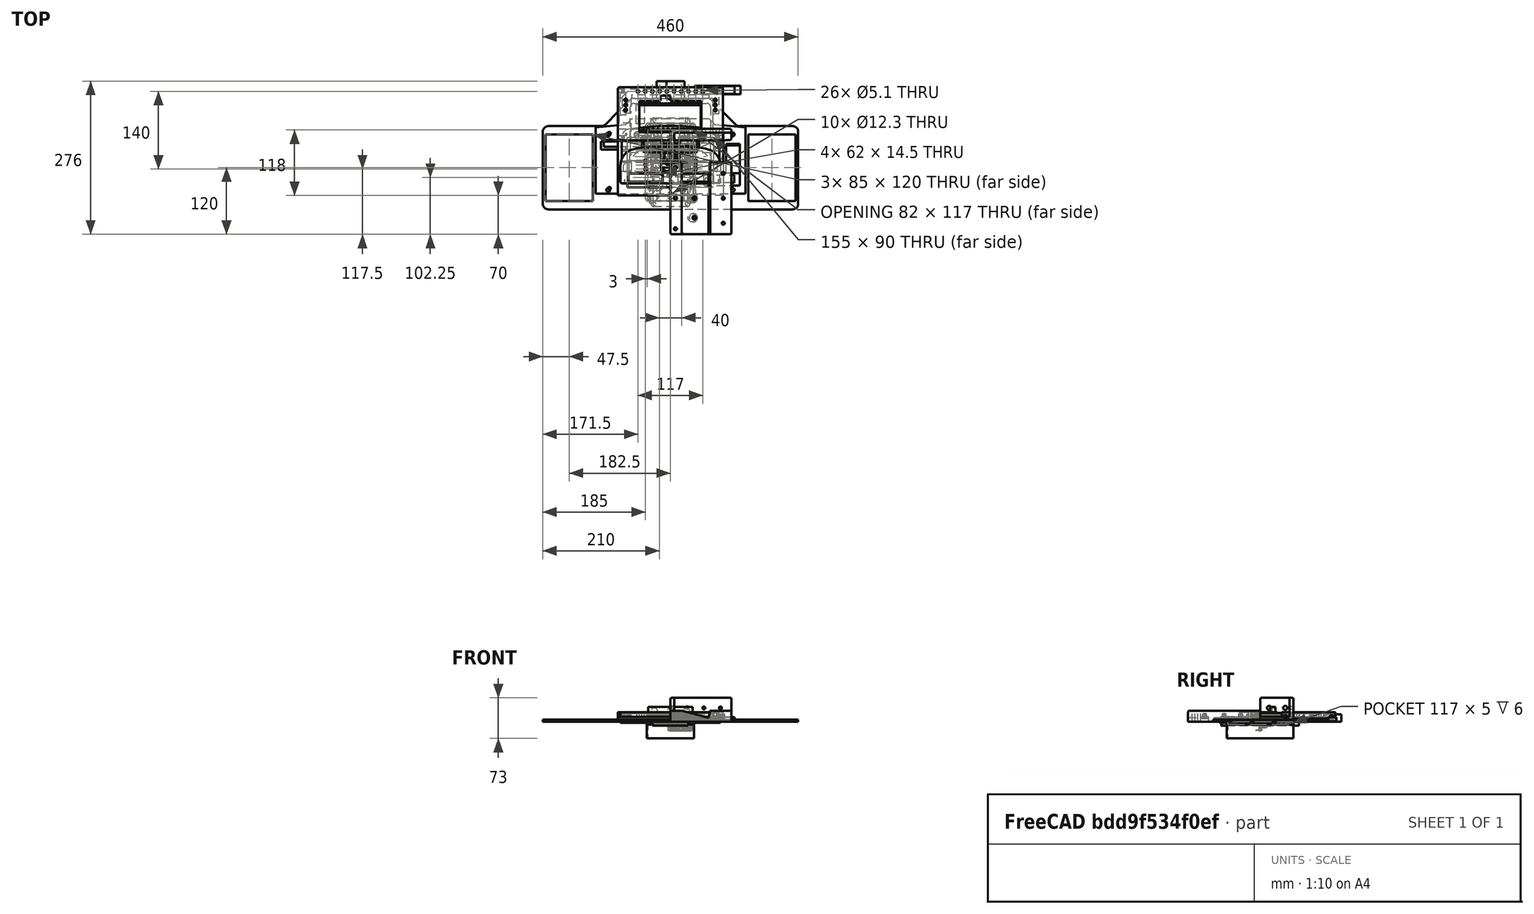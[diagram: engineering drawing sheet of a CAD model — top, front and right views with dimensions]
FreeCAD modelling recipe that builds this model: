
FCSTD DOCUMENT  (FreeCAD 0.18R4 (GitTag))
Label: wheelDashParts
License: All rights reserved
LicenseURL: http://en.wikipedia.org/wiki/All_rights_reserved
objects: Sketcher::SketchObject×55, TechDraw::DrawViewDimension×35, Part::Feature×33, PartDesign::Pad×31, PartDesign::Fillet×29, PartDesign::Body×22, PartDesign::Pocket×22, PartDesign::SubtractiveCylinder×21, PartDesign::SubtractiveBox×4, App::Part×3, PartDesign::Revolution×2, Spreadsheet::Sheet×1, TechDraw::DrawSVGTemplate×1, TechDraw::DrawViewPart×1, TechDraw::DrawPage×1, PartDesign::Plane×1
note: 300 computed .brp shape members not serialized (recipe doc carries the construction recipe); baked Part::Feature solids carry a one-line shape summary decoded from their .brp

FEATURE [Sketcher::SketchObject] Sketch
  MapMode = 5
  Support = -> [XY_Plane]
  sketch-geometry (27):
    g0: LineSegment StartX=-135 StartY=-57 StartZ=0 EndX=135 EndY=-57 EndZ=0
    g1: LineSegment StartX=80 StartY=68 StartZ=0 EndX=70 EndY=78 EndZ=0
    g2: LineSegment StartX=70 StartY=78 StartZ=0 EndX=-70 EndY=78 EndZ=0
    g3: LineSegment StartX=-70 StartY=78 StartZ=0 EndX=-80 EndY=68 EndZ=0
    g4: Circle CenterX=-28 CenterY=50 CenterZ=0 NormalX=0 NormalY=0 NormalZ=1 AngleXU=0 Radius=3.25
    g5: Circle CenterX=28 CenterY=50 CenterZ=0 NormalX=0 NormalY=0 NormalZ=1 AngleXU=0 Radius=3.25
    g6: Circle CenterX=-28 CenterY=-50 CenterZ=0 NormalX=0 NormalY=0 NormalZ=1 AngleXU=0 Radius=3.25
    g7: Circle CenterX=28 CenterY=-50 CenterZ=0 NormalX=0 NormalY=0 NormalZ=1 AngleXU=0 Radius=3.25
    g8: Circle CenterX=0 CenterY=8 CenterZ=0 NormalX=0 NormalY=0 NormalZ=1 AngleXU=0 Radius=25
    g9: LineSegment StartX=-120 StartY=40 StartZ=0 EndX=-30 EndY=40 EndZ=0
    g10: LineSegment StartX=-30 StartY=40 StartZ=0 EndX=-30 EndY=28 EndZ=0
    g11: LineSegment StartX=-30 StartY=28 StartZ=0 EndX=-120 EndY=28 EndZ=0
    g12: LineSegment StartX=-120 StartY=28 StartZ=0 EndX=-120 EndY=40 EndZ=0
    g13: LineSegment StartX=60 StartY=-32 StartZ=0 EndX=60 EndY=-42 EndZ=0
    g14: LineSegment StartX=60 StartY=-42 StartZ=0 EndX=125 EndY=-42 EndZ=0
    g15: LineSegment StartX=125 StartY=-42 StartZ=0 EndX=125 EndY=33 EndZ=0
    g16: LineSegment StartX=125 StartY=33 StartZ=0 EndX=100 EndY=33 EndZ=0
    g17: ArcOfCircle CenterX=5.90695 CenterY=46.0957 CenterZ=0 NormalX=0 NormalY=0 NormalZ=1 AngleXU=0 Radius=95 StartAngle=5.31817 EndAngle=6.1449
    g18: Circle CenterX=-61 CenterY=50 CenterZ=0 NormalX=0 NormalY=0 NormalZ=1 AngleXU=0 Radius=4.5
    g19: Circle CenterX=-110 CenterY=52 CenterZ=0 NormalX=0 NormalY=0 NormalZ=1 AngleXU=0 Radius=2.5
    g20: Circle CenterX=-110 CenterY=-47 CenterZ=0 NormalX=0 NormalY=0 NormalZ=1 AngleXU=0 Radius=2.5
    g21: Circle CenterX=110 CenterY=-47 CenterZ=0 NormalX=0 NormalY=0 NormalZ=1 AngleXU=0 Radius=2.5
    g22: Circle CenterX=110 CenterY=52 CenterZ=0 NormalX=0 NormalY=0 NormalZ=1 AngleXU=0 Radius=2.5
    g23: LineSegment StartX=-135 StartY=63 StartZ=0 EndX=-135 EndY=-57 EndZ=0
    g24: LineSegment StartX=-135 StartY=63 StartZ=0 EndX=-80 EndY=68 EndZ=0
    g25: LineSegment StartX=135 StartY=-57 StartZ=0 EndX=135 EndY=63 EndZ=0
    g26: LineSegment StartX=80 StartY=68 StartZ=0 EndX=135 EndY=63 EndZ=0
  constraints (74):
    c: Coincident(g1,g2)
    c: Coincident(g2,g3)
    c: Symmetric(g0,g0,g-2)
    c: Symmetric(g2,g1,g-2)
    c: Symmetric(g3,g1,g-2)
    c: DistanceX(g0,g0) = 270
    c: Symmetric(g6,g7,g-2)
    c: Symmetric(g4,g5,g-2)
    c: DistanceX(g6,g7) = 56
    c: DistanceY(g7,g5) = 100
    c: PointOnObject(g8,g-2)
    c: Coincident(g9,g10)
    c: Coincident(g10,g11)
    c: Coincident(g11,g12)
    c: Coincident(g12,g9)
    c: Horizontal(g9)
    c: Horizontal(g11)
    c: Vertical(g10)
    c: Vertical(g12)
    c: DistanceY(g12,g12) = 12
    c: DistanceX(g9,g9) = 90
    c: DistanceX(g9,g-1) = 30
    c: Diameter(g4) = 6.5
    c: Vertical(g13)
    c: Coincident(g13,g14)
    c: Horizontal(g14)
    c: Coincident(g14,g15)
    c: Vertical(g15)
    c: Coincident(g15,g16)
    c: Horizontal(g16)
    c: Coincident(g17,g13)
    c: Coincident(g17,g16)
    c: DistanceY(g0,g14) = 15
    c: DistanceX(g-1,g13) = 60
    c: DistanceY(g0,g15) = 90
    c: DistanceX(g-1,g16) = 100
    c: DistanceX(g16,g15) = 25
    c: Diameter(g8) = 50
    c: Equal(g4,g5)
    c: Equal(g5,g7)
    c: Equal(g7,g6)
    c: DistanceY(g0,g18) = 107
    c: DistanceY(g0,g11) = 85
    c: DistanceX(g18,g4) = 33
    c: Vertical(g19,g20)
    c: Symmetric(g19,g22,g-2)
    c: Equal(g21,g19)
    c: Equal(g19,g20)
    c: Equal(g20,g22)
    c: Diameter(g22) = 5
    c: DistanceX(g20,g-1) = 110
    c: DistanceY(g0,g20) = 10
    c: DistanceY(g0,g19) = 109
    c: Symmetric(g5,g7,g-1)
    c: DistanceY(g0,g8) = 65
    c: Diameter(g18) = 9
    c: Symmetric(g21,g20,g-2)
    c: DistanceY(g13,g13) = 10
    c: Diameter(g17) = 190
    c: Vertical(g23)
    c: Coincident(g23,g0)
    c: Coincident(g24,g23)
    c: Coincident(g24,g3)
    c: Coincident(g25,g0)
    c: Vertical(g25)
    c: DistanceY(g23,g23) = 120
    c: Equal(g25,g23)
    c: DistanceX(g3,g1) = 160
    c: DistanceY(g3,g2) = 10
    c: Horizontal(g18,g4)
    c: Coincident(g26,g1)
    c: Coincident(g26,g25)
    c: DistanceX(g3,g2) = 10
    c: DistanceY(g25,g1) = 5
FEATURE [PartDesign::Pad] Pad
  Length = 4
  Length2 = 100
  Profile = -> Sketch
  Type = 0
FEATURE [PartDesign::Body] Body  label="CSLElite"
  Group = -> [Sketch,Pad]
  Origin = -> Origin
  Tip = -> Pad
FEATURE [Sketcher::SketchObject] Sketch004
  MapMode = 5
  Support = -> [XY_Plane003]
  expr: Constraints[18] = data.bluWin_disp_length
  expr: Constraints[19] = data.bluWin_disp_width
  expr: Constraints[9] = data.bluWin_width
  expr: Constraints[8] = data.bluWin_length
  sketch-geometry (8):
    g0: LineSegment StartX=-72.5 StartY=36 StartZ=0 EndX=72.5 EndY=36 EndZ=0
    g1: LineSegment StartX=72.5 StartY=36 StartZ=0 EndX=72.5 EndY=-36 EndZ=0
    g2: LineSegment StartX=72.5 StartY=-36 StartZ=0 EndX=-72.5 EndY=-36 EndZ=0
    g3: LineSegment StartX=-72.5 StartY=-36 StartZ=0 EndX=-72.5 EndY=36 EndZ=0
    g4: LineSegment StartX=-57.5 StartY=32.5 StartZ=0 EndX=54.5 EndY=32.5 EndZ=0
    g5: LineSegment StartX=54.5 StartY=32.5 StartZ=0 EndX=54.5 EndY=-23.5 EndZ=0
    g6: LineSegment StartX=54.5 StartY=-23.5 StartZ=0 EndX=-57.5 EndY=-23.5 EndZ=0
    g7: LineSegment StartX=-57.5 StartY=-23.5 StartZ=0 EndX=-57.5 EndY=32.5 EndZ=0
  constraints (22):
    c: Coincident(g0,g1)
    c: Coincident(g1,g2)
    c: Coincident(g2,g3)
    c: Coincident(g3,g0)
    c: Horizontal(g2)
    c: Vertical(g3)
    c: Symmetric(g0,g0,g-2)
    c: Symmetric(g0,g1,g-1)
    c: DistanceX(g0,g0) = 145
    c: DistanceY(g1,g1) = 72
    c: Coincident(g4,g5)
    c: Coincident(g5,g6)
    c: Coincident(g6,g7)
    c: Coincident(g7,g4)
    c: Horizontal(g6)
    c: Vertical(g5)
    c: Vertical(g7)
    c: DistanceY(g4,g0) = 3.5
    c: DistanceX(g4,g4) = 112
    c: DistanceY(g7,g7) = 56
    c: DistanceX(g0,g4) = 15
    c: Equal(g7,g5)
FEATURE [PartDesign::Pad] Pad003
  Length = 9
  Length2 = 100
  Profile = -> Sketch004
  Type = 0
FEATURE [PartDesign::Fillet] Fillet003  label="bluWinHdLteFillet"
  Base = -> Pad003 [Edge1,Edge2,Edge8,Edge5]
  BaseFeature = -> Pad003
  Radius = 7
FEATURE [PartDesign::Body] Body003  label="bluWinHdLte"
  Group = -> [Sketch004,Pad003,Fillet003]
  Origin = -> Origin003
  Placement = pos=(0,70,0) rot=(0,0,1;0rad)
  Tip = -> Fillet003
FEATURE [Sketcher::SketchObject] Sketch005
  MapMode = 5
  Support = -> [XY_Plane004]
  sketch-geometry (8):
    g0: LineSegment StartX=-95 StartY=60 StartZ=0 EndX=95 EndY=60 EndZ=0
    g1: LineSegment StartX=95 StartY=60 StartZ=0 EndX=95 EndY=-60 EndZ=0
    g2: LineSegment StartX=95 StartY=-60 StartZ=0 EndX=-95 EndY=-60 EndZ=0
    g3: LineSegment StartX=-95 StartY=-60 StartZ=0 EndX=-95 EndY=60 EndZ=0
    g4: LineSegment StartX=-77.5 StartY=45 StartZ=0 EndX=77.5 EndY=45 EndZ=0
    g5: LineSegment StartX=77.5 StartY=45 StartZ=0 EndX=77.5 EndY=-45 EndZ=0
    g6: LineSegment StartX=77.5 StartY=-45 StartZ=0 EndX=-77.5 EndY=-45 EndZ=0
    g7: LineSegment StartX=-77.5 StartY=-45 StartZ=0 EndX=-77.5 EndY=45 EndZ=0
  constraints (20):
    c: Coincident(g0,g1)
    c: Coincident(g1,g2)
    c: Coincident(g2,g3)
    c: Coincident(g3,g0)
    c: Horizontal(g2)
    c: Vertical(g3)
    c: Symmetric(g0,g0,g-2)
    c: Symmetric(g0,g1,g-1)
    c: DistanceY(g1,g1) = 120
    c: DistanceX(g0,g0) = 190
    c: Coincident(g4,g5)
    c: Coincident(g5,g6)
    c: Coincident(g6,g7)
    c: Coincident(g7,g4)
    c: Horizontal(g6)
    c: Vertical(g7)
    c: Symmetric(g4,g5,g-1)
    c: Symmetric(g4,g4,g-2)
    c: DistanceX(g4,g4) = 155
    c: DistanceY(g5,g5) = 90
FEATURE [PartDesign::Pad] Pad004
  Length = 9
  Length2 = 100
  Profile = -> Sketch005
  Type = 0
FEATURE [PartDesign::Body] Body004  label="elfIItablet"
  Group = -> [Sketch005,Pad004]
  Origin = -> Origin004
  Tip = -> Pad004
FEATURE [Sketcher::SketchObject] Sketch006
  MapMode = 5
  Support = -> [XY_Plane005]
  expr: Constraints[9] = data.max8x8_width
  expr: Constraints[8] = data.max8x8_length
  sketch-geometry (4):
    g0: LineSegment StartX=-25 StartY=16 StartZ=0 EndX=25 EndY=16 EndZ=0
    g1: LineSegment StartX=25 StartY=16 StartZ=0 EndX=25 EndY=-16 EndZ=0
    g2: LineSegment StartX=25 StartY=-16 StartZ=0 EndX=-25 EndY=-16 EndZ=0
    g3: LineSegment StartX=-25 StartY=-16 StartZ=0 EndX=-25 EndY=16 EndZ=0
  constraints (10):
    c: Coincident(g0,g1)
    c: Coincident(g1,g2)
    c: Coincident(g2,g3)
    c: Coincident(g3,g0)
    c: Horizontal(g2)
    c: Vertical(g3)
    c: Symmetric(g0,g0,g-2)
    c: Symmetric(g0,g1,g-1)
    c: DistanceX(g0,g0) = 50
    c: DistanceY(g1,g1) = 32
FEATURE [PartDesign::Pad] Pad005
  Length = 1.5
  Length2 = 100
  Profile = -> Sketch006
  Type = 0
FEATURE [Sketcher::SketchObject] Sketch007
  ExternalGeometry = -> [Pad005]
  MapMode = 5
  Placement = pos=(0,0,1.5) rot=(0,0,1;0rad)
  Support = -> [Pad005]
  sketch-geometry (4):
    g0: LineSegment StartX=25 StartY=16 StartZ=0 EndX=-7 EndY=16 EndZ=0
    g1: LineSegment StartX=-7 StartY=16 StartZ=0 EndX=-7 EndY=-16 EndZ=0
    g2: LineSegment StartX=-7 StartY=-16 StartZ=0 EndX=25 EndY=-16 EndZ=0
    g3: LineSegment StartX=25 StartY=-16 StartZ=0 EndX=25 EndY=16 EndZ=0
  constraints (11):
    c: Coincident(g0,g1)
    c: Coincident(g1,g2)
    c: Coincident(g2,g3)
    c: Coincident(g3,g0)
    c: Horizontal(g0)
    c: Horizontal(g2)
    c: Vertical(g1)
    c: Vertical(g3)
    c: Equal(g3,g-3)
    c: Equal(g3,g0)
    c: Coincident(g-3,g0)
FEATURE [PartDesign::Pad] Pad006  label="max7219_8x8"
  BaseFeature = -> Pad005
  Length = 12
  Length2 = 100
  Profile = -> Sketch007
  Type = 0
  expr: Length = data.max8x8_height
FEATURE [PartDesign::Body] Body005  label="max7219module"
  Group = -> [Sketch006,Pad005,Sketch007,Pad006]
  Origin = -> Origin005
  Placement = pos=(0,130,0) rot=(0,0,1;0rad)
  Tip = -> Pad006
FEATURE [Sketcher::SketchObject] Sketch008
  MapMode = 5
  Support = -> [XY_Plane006]
  expr: Constraints[8] = data.seg7_length_all
  expr: Constraints[9] = data.seg7_width_all
  sketch-geometry (4):
    g0: LineSegment StartX=-41.15 StartY=7.75 StartZ=0 EndX=41.15 EndY=7.75 EndZ=0
    g1: LineSegment StartX=41.15 StartY=7.75 StartZ=0 EndX=41.15 EndY=-7.75 EndZ=0
    g2: LineSegment StartX=41.15 StartY=-7.75 StartZ=0 EndX=-41.15 EndY=-7.75 EndZ=0
    g3: LineSegment StartX=-41.15 StartY=-7.75 StartZ=0 EndX=-41.15 EndY=7.75 EndZ=0
  constraints (10):
    c: Coincident(g0,g1)
    c: Coincident(g1,g2)
    c: Coincident(g2,g3)
    c: Coincident(g3,g0)
    c: Horizontal(g0)
    c: Vertical(g1)
    c: Symmetric(g0,g2,g-1)
    c: Symmetric(g2,g1,g-2)
    c: DistanceX(g0,g0) = 82.3
    c: DistanceY(g3,g3) = 15.5
FEATURE [Spreadsheet::Sheet] Spreadsheet  label="data"
  cells = A1=7seg-length-all; B1(seg7_length_all)=82.3; A2=7seg-width-all; B2(seg7_width_all)=15.5; A3=7seg-length; B3(seg7_length)=61; A4=7seg-width; B4(seg7_width)=14.2; A5=7seg-height; B5(seg7_height)=7.6; A6=8x8-length-all; B6(max8x8_length)=50; A7=8x8-width-all; B7(max8x8_width)=32; A8=8x8-height; B8(max8x8_height)=12; A9=bluWin-length; B9(bluWin_length)=145; A10=bluWin-width; B10(bluWin_width)=72; A11=bluWin-height; B11(bluWin_height)=9; A12=bluWin-disp-length; B12(bluWin_disp_length)=112; A13=bluWin-disp-width; B13(bluWin_disp_width)=56; A14=bluWin-disp-leftdistance; B14(bluWin_disp_left)=15; A15=bluWin-disp-rightdistance; B15(bluWin_disp_right)=20; A16=bluWin_usblength; B16(bluWin_usblength)=20; A17=bluWin-disp-bottomdistance; B17(bluWin_disp_bottom)=13; A18=bluWin-disp-addline height; B18(bluWin_disp_addline)=7; A19=phoneholder thicknes of sides; B19(phoneholder_sides_thickness)=2; A20=rgbled radius; B20(rgbled_radius)=2.5; A21=rgbled length; B21(rgbled_length)=8; A22=phoneholder ledpart height; B22(phoneholder_ledpart_height)=10; A23=phoneholder total width; B23(phoneholder_width)==B12 + B14 + B15 + 2 * B16 + B19; D23=bluwin_disp_width+bluwin_disp_left+bluwin_disp_right_+(2*bluWin_usblength)+(2*phoneholder_sides_thickness)+(2*phoneholder_ledpart_height); A24=smalldash thickness; B24(smalldash_thickness)=17; A25=smalldash front thickness; B25(smalldash_frontthickness)=2
FEATURE [PartDesign::Pad] Pad007
  Length = 1
  Length2 = 100
  Profile = -> Sketch008
  Type = 0
FEATURE [Sketcher::SketchObject] Sketch009
  MapMode = 5
  Placement = pos=(0,0,1) rot=(0,0,1;0rad)
  Support = -> [Pad007]
  expr: Constraints[9] = data.seg7_width
  expr: Constraints[8] = data.seg7_length
  sketch-geometry (4):
    g0: LineSegment StartX=-30.5 StartY=7.1 StartZ=0 EndX=30.5 EndY=7.1 EndZ=0
    g1: LineSegment StartX=30.5 StartY=7.1 StartZ=0 EndX=30.5 EndY=-7.1 EndZ=0
    g2: LineSegment StartX=30.5 StartY=-7.1 StartZ=0 EndX=-30.5 EndY=-7.1 EndZ=0
    g3: LineSegment StartX=-30.5 StartY=-7.1 StartZ=0 EndX=-30.5 EndY=7.1 EndZ=0
  constraints (10):
    c: Coincident(g0,g1)
    c: Coincident(g1,g2)
    c: Coincident(g2,g3)
    c: Coincident(g3,g0)
    c: Horizontal(g2)
    c: Vertical(g1)
    c: Symmetric(g0,g2,g-1)
    c: Symmetric(g0,g0,g-2)
    c: DistanceX(g2,g2) = 61
    c: DistanceY(g1,g1) = 14.2
FEATURE [PartDesign::Pad] Pad008  label="max7219-7seg"
  BaseFeature = -> Pad007
  Length = 7.6
  Length2 = 100
  Profile = -> Sketch009
  Type = 0
  expr: Length = data.seg7_height
FEATURE [PartDesign::Body] Body006  label="max7219_7seg"
  Group = -> [Sketch008,Pad007,Sketch009,Pad008]
  Origin = -> Origin006
  Placement = pos=(85,130,0) rot=(0,0,1;0rad)
  Tip = -> Pad008
FEATURE [Sketcher::SketchObject] Sketch010
  MapMode = 5
  Support = -> [XY_Plane002]
  sketch-geometry (47):
    g0: LineSegment [constr] StartX=-135 StartY=60 StartZ=0 EndX=135 EndY=60 EndZ=0
    g1: LineSegment [constr] StartX=135 StartY=60 StartZ=0 EndX=135 EndY=-60 EndZ=0
    g2: LineSegment [constr] StartX=135 StartY=-60 StartZ=0 EndX=-135 EndY=-60 EndZ=0
    g3: LineSegment [constr] StartX=-135 StartY=-60 StartZ=0 EndX=-135 EndY=60 EndZ=0
    g4: LineSegment StartX=-230 StartY=-85 StartZ=0 EndX=-230 EndY=65 EndZ=0
    g5: LineSegment StartX=-230 StartY=65 StartZ=0 EndX=-120 EndY=65 EndZ=0
    g6: LineSegment StartX=-120 StartY=65 StartZ=0 EndX=-70 EndY=115 EndZ=0
    g7: LineSegment StartX=-70 StartY=115 StartZ=0 EndX=70 EndY=115 EndZ=0
    g8: LineSegment StartX=70 StartY=115 StartZ=0 EndX=120 EndY=65 EndZ=0
    g9: LineSegment StartX=120 StartY=65 StartZ=0 EndX=230 EndY=65 EndZ=0
    g10: LineSegment StartX=230 StartY=65 StartZ=0 EndX=230 EndY=-85 EndZ=0
    g11: LineSegment StartX=230 StartY=-85 StartZ=0 EndX=-230 EndY=-85 EndZ=0
    g12: Circle CenterX=0 CenterY=-3.1e-15 CenterZ=0 NormalX=0 NormalY=0 NormalZ=1 AngleXU=0 Radius=27.5
    g13: Circle CenterX=-28 CenterY=51 CenterZ=0 NormalX=0 NormalY=0 NormalZ=1 AngleXU=0 Radius=3.25
    g14: Circle CenterX=28 CenterY=51 CenterZ=0 NormalX=0 NormalY=0 NormalZ=1 AngleXU=0 Radius=3.25
    g15: Circle CenterX=-28 CenterY=-49 CenterZ=0 NormalX=0 NormalY=0 NormalZ=1 AngleXU=0 Radius=3.25
    g16: Circle CenterX=28 CenterY=-49 CenterZ=0 NormalX=0 NormalY=0 NormalZ=1 AngleXU=0 Radius=3.25
    g17: Circle CenterX=-112 CenterY=-50 CenterZ=0 NormalX=0 NormalY=0 NormalZ=1 AngleXU=0 Radius=3.5
    g18: Circle CenterX=-112 CenterY=50 CenterZ=0 NormalX=0 NormalY=0 NormalZ=1 AngleXU=0 Radius=3.5
    g19: Circle CenterX=112 CenterY=50 CenterZ=0 NormalX=0 NormalY=0 NormalZ=1 AngleXU=0 Radius=3.5
    g20: Circle CenterX=112 CenterY=-50 CenterZ=0 NormalX=0 NormalY=0 NormalZ=1 AngleXU=0 Radius=3.5
    g21: Circle CenterX=-61 CenterY=47 CenterZ=0 NormalX=0 NormalY=0 NormalZ=1 AngleXU=0 Radius=4.5
    g22: Circle CenterX=61 CenterY=47 CenterZ=0 NormalX=0 NormalY=0 NormalZ=1 AngleXU=0 Radius=4.5
    g23: LineSegment StartX=100 StartY=30 StartZ=0 EndX=125 EndY=30 EndZ=0
    g24: LineSegment StartX=125 StartY=30 StartZ=0 EndX=125 EndY=-20 EndZ=0
    g25: LineSegment StartX=125 StartY=-20 StartZ=0 EndX=100 EndY=-20 EndZ=0
    g26: LineSegment StartX=100 StartY=-20 StartZ=0 EndX=100 EndY=30 EndZ=0
    g27: LineSegment StartX=60 StartY=-23 StartZ=0 EndX=115 EndY=-23 EndZ=0
    g28: LineSegment StartX=115 StartY=-23 StartZ=0 EndX=115 EndY=-37 EndZ=0
    g29: LineSegment StartX=115 StartY=-37 StartZ=0 EndX=60 EndY=-37 EndZ=0
    g30: LineSegment StartX=60 StartY=-37 StartZ=0 EndX=60 EndY=-23 EndZ=0
    g31: LineSegment StartX=-125 StartY=37 StartZ=0 EndX=-25 EndY=37 EndZ=0
    g32: LineSegment StartX=-25 StartY=37 StartZ=0 EndX=-25 EndY=23 EndZ=0
    g33: LineSegment StartX=-25 StartY=23 StartZ=0 EndX=-125 EndY=23 EndZ=0
    g34: LineSegment StartX=-125 StartY=23 StartZ=0 EndX=-125 EndY=37 EndZ=0
    g35: LineSegment StartX=140 StartY=50 StartZ=0 EndX=225 EndY=50 EndZ=0
    g36: LineSegment StartX=225 StartY=50 StartZ=0 EndX=225 EndY=-70 EndZ=0
    g37: LineSegment StartX=225 StartY=-70 StartZ=0 EndX=140 EndY=-70 EndZ=0
    g38: LineSegment StartX=140 StartY=-70 StartZ=0 EndX=140 EndY=50 EndZ=0
    g39: LineSegment StartX=-225 StartY=50 StartZ=0 EndX=-140 EndY=50 EndZ=0
    g40: LineSegment StartX=-140 StartY=50 StartZ=0 EndX=-140 EndY=-70 EndZ=0
    g41: LineSegment StartX=-140 StartY=-70 StartZ=0 EndX=-225 EndY=-70 EndZ=0
    g42: LineSegment StartX=-225 StartY=-70 StartZ=0 EndX=-225 EndY=50 EndZ=0
    g43: LineSegment StartX=-62 StartY=104 StartZ=0 EndX=-47 EndY=104 EndZ=0
    g44: LineSegment StartX=-47 StartY=104 StartZ=0 EndX=-47 EndY=69 EndZ=0
    g45: LineSegment StartX=-47 StartY=69 StartZ=0 EndX=-62 EndY=69 EndZ=0
    g46: LineSegment StartX=-62 StartY=69 StartZ=0 EndX=-62 EndY=104 EndZ=0
  constraints (130):
    c: Coincident(g0,g1)
    c: Coincident(g1,g2)
    c: Coincident(g2,g3)
    c: Coincident(g3,g0)
    c: Horizontal(g2)
    c: Vertical(g1)
    c: DistanceY(g3,g3) = 120
    c: DistanceX(g0,g0) = 270
    c: Symmetric(g0,g0,g-2)
    c: Symmetric(g0,g2,g-1)
    c: Vertical(g4)
    c: Coincident(g4,g5)
    c: Horizontal(g5)
    c: Coincident(g5,g6)
    c: Coincident(g6,g7)
    c: Coincident(g7,g8)
    c: Coincident(g8,g9)
    c: Coincident(g9,g10)
    c: Vertical(g10)
    c: Coincident(g10,g11)
    c: Coincident(g4,g11)
    c: DistanceY(g4,g4) = 150
    c: DistanceX(g11,g11) = 460
    c: Symmetric(g4,g10,g-2)
    c: Equal(g4,g10)
    c: Symmetric(g6,g7,g-2)
    c: Symmetric(g5,g8,g-2)
    c: PointOnObject(g12,g-2)
    c: DistanceY(g1,g12) = 60
    c: DistanceY(g4,g6) = 50
    c: Diameter(g12) = 55
    c: Symmetric(g15,g16,g-2)
    c: Symmetric(g13,g14,g-2)
    c: Vertical(g13,g15)
    c: Equal(g13,g14)
    c: Equal(g14,g16)
    c: Equal(g16,g15)
    c: DistanceY(g2,g15) = 11
    c: DistanceX(g15,g16) = 56
    c: DistanceY(g16,g14) = 100
    c: DistanceY(g4,g2) = 25
    c: Equal(g18,g17)
    c: Equal(g17,g20)
    c: Equal(g20,g19)
    c: DistanceY(g2,g17) = 10
    c: DistanceY(g2,g18) = 110
    c: Symmetric(g18,g19,g-2)
    c: Symmetric(g17,g20,g-2)
    c: DistanceX(g17,g12) = 112
    c: Vertical(g18,g17)
    c: DistanceX(g21,g13) = 33
    c: DistanceY(g2,g21) = 107
    c: Symmetric(g21,g22,g-2)
    c: Equal(g21,g22)
    c: Diameter(g18) = 7
    c: Diameter(g22) = 9
    c: Diameter(g15) = 6.5
    c: DistanceX(g8,g9) = 110
    c: Coincident(g23,g24)
    c: Coincident(g24,g25)
    c: Coincident(g25,g26)
    c: Coincident(g26,g23)
    c: Horizontal(g23)
    c: Horizontal(g25)
    c: Vertical(g24)
    c: Vertical(g26)
    c: DistanceX(g23,g23) = 25
    c: DistanceY(g26,g26) = 50
    c: DistanceY(g1,g25) = 40
    c: DistanceX(g12,g25) = 100
    c: Coincident(g27,g28)
    c: Coincident(g28,g29)
    c: Coincident(g29,g30)
    c: Coincident(g30,g27)
    c: Horizontal(g27)
    c: Horizontal(g29)
    c: Vertical(g28)
    c: Vertical(g30)
    c: DistanceX(g29,g29) = 55
    c: DistanceY(g28,g28) = 14
    c: DistanceY(g1,g29) = 23
    c: DistanceX(g12,g27) = 60
    c: Coincident(g31,g32)
    c: Coincident(g32,g33)
    c: Coincident(g33,g34)
    c: Coincident(g34,g31)
    c: Horizontal(g31)
    c: Horizontal(g33)
    c: Vertical(g32)
    c: Vertical(g34)
    c: DistanceX(g33,g33) = 100
    c: DistanceX(g32,g12) = 25
    c: DistanceY(g2,g33) = 83
    c: Coincident(g35,g36)
    c: Coincident(g36,g37)
    c: Coincident(g37,g38)
    c: Coincident(g38,g35)
    c: Horizontal(g35)
    c: Horizontal(g37)
    c: Vertical(g36)
    c: Vertical(g38)
    c: DistanceX(g35,g35) = 85
    c: DistanceY(g38,g38) = 120
    c: DistanceX(g35,g9) = 5
    c: DistanceY(g35,g9) = 15
    c: Coincident(g39,g40)
    c: Coincident(g40,g41)
    c: Coincident(g41,g42)
    c: Coincident(g42,g39)
    c: Horizontal(g39)
    c: Horizontal(g41)
    c: Vertical(g40)
    c: Vertical(g42)
    c: Equal(g38,g40)
    c: Equal(g41,g37)
    c: Symmetric(g40,g37,g-2)
    c: DistanceY(g34,g34) = 14
    c: Coincident(g43,g44)
    c: Coincident(g44,g45)
    c: Coincident(g45,g46)
    c: Coincident(g46,g43)
    c: Horizontal(g43)
    c: Horizontal(g45)
    c: Vertical(g44)
    c: Vertical(g46)
    c: DistanceX(g43,g43) = 15
    c: DistanceY(g44,g44) = 35
    c: DistanceX(g6,g43) = 8
    c: DistanceY(g43,g6) = 11
    c: Angle(g8) = -0.785398
FEATURE [PartDesign::Pad] Pad009
  Length = 4
  Length2 = 100
  Profile = -> Sketch010
  Type = 0
FEATURE [PartDesign::Fillet] Fillet004
  Base = -> Pad009 [Edge14,Edge11,Edge8,Edge5,Edge2,Edge17,Edge1,Edge20]
  BaseFeature = -> Pad009
  Radius = 10
FEATURE [PartDesign::Body] Body002  label="Dashboard"
  Group = -> [Sketch010,Pad009,Fillet004]
  Origin = -> Origin002
  Tip = -> Fillet004
FEATURE [Sketcher::SketchObject] Sketch011
  MapMode = 5
  Support = -> [XY_Plane007]
  expr: Constraints[6] = data.bluWin_disp_length
  expr: Constraints[31] = data.bluWin_disp_bottom
  expr: Constraints[30] = data.bluWin_length
  expr: Constraints[7] = data.bluWin_disp_width
  expr: Constraints[17] = data.bluWin_disp_bottom + data.phoneholder_sides_thickness
  expr: Constraints[18] = data.phoneholder_sides_thickness * 2 + data.bluWin_width + 2 * data.phoneholder_ledpart_height
  expr: Constraints[20] = data.phoneholder_width
  expr: Constraints[29] = data.bluWin_width
  expr: Constraints[32] = data.bluWin_disp_left
  sketch-geometry (16):
    g0: LineSegment StartX=-56 StartY=28 StartZ=0 EndX=56 EndY=28 EndZ=0
    g1: LineSegment StartX=56 StartY=28 StartZ=0 EndX=56 EndY=-28 EndZ=0
    g2: LineSegment StartX=56 StartY=-28 StartZ=0 EndX=-56 EndY=-28 EndZ=0
    g3: LineSegment StartX=-56 StartY=-28 StartZ=0 EndX=-56 EndY=28 EndZ=0
    g4: LineSegment StartX=-94.5 StartY=53 StartZ=0 EndX=94.5 EndY=53 EndZ=0
    g5: LineSegment StartX=94.5 StartY=53 StartZ=0 EndX=94.5 EndY=-43 EndZ=0
    g6: LineSegment StartX=94.5 StartY=-43 StartZ=0 EndX=-94.5 EndY=-43 EndZ=0
    g7: LineSegment StartX=-94.5 StartY=-43 StartZ=0 EndX=-94.5 EndY=53 EndZ=0
    g8: LineSegment [constr] StartX=-71 StartY=31 StartZ=0 EndX=74 EndY=31 EndZ=0
    g9: LineSegment [constr] StartX=74 StartY=31 StartZ=0 EndX=74 EndY=-41 EndZ=0
    g10: LineSegment [constr] StartX=74 StartY=-41 StartZ=0 EndX=-71 EndY=-41 EndZ=0
    g11: LineSegment [constr] StartX=-71 StartY=-41 StartZ=0 EndX=-71 EndY=31 EndZ=0
    g12: LineSegment [constr] StartX=-91.5 StartY=43 StartZ=0 EndX=-81.5 EndY=43 EndZ=0
    g13: LineSegment [constr] StartX=-81.5 StartY=43 StartZ=0 EndX=-81.5 EndY=25 EndZ=0
    g14: LineSegment [constr] StartX=-81.5 StartY=25 StartZ=0 EndX=-91.5 EndY=25 EndZ=0
    g15: LineSegment [constr] StartX=-91.5 StartY=25 StartZ=0 EndX=-91.5 EndY=43 EndZ=0
  constraints (45):
    c: Coincident(g0,g1)
    c: Coincident(g1,g2)
    c: Coincident(g2,g3)
    c: Coincident(g3,g0)
    c: Horizontal(g2)
    c: Vertical(g3)
    c: DistanceX(g0,g0) = 112
    c: DistanceY(g1,g1) = 56
    c: Symmetric(g0,g0,g-2)
    c: Symmetric(g0,g1,g-1)
    c: Coincident(g4,g5)
    c: Coincident(g5,g6)
    c: Coincident(g6,g7)
    c: Coincident(g7,g4)
    c: Horizontal(g6)
    c: Vertical(g7)
    c: Symmetric(g4,g4,g-2)
    c: DistanceY(g5,g1) = 15
    c: DistanceY(g5,g5) = 96
    c: Vertical(g5)
    c: DistanceX(g6,g6) = 189
    c: Coincident(g8,g9)
    c: Coincident(g9,g10)
    c: Coincident(g10,g11)
    c: Coincident(g11,g8)
    c: Horizontal(g8)
    c: Horizontal(g10)
    c: Vertical(g9)
    c: Vertical(g11)
    c: DistanceY(g11,g11) = 72
    c: DistanceX(g10,g10) = 145
    c: DistanceY(g10,g2) = 13
    c: DistanceX(g10,g2) = 15
    c: Coincident(g12,g13)
    c: Coincident(g13,g14)
    c: Coincident(g14,g15)
    c: Coincident(g15,g12)
    c: Horizontal(g12)
    c: Horizontal(g14)
    c: Vertical(g13)
    c: Vertical(g15)
    c: DistanceX(g12,g12) = 10
    c: DistanceY(g13,g13) = 18
    c: DistanceX(g4,g12) = 3
    c: DistanceY(g12,g4) = 10
FEATURE [PartDesign::Pad] Pad010
  Length = 2
  Length2 = 100
  Profile = -> Sketch011
  Type = 0
FEATURE [Sketcher::SketchObject] Sketch012
  ExternalGeometry = -> [Pad010]
  MapMode = 5
  Placement = pos=(0,0,0) rot=(1,0,0;3.14159rad)
  Support = -> [Pad010]
  expr: Constraints[29] = data.bluWin_disp_right
  expr: Constraints[17] = data.bluWin_disp_bottom
  expr: Constraints[27] = data.bluWin_usblength + 1
  expr: Constraints[14] = data.bluWin_width + 2
  expr: Constraints[18] = data.bluWin_disp_left
  sketch-geometry (15):
    g0: LineSegment StartX=-94.5 StartY=43 StartZ=0 EndX=94.5 EndY=43 EndZ=0
    g1: LineSegment StartX=94.5 StartY=43 StartZ=0 EndX=94.5 EndY=-53 EndZ=0
    g2: LineSegment StartX=94.5 StartY=-53 StartZ=0 EndX=-94.5 EndY=-53 EndZ=0
    g3: LineSegment StartX=-94.5 StartY=-53 StartZ=0 EndX=-94.5 EndY=43 EndZ=0
    g4: LineSegment StartX=-71 StartY=41 StartZ=0 EndX=76 EndY=41 EndZ=0
    g5: LineSegment StartX=76 StartY=-33 StartZ=0 EndX=-71 EndY=-33 EndZ=0
    g6: LineSegment StartX=-71 StartY=-33 StartZ=0 EndX=-71 EndY=-7 EndZ=0
    g7: LineSegment StartX=76 StartY=-33 StartZ=0 EndX=76 EndY=41 EndZ=0
    g8: LineSegment StartX=-71 StartY=12 StartZ=0 EndX=-92 EndY=12 EndZ=0
    g9: LineSegment StartX=-92 StartY=12 StartZ=0 EndX=-92 EndY=-34 EndZ=0
    g10: LineSegment StartX=-92 StartY=-34 StartZ=0 EndX=-87 EndY=-34 EndZ=0
    g11: LineSegment StartX=-87 StartY=-34 StartZ=0 EndX=-87 EndY=-11.9497 EndZ=0
    g12: LineSegment StartX=-82.0503 StartY=-7 StartZ=0 EndX=-71 EndY=-7 EndZ=0
    g13: LineSegment StartX=-71 StartY=12 StartZ=0 EndX=-71 EndY=41 EndZ=0
    g14: LineSegment StartX=-87 StartY=-11.9497 StartZ=0 EndX=-82.0503 EndY=-7 EndZ=0
  constraints (42):
    c: Coincident(g0,g1)
    c: Coincident(g1,g2)
    c: Coincident(g2,g3)
    c: Coincident(g3,g0)
    c: Horizontal(g0)
    c: Horizontal(g2)
    c: Vertical(g1)
    c: Vertical(g3)
    c: Coincident(g0,g-5)
    c: Coincident(g1,g-6)
    c: Coincident(g13,g4)
    c: Horizontal(g4)
    c: Horizontal(g5)
    c: Vertical(g6)
    c: DistanceY(g6,g13) = 74
    c: Vertical(g7)
    c: Coincident(g5,g7)
    c: DistanceY(g-3,g4) = 13
    c: DistanceX(g4,g-3) = 15
    c: Horizontal(g8)
    c: Coincident(g8,g9)
    c: Vertical(g9)
    c: Coincident(g9,g10)
    c: Horizontal(g10)
    c: Coincident(g10,g11)
    c: Vertical(g11)
    c: Horizontal(g12)
    c: DistanceX(g8,g8) = 21
    c: Coincident(g4,g7)
    c: DistanceX(g-3,g4) = 20
    c: Coincident(g6,g12)
    c: Tangent(g6,g13)
    c: DistanceX(g10,g10) = 5
    c: Coincident(g6,g5)
    c: DistanceY(g5,g6) = 26
    c: DistanceY(g5,g8) = 45
    c: Coincident(g8,g13)
    c: DistanceY(g9,g8) = 46
    c: Coincident(g12,g14)
    c: Coincident(g11,g14)
    c: Distance(g14) = 7
    c: Angle(g14) = 0.785398
FEATURE [PartDesign::Pad] Pad011
  BaseFeature = -> Pad010
  Length = 9.5
  Length2 = 100
  Profile = -> Sketch012
  Type = 0
  expr: Length = data.bluWin_height + 0.5
FEATURE [Sketcher::SketchObject] Sketch013
  ExternalGeometry = -> [Pad011]
  MapMode = 5
  Placement = pos=(0,0,-9.5) rot=(1,0,0;3.14159rad)
  Support = -> [Pad011]
  sketch-geometry (4):
    g0: Circle CenterX=-86.5 CenterY=37 CenterZ=0 NormalX=0 NormalY=0 NormalZ=1 AngleXU=0 Radius=1.7
    g1: Circle CenterX=-86.5 CenterY=-47 CenterZ=0 NormalX=0 NormalY=0 NormalZ=1 AngleXU=0 Radius=1.7
    g2: Circle CenterX=86.5 CenterY=37 CenterZ=0 NormalX=0 NormalY=0 NormalZ=1 AngleXU=0 Radius=1.7
    g3: Circle CenterX=86.5 CenterY=-47 CenterZ=0 NormalX=0 NormalY=0 NormalZ=1 AngleXU=0 Radius=1.7
  constraints (11):
    c: Equal(g0,g1)
    c: Equal(g1,g3)
    c: Equal(g3,g2)
    c: Vertical(g0,g1)
    c: Vertical(g3,g2)
    c: Symmetric(g0,g2,g-2)
    c: DistanceY(g2,g-3) = 6
    c: DistanceY(g-4,g3) = 6
    c: DistanceX(g2,g-3) = 8
    c: Horizontal(g1,g3)
    c: Diameter(g0) = 3.4
FEATURE [PartDesign::Pocket] Pocket  label="screwholes"
  BaseFeature = -> Pad011
  Length = 9
  Length2 = 100
  Profile = -> Sketch013
  Type = 0
FEATURE [Sketcher::SketchObject] Sketch014
  ExternalGeometry = -> [Pocket]
  MapMode = 5
  Placement = pos=(-94.5,0,0) rot=(0.57735,-0.57735,-0.57735;2.0944rad)
  Support = -> [Pocket]
  sketch-geometry (8):
    g0: LineSegment StartX=39.9 StartY=-3.2 StartZ=0 EndX=33.9 EndY=-3.2 EndZ=0
    g1: LineSegment StartX=33.9 StartY=-3.2 StartZ=0 EndX=33.9 EndY=-6 EndZ=0
    g2: LineSegment StartX=33.9 StartY=-6 StartZ=0 EndX=39.9 EndY=-6 EndZ=0
    g3: LineSegment StartX=39.9 StartY=-6 StartZ=0 EndX=39.9 EndY=-3.2 EndZ=0
    g4: LineSegment StartX=-43.9 StartY=-3.2 StartZ=0 EndX=-49.9 EndY=-3.2 EndZ=0
    g5: LineSegment StartX=-49.9 StartY=-3.2 StartZ=0 EndX=-49.9 EndY=-6 EndZ=0
    g6: LineSegment StartX=-49.9 StartY=-6 StartZ=0 EndX=-43.9 EndY=-6 EndZ=0
    g7: LineSegment StartX=-43.9 StartY=-6 StartZ=0 EndX=-43.9 EndY=-3.2 EndZ=0
  constraints (24):
    c: Coincident(g0,g1)
    c: Coincident(g1,g2)
    c: Coincident(g2,g3)
    c: Coincident(g3,g0)
    c: Horizontal(g0)
    c: Horizontal(g2)
    c: Vertical(g1)
    c: Vertical(g3)
    c: Coincident(g4,g5)
    c: Coincident(g5,g6)
    c: Coincident(g6,g7)
    c: Coincident(g7,g4)
    c: Horizontal(g4)
    c: Horizontal(g6)
    c: Vertical(g5)
    c: Vertical(g7)
    c: DistanceY(g3,g3) = 2.8
    c: DistanceX(g0,g0) = 6
    c: Equal(g1,g7)
    c: Equal(g4,g0)
    c: DistanceY(g-3,g2) = 3.5
    c: DistanceX(g2,g-3) = 3.1
    c: Horizontal(g6,g1)
    c: DistanceX(g-3,g5) = 3.1
FEATURE [PartDesign::Pocket] Pocket001  label="nutholes1"
  BaseFeature = -> Pocket
  Length = 12
  Length2 = 100
  Profile = -> Sketch014
  Type = 0
FEATURE [Sketcher::SketchObject] Sketch015
  ExternalGeometry = -> [Pocket001]
  MapMode = 5
  Placement = pos=(94.5,0,0) rot=(0.57735,0.57735,0.57735;2.0944rad)
  Support = -> [Pocket001]
  sketch-geometry (8):
    g0: LineSegment StartX=-39.9 StartY=-3.2 StartZ=0 EndX=-33.9 EndY=-3.2 EndZ=0
    g1: LineSegment StartX=-33.9 StartY=-3.2 StartZ=0 EndX=-33.9 EndY=-6 EndZ=0
    g2: LineSegment StartX=-33.9 StartY=-6 StartZ=0 EndX=-39.9 EndY=-6 EndZ=0
    g3: LineSegment StartX=-39.9 StartY=-6 StartZ=0 EndX=-39.9 EndY=-3.2 EndZ=0
    g4: LineSegment StartX=49.9 StartY=-3.2 StartZ=0 EndX=43.9 EndY=-3.2 EndZ=0
    g5: LineSegment StartX=43.9 StartY=-3.2 StartZ=0 EndX=43.9 EndY=-6 EndZ=0
    g6: LineSegment StartX=43.9 StartY=-6 StartZ=0 EndX=49.9 EndY=-6 EndZ=0
    g7: LineSegment StartX=49.9 StartY=-6 StartZ=0 EndX=49.9 EndY=-3.2 EndZ=0
  constraints (24):
    c: Coincident(g0,g1)
    c: Coincident(g1,g2)
    c: Coincident(g2,g3)
    c: Coincident(g3,g0)
    c: Horizontal(g0)
    c: Horizontal(g2)
    c: Vertical(g1)
    c: Vertical(g3)
    c: Coincident(g4,g5)
    c: Coincident(g5,g6)
    c: Coincident(g6,g7)
    c: Coincident(g7,g4)
    c: Horizontal(g4)
    c: Horizontal(g6)
    c: Vertical(g5)
    c: Vertical(g7)
    c: DistanceX(g4,g4) = 6
    c: DistanceY(g7,g7) = 2.8
    c: DistanceY(g-3,g6) = 3.5
    c: DistanceX(g6,g-3) = 3.1
    c: Equal(g5,g1)
    c: Equal(g0,g4)
    c: Horizontal(g1,g5)
    c: DistanceX(g-3,g2) = 3.1
FEATURE [PartDesign::Pocket] Pocket002  label="nutholes2"
  BaseFeature = -> Pocket001
  Length = 12
  Length2 = 100
  Profile = -> Sketch015
  Type = 0
FEATURE [Sketcher::SketchObject] Sketch016
  ExternalGeometry = -> [Pocket002]
  MapMode = 5
  Placement = pos=(0,0,-9.5) rot=(1,0,0;3.14159rad)
  Support = -> [Pocket002]
  sketch-geometry (4):
    g0: LineSegment StartX=-18 StartY=-28 StartZ=0 EndX=3.6e-15 EndY=-28 EndZ=0
    g1: LineSegment StartX=4.4e-15 StartY=-28 StartZ=0 EndX=4.4e-15 EndY=-38 EndZ=0
    g2: LineSegment StartX=4.4e-15 StartY=-38 StartZ=0 EndX=-18 EndY=-38 EndZ=0
    g3: LineSegment StartX=-18 StartY=-38 StartZ=0 EndX=-18 EndY=-28 EndZ=0
  constraints (12):
    c: Horizontal(g0)
    c: Horizontal(g2)
    c: DistanceY(g1,g1) = 10
    c: Coincident(g0,g3)
    c: Coincident(g0,g1)
    c: Vertical(g1)
    c: Vertical(g3)
    c: Coincident(g2,g3)
    c: Coincident(g2,g1)
    c: PointOnObject(g0,g-5)
    c: DistanceX(g-5,g0) = 38
    c: DistanceX(g2,g2) = 18
FEATURE [PartDesign::Pocket] Pocket003  label="switchhole"
  BaseFeature = -> Pocket002
  Length = 5
  Length2 = 100
  Profile = -> Sketch016
  Type = 1
FEATURE [Sketcher::SketchObject] Sketch017
  ExternalGeometry = -> [Pocket003]
  MapMode = 5
  Placement = pos=(0,0,-9.5) rot=(1,0,0;3.14159rad)
  Support = -> [Pocket003]
  sketch-geometry (29):
    g0: Circle CenterX=-58.5 CenterY=-45.5 CenterZ=0 NormalX=0 NormalY=0 NormalZ=1 AngleXU=0 Radius=2.55
    g1: Circle CenterX=-45.5 CenterY=-45.5 CenterZ=0 NormalX=0 NormalY=0 NormalZ=1 AngleXU=0 Radius=2.55
    g2: LineSegment [constr] StartX=-58.5 StartY=-45.5 StartZ=0 EndX=-45.5 EndY=-45.5 EndZ=0
    g3: Circle CenterX=-32.5 CenterY=-45.5 CenterZ=0 NormalX=0 NormalY=0 NormalZ=1 AngleXU=0 Radius=2.55
    g4: LineSegment [constr] StartX=-45.5 StartY=-45.5 StartZ=0 EndX=-32.5 EndY=-45.5 EndZ=0
    g5: Circle CenterX=-19.5 CenterY=-45.5 CenterZ=0 NormalX=0 NormalY=0 NormalZ=1 AngleXU=0 Radius=2.55
    g6: LineSegment [constr] StartX=-32.5 StartY=-45.5 StartZ=0 EndX=-19.5 EndY=-45.5 EndZ=0
    g7: Circle CenterX=-6.5 CenterY=-45.5 CenterZ=0 NormalX=0 NormalY=0 NormalZ=1 AngleXU=0 Radius=2.55
    g8: LineSegment [constr] StartX=-19.5 StartY=-45.5 StartZ=0 EndX=-6.5 EndY=-45.5 EndZ=0
    g9: Circle CenterX=6.5 CenterY=-45.5 CenterZ=0 NormalX=0 NormalY=0 NormalZ=1 AngleXU=0 Radius=2.55
    g10: LineSegment [constr] StartX=-6.5 StartY=-45.5 StartZ=0 EndX=6.5 EndY=-45.5 EndZ=0
    g11: Circle CenterX=19.5 CenterY=-45.5 CenterZ=0 NormalX=0 NormalY=0 NormalZ=1 AngleXU=0 Radius=2.55
    g12: LineSegment [constr] StartX=6.5 StartY=-45.5 StartZ=0 EndX=19.5 EndY=-45.5 EndZ=0
    g13: Circle CenterX=32.5 CenterY=-45.5 CenterZ=0 NormalX=0 NormalY=0 NormalZ=1 AngleXU=0 Radius=2.55
    g14: LineSegment [constr] StartX=19.5 StartY=-45.5 StartZ=0 EndX=32.5 EndY=-45.5 EndZ=0
    g15: Circle CenterX=45.5 CenterY=-45.5 CenterZ=0 NormalX=0 NormalY=0 NormalZ=1 AngleXU=0 Radius=2.55
    g16: LineSegment [constr] StartX=32.5 StartY=-45.5 StartZ=0 EndX=45.5 EndY=-45.5 EndZ=0
    g17: Circle CenterX=58.5 CenterY=-45.5 CenterZ=0 NormalX=0 NormalY=0 NormalZ=1 AngleXU=0 Radius=2.55
    g18: LineSegment [constr] StartX=45.5 StartY=-45.5 StartZ=0 EndX=58.5 EndY=-45.5 EndZ=0
    g19: Circle CenterX=-80.7 CenterY=-12 CenterZ=0 NormalX=0 NormalY=0 NormalZ=1 AngleXU=0 Radius=2.6
    g20: Circle CenterX=-80.7 CenterY=-21 CenterZ=0 NormalX=0 NormalY=0 NormalZ=1 AngleXU=0 Radius=2.6
    g21: LineSegment [constr] StartX=-80.7 StartY=-12 StartZ=0 EndX=-80.7 EndY=-21 EndZ=0
    g22: Circle CenterX=-80.7 CenterY=-30 CenterZ=0 NormalX=0 NormalY=0 NormalZ=1 AngleXU=0 Radius=2.6
    g23: LineSegment [constr] StartX=-80.7 StartY=-21 StartZ=0 EndX=-80.7 EndY=-30 EndZ=0
    g24: Circle CenterX=80.7 CenterY=-12 CenterZ=0 NormalX=0 NormalY=0 NormalZ=1 AngleXU=0 Radius=2.6
    g25: Circle CenterX=80.7 CenterY=-21 CenterZ=0 NormalX=0 NormalY=0 NormalZ=1 AngleXU=0 Radius=2.6
    g26: LineSegment [constr] StartX=80.7 StartY=-12 StartZ=0 EndX=80.7 EndY=-21 EndZ=0
    g27: Circle CenterX=80.7 CenterY=-30 CenterZ=0 NormalX=0 NormalY=0 NormalZ=1 AngleXU=0 Radius=2.6
    g28: LineSegment [constr] StartX=80.7 StartY=-21 StartZ=0 EndX=80.7 EndY=-30 EndZ=0
  constraints (74):
    c: Diameter(g0) = 5.1
    c: Equal(g0,g1) = 5.1
    c: Coincident(g0,g2)
    c: Coincident(g1,g2)
    c: Distance(g2) = 13
    c: Angle(g2) = 0
    c: Equal(g0,g3) = 5.1
    c: Coincident(g1,g4)
    c: Coincident(g3,g4)
    c: Equal(g2,g4)
    c: Parallel(g4,g2)
    c: Equal(g0,g5) = 5.1
    c: Coincident(g3,g6)
    c: Coincident(g5,g6)
    c: Equal(g2,g6)
    c: Parallel(g6,g2)
    c: Equal(g0,g7) = 5.1
    c: Coincident(g5,g8)
    c: Coincident(g7,g8)
    c: Equal(g2,g8)
    c: Parallel(g8,g2)
    c: Equal(g0,g9) = 5.1
    c: Coincident(g7,g10)
    c: Coincident(g9,g10)
    c: Equal(g2,g10)
    c: Parallel(g10,g2)
    c: Equal(g0,g11) = 5.1
    c: Coincident(g9,g12)
    c: Coincident(g11,g12)
    c: Equal(g2,g12)
    c: Parallel(g12,g2)
    c: Equal(g0,g13) = 5.1
    c: Coincident(g11,g14)
    c: Coincident(g13,g14)
    c: Equal(g2,g14)
    c: Parallel(g14,g2)
    c: Equal(g0,g15) = 5.1
    c: Coincident(g13,g16)
    c: Coincident(g15,g16)
    c: Equal(g2,g16)
    c: Parallel(g16,g2)
    c: Equal(g0,g17) = 5.1
    c: Coincident(g15,g18)
    c: Coincident(g17,g18)
    c: Equal(g2,g18)
    c: Parallel(g18,g2)
    c: DistanceX(g17,g-5) = 36
    c: DistanceY(g-5,g17) = 7.5
    c: Diameter(g19) = 5.2
    c: DistanceY(g-5,g19) = 41
    c: DistanceX(g-5,g19) = 13.8
    c: Equal(g19,g20) = 5.2
    c: Coincident(g19,g21)
    c: Coincident(g20,g21)
    c: Distance(g21) = 9
    c: Angle(g21) = -1.5708
    c: Equal(g19,g22) = 5.2
    c: Coincident(g20,g23)
    c: Coincident(g22,g23)
    c: Equal(g21,g23)
    c: Parallel(g23,g21)
    c: DistanceX(g24,g-5) = 13.8
    c: DistanceY(g-5,g24) = 41
    c: Coincident(g24,g26)
    c: Coincident(g25,g26)
    c: Distance(g26) = 9
    c: Angle(g26) = -1.5708
    c: Coincident(g25,g28)
    c: Coincident(g27,g28)
    c: Equal(g26,g28)
    c: Parallel(g28,g26)
    c: Equal(g19,g24)
    c: Equal(g24,g25)
    c: Equal(g25,g27)
FEATURE [PartDesign::Pocket] Pocket004  label="ledholes"
  BaseFeature = -> Pocket003
  Length = 5
  Length2 = 100
  Profile = -> Sketch017
  Type = 1
FEATURE [PartDesign::Fillet] Fillet
  Base = -> Pocket004 [Edge12,Edge41,Edge50,Edge11]
  BaseFeature = -> Pocket004
  Radius = 2.5
FEATURE [PartDesign::Fillet] Fillet005
  Base = -> Fillet [Edge156]
  BaseFeature = -> Fillet
  Radius = 5
FEATURE [PartDesign::Fillet] Fillet006
  Base = -> Fillet005 [Edge119,Edge117,Edge129,Edge121,Edge127,Edge125,Edge123,Edge47]
  BaseFeature = -> Fillet005
  Radius = 1
FEATURE [Sketcher::SketchObject] Sketch018
  MapMode = 5
  Placement = pos=(0,0,-9.5) rot=(1,0,0;3.14159rad)
  Support = -> [Fillet006]
  sketch-geometry (10):
    g0: LineSegment StartX=-87 StartY=-5 StartZ=0 EndX=-87 EndY=-35.5 EndZ=0
    g1: LineSegment StartX=-87 StartY=-35.5 StartZ=0 EndX=-72.5 EndY=-50 EndZ=0
    g2: LineSegment StartX=-72.5 StartY=-50 StartZ=0 EndX=72.5 EndY=-50 EndZ=0
    g3: LineSegment StartX=72.5 StartY=-50 StartZ=0 EndX=87 EndY=-35.5 EndZ=0
    g4: LineSegment StartX=87 StartY=-35.5 StartZ=0 EndX=87 EndY=-5 EndZ=0
    g5: LineSegment StartX=87 StartY=-5 StartZ=0 EndX=70 EndY=-5 EndZ=0
    g6: LineSegment StartX=70 StartY=-5 StartZ=0 EndX=70 EndY=-39 EndZ=0
    g7: LineSegment StartX=70 StartY=-39 StartZ=0 EndX=-70 EndY=-39 EndZ=0
    g8: LineSegment StartX=-70 StartY=-39 StartZ=0 EndX=-70 EndY=-5 EndZ=0
    g9: LineSegment StartX=-70 StartY=-5 StartZ=0 EndX=-87 EndY=-5 EndZ=0
  constraints (27):
    c: Vertical(g0)
    c: Coincident(g0,g1)
    c: Coincident(g1,g2)
    c: Coincident(g2,g3)
    c: Coincident(g3,g4)
    c: Coincident(g4,g5)
    c: Coincident(g5,g6)
    c: Coincident(g6,g7)
    c: Coincident(g7,g8)
    c: Vertical(g8)
    c: Coincident(g8,g9)
    c: Coincident(g9,g0)
    c: Horizontal(g9)
    c: Horizontal(g5)
    c: Symmetric(g4,g0,g-2)
    c: DistanceX(g0,g4) = 174
    c: Equal(g5,g9)
    c: DistanceX(g9,g9) = 17
    c: DistanceY(g1) = -50
    c: Angle(g1) = -0.785398
    c: Angle(g3) = 0.785398
    c: Symmetric(g7,g6,g-2)
    c: DistanceY(g6,g-1) = 39
    c: DistanceY(g8) = -5
    c: Equal(g1,g3)
    c: Symmetric(g1,g2,g-2)
    c: DistanceX(g2,g2) = 145
FEATURE [PartDesign::Pocket] Pocket005  label="wireslots"
  BaseFeature = -> Fillet006
  Length = 3.5
  Length2 = 100
  Profile = -> Sketch018
  Type = 0
FEATURE [PartDesign::Fillet] Fillet007  label="phoneHolderBody"
  Base = -> Pocket005 [Edge239,Edge225]
  BaseFeature = -> Pocket005
  Radius = 3
FEATURE [PartDesign::Body] Body007  label="phoneHolderTop"
  Group = -> [Sketch011,Pad010,Sketch012,Pad011,Sketch013,Pocket,Sketch014,Pocket001,Sketch015,Pocket002,Sketch016,Pocket003,Sketch017,Pocket004,Fillet,Fillet005,Fillet006,Sketch018,Pocket005,Fillet007]
  Origin = -> Origin007
  Placement = pos=(0,82,15) rot=(0,0,1;0rad)
  Tip = -> Fillet007
FEATURE [Sketcher::SketchObject] Sketch020
  MapMode = 5
  Support = -> [XY_Plane008]
  expr: Constraints[20] = data.phoneholder_sides_thickness * 2 + data.bluWin_width + 2 * data.phoneholder_ledpart_height
  expr: Constraints[21] = data.phoneholder_width
  sketch-geometry (22):
    g0: LineSegment StartX=-94.5 StartY=48 StartZ=0 EndX=-94.5 EndY=-48 EndZ=0
    g1: LineSegment StartX=-94.5 StartY=-48 StartZ=0 EndX=-41 EndY=-48 EndZ=0
    g2: LineSegment StartX=-41 StartY=-48 StartZ=0 EndX=-41 EndY=-73 EndZ=0
    g3: LineSegment StartX=-41 StartY=-73 StartZ=0 EndX=-15 EndY=-73 EndZ=0
    g4: LineSegment StartX=-15 StartY=-73 StartZ=0 EndX=-15 EndY=-48 EndZ=0
    g5: LineSegment StartX=-15 StartY=-48 StartZ=0 EndX=15 EndY=-48 EndZ=0
    g6: LineSegment StartX=15 StartY=-48 StartZ=0 EndX=15 EndY=-73 EndZ=0
    g7: LineSegment StartX=15 StartY=-73 StartZ=0 EndX=41 EndY=-73 EndZ=0
    g8: LineSegment StartX=41 StartY=-73 StartZ=0 EndX=41 EndY=-48 EndZ=0
    g9: LineSegment StartX=41 StartY=-48 StartZ=0 EndX=94.5 EndY=-48 EndZ=0
    g10: LineSegment StartX=94.5 StartY=-48 StartZ=0 EndX=94.5 EndY=48 EndZ=0
    g11: LineSegment StartX=94.5 StartY=48 StartZ=0 EndX=-94.5 EndY=48 EndZ=0
    g12: Circle CenterX=-28 CenterY=-58 CenterZ=0 NormalX=0 NormalY=0 NormalZ=1 AngleXU=0 Radius=3.5
    g13: Circle CenterX=28 CenterY=-58 CenterZ=0 NormalX=0 NormalY=0 NormalZ=1 AngleXU=0 Radius=3.5
    g14: Circle CenterX=-86.5 CenterY=-42 CenterZ=0 NormalX=0 NormalY=0 NormalZ=1 AngleXU=0 Radius=1.75
    g15: Circle CenterX=86.5 CenterY=-42 CenterZ=0 NormalX=0 NormalY=0 NormalZ=1 AngleXU=0 Radius=1.75
    g16: Circle CenterX=86.5 CenterY=42 CenterZ=0 NormalX=0 NormalY=0 NormalZ=1 AngleXU=0 Radius=1.75
    g17: Circle CenterX=-86.5 CenterY=42 CenterZ=0 NormalX=0 NormalY=0 NormalZ=1 AngleXU=0 Radius=1.75
    g18: LineSegment StartX=-90.5 StartY=38 StartZ=0 EndX=-80.5 EndY=38 EndZ=0
    g19: LineSegment StartX=-80.5 StartY=38 StartZ=0 EndX=-80.5 EndY=-2 EndZ=0
    g20: LineSegment StartX=-80.5 StartY=-2 StartZ=0 EndX=-90.5 EndY=-2 EndZ=0
    g21: LineSegment StartX=-90.5 StartY=-2 StartZ=0 EndX=-90.5 EndY=38 EndZ=0
  constraints (58):
    c: Coincident(g0,g1)
    c: Horizontal(g1)
    c: Coincident(g1,g2)
    c: Vertical(g2)
    c: Coincident(g2,g3)
    c: Horizontal(g3)
    c: Coincident(g3,g4)
    c: Vertical(g4)
    c: Coincident(g4,g5)
    c: Coincident(g5,g6)
    c: Vertical(g6)
    c: Coincident(g6,g7)
    c: Coincident(g7,g8)
    c: Vertical(g8)
    c: Coincident(g8,g9)
    c: Horizontal(g9)
    c: Coincident(g9,g10)
    c: Vertical(g10)
    c: Coincident(g10,g11)
    c: Coincident(g11,g0)
    c: DistanceY(g0,g0) = 96
    c: DistanceX(g11,g11) = 189
    c: Equal(g2,g4)
    c: Equal(g4,g6)
    c: Equal(g6,g8)
    c: Symmetric(g0,g10,g-2)
    c: Symmetric(g12,g13,g-2)
    c: DistanceX(g12,g13) = 56
    c: DistanceY(g13,g8) = 10
    c: Symmetric(g5,g4,g-2)
    c: DistanceX(g5,g5) = 30
    c: DistanceX(g2,g7) = 82
    c: Symmetric(g2,g7,g-2)
    c: DistanceY(g7,g13) = 15
    c: Diameter(g13) = 7
    c: Equal(g12,g13)
    c: Symmetric(g0,g0,g-1)
    c: Equal(g15,g14)
    c: Equal(g14,g17)
    c: Equal(g17,g16)
    c: Symmetric(g17,g16,g-2)
    c: Symmetric(g17,g14,g-1)
    c: Symmetric(g14,g15,g-2)
    c: Diameter(g17) = 3.5
    c: DistanceX(g16,g10) = 8
    c: DistanceY(g16,g10) = 6
    c: Coincident(g18,g19)
    c: Coincident(g19,g20)
    c: Coincident(g20,g21)
    c: Coincident(g21,g18)
    c: Horizontal(g18)
    c: Horizontal(g20)
    c: Vertical(g19)
    c: Vertical(g21)
    c: DistanceX(g18,g18) = 10
    c: DistanceY(g18,g0) = 10
    c: DistanceX(g0,g18) = 4
    c: DistanceY(g21,g21) = 40
FEATURE [PartDesign::Pad] Pad012
  Length = 3
  Length2 = 100
  Profile = -> Sketch020
  Type = 0
FEATURE [PartDesign::Fillet] Fillet008
  Base = -> Pad012 [Edge29,Edge26,Edge23,Edge32,Edge17,Edge20,Edge14,Edge11,Edge8,Edge5,Edge2,Edge1]
  BaseFeature = -> Pad012
  Radius = 2.5
FEATURE [PartDesign::Fillet] Fillet009
  Base = -> Fillet008 [Edge66,Edge63,Edge64,Edge65]
  BaseFeature = -> Fillet008
  Radius = 1
FEATURE [PartDesign::Body] Body008  label="phoneHolderMountplate"
  Group = -> [Sketch020,Pad012,Fillet008,Fillet009]
  Origin = -> Origin008
  Placement = pos=(0,87,2.5) rot=(0,0,1;0rad)
  Tip = -> Fillet009
FEATURE [TechDraw::DrawSVGTemplate] Template
  Height = 210
  Orientation = 1
  Width = 297
FEATURE [TechDraw::DrawViewPart] View
  CoarseView = false
  Direction = (0,0,1)
  Focus = 100
  HardHidden = false
  IsoCount = 0
  IsoHidden = false
  IsoVisible = false
  LockPosition = false
  Perspective = false
  Rotation = 0
  Scale = 0.5
  ScaleType = 0
  SeamHidden = false
  SeamVisible = false
  SmoothHidden = false
  SmoothVisible = false
  Source = -> [Pad009]
  X = 168.265
  Y = 108.294
FEATURE [TechDraw::DrawViewDimension] Dimension
  Arbitrary = false
  FormatSpec = %.2f
  LockPosition = false
  MeasureType = 1
  OverTolerance = 0
  References2D = -> [View]
  Rotation = 0
  ScaleType = 0
  Type = 1
  UnderTolerance = 0
  X = -0.658836
  Y = 95.166
FEATURE [TechDraw::DrawViewDimension] Dimension001
  Arbitrary = false
  FormatSpec = %.2f
  LockPosition = false
  MeasureType = 1
  OverTolerance = 0
  References2D = -> [View]
  Rotation = 0
  ScaleType = 0
  Type = 2
  UnderTolerance = 0
  X = -149.589
  Y = -14.1471
FEATURE [TechDraw::DrawViewDimension] Dimension002
  Arbitrary = false
  FormatSpec = %.2f
  LockPosition = false
  MeasureType = 1
  OverTolerance = 0
  References2D = -> [View]
  Rotation = 0
  ScaleType = 0
  Type = 2
  UnderTolerance = 0
  X = -136.634
  Y = 14.6987
FEATURE [TechDraw::DrawViewDimension] Dimension004
  Arbitrary = false
  FormatSpec = %.2f
  LockPosition = false
  MeasureType = 1
  OverTolerance = 0
  References2D = -> [View]
  Rotation = 0
  ScaleType = 0
  Type = 2
  UnderTolerance = 0
  X = -136.063
  Y = -40.0981
FEATURE [TechDraw::DrawViewDimension] Dimension005
  Arbitrary = false
  FormatSpec = ⌀%.2f
  LockPosition = false
  MeasureType = 1
  OverTolerance = 0
  References2D = -> [View]
  Rotation = 0
  ScaleType = 0
  Type = 5
  UnderTolerance = 0
  X = -1.02816
  Y = -60.0685
FEATURE [TechDraw::DrawViewDimension] Dimension006
  Arbitrary = false
  FormatSpec = ⌀%.2f
  LockPosition = false
  MeasureType = 1
  OverTolerance = 0
  References2D = -> [View]
  Rotation = 0
  ScaleType = 0
  Type = 5
  UnderTolerance = 0
  X = -42.3882
  Y = -57.6337
FEATURE [TechDraw::DrawViewDimension] Dimension007
  Arbitrary = false
  FormatSpec = %.2f
  LockPosition = false
  MeasureType = 1
  OverTolerance = 0
  References2D = -> [View]
  Rotation = 0
  ScaleType = 0
  Type = 2
  UnderTolerance = 0
  X = -149.339
  Y = 36.4934
FEATURE [TechDraw::DrawViewDimension] Dimension008
  Arbitrary = false
  FormatSpec = %.2f
  LockPosition = false
  MeasureType = 1
  OverTolerance = 0
  References2D = -> [View]
  Rotation = 0
  ScaleType = 0
  Type = 1
  UnderTolerance = 0
  X = -85.1941
  Y = 87.26
FEATURE [TechDraw::DrawViewDimension] Dimension009
  Arbitrary = false
  FormatSpec = %.2f
  LockPosition = false
  MeasureType = 1
  OverTolerance = 0
  References2D = -> [View]
  Rotation = 0
  ScaleType = 0
  Type = 1
  UnderTolerance = 0
  X = -42.5587
  Y = 87.2421
FEATURE [TechDraw::DrawViewDimension] Dimension010
  Arbitrary = false
  FormatSpec = %.2f
  LockPosition = false
  MeasureType = 1
  OverTolerance = 0
  References2D = -> [View]
  Rotation = 0
  ScaleType = 0
  Type = 1
  UnderTolerance = 0
  X = 0.658836
  Y = 87.2242
FEATURE [TechDraw::DrawViewDimension] Dimension011
  Arbitrary = false
  FormatSpec = %.2f
  LockPosition = false
  MeasureType = 1
  OverTolerance = 0
  References2D = -> [View]
  Rotation = 0
  ScaleType = 0
  Type = 1
  UnderTolerance = 0
  X = -90.9206
  Y = 11.2411
FEATURE [TechDraw::DrawViewDimension] Dimension012
  Arbitrary = false
  FormatSpec = %.2f
  LockPosition = false
  MeasureType = 1
  OverTolerance = 0
  References2D = -> [View]
  Rotation = 0
  ScaleType = 0
  Type = 2
  UnderTolerance = 0
  X = -125.347
  Y = -9.20582
FEATURE [TechDraw::DrawViewDimension] Dimension013
  Arbitrary = false
  FormatSpec = %.2f
  LockPosition = false
  MeasureType = 1
  OverTolerance = 0
  References2D = -> [View]
  Rotation = 0
  ScaleType = 0
  Type = 2
  UnderTolerance = 0
  X = 4.94127
  Y = -29.7383
FEATURE [TechDraw::DrawViewDimension] Dimension015
  Arbitrary = false
  FormatSpec = %.2f
  LockPosition = false
  MeasureType = 1
  OverTolerance = 0
  References2D = -> [View]
  Rotation = 0
  ScaleType = 0
  Type = 2
  UnderTolerance = 0
  X = -8.3999
  Y = -38.0352
FEATURE [TechDraw::DrawViewDimension] Dimension016
  Arbitrary = false
  FormatSpec = %.2f
  LockPosition = false
  MeasureType = 1
  OverTolerance = 0
  References2D = -> [View]
  Rotation = 0
  ScaleType = 0
  Type = 2
  UnderTolerance = 0
  X = -65.8825
  Y = -38.6147
FEATURE [TechDraw::DrawViewDimension] Dimension017
  Arbitrary = false
  FormatSpec = %.2f
  LockPosition = false
  MeasureType = 1
  OverTolerance = 0
  References2D = -> [View]
  Rotation = 0
  ScaleType = 0
  Type = 1
  UnderTolerance = 0
  X = 63.4295
  Y = 48.6632
FEATURE [TechDraw::DrawViewDimension] Dimension018
  Arbitrary = false
  FormatSpec = %.2f
  LockPosition = false
  MeasureType = 1
  OverTolerance = 0
  References2D = -> [View]
  Rotation = 0
  ScaleType = 0
  Type = 1
  UnderTolerance = 0
  X = 10.6236
  Y = 28.3092
FEATURE [TechDraw::DrawViewDimension] Dimension019
  Arbitrary = false
  FormatSpec = %.2f
  LockPosition = false
  MeasureType = 1
  OverTolerance = 0
  References2D = -> [View]
  Rotation = 0
  ScaleType = 0
  Type = 1
  UnderTolerance = 0
  X = 21.1795
  Y = 35.5447
FEATURE [TechDraw::DrawViewDimension] Dimension021
  Arbitrary = false
  FormatSpec = ⌀%.2f
  LockPosition = false
  MeasureType = 1
  OverTolerance = 0
  References2D = -> [View]
  Rotation = 0
  ScaleType = 0
  Type = 5
  UnderTolerance = 0
  X = -1.97651
  Y = -10.5414
FEATURE [TechDraw::DrawViewDimension] Dimension022
  Arbitrary = false
  FormatSpec = %.2f
  LockPosition = false
  MeasureType = 1
  OverTolerance = 0
  References2D = -> [View]
  Rotation = 0
  ScaleType = 0
  Type = 1
  UnderTolerance = 0
  X = -80.844
  Y = 1.36466
FEATURE [TechDraw::DrawViewDimension] Dimension024
  Arbitrary = false
  FormatSpec = %.2f
  LockPosition = false
  MeasureType = 1
  OverTolerance = 0
  References2D = -> [View]
  Rotation = 0
  ScaleType = 0
  Type = 1
  UnderTolerance = 0
  X = -38.8177
  Y = 26.071
FEATURE [TechDraw::DrawViewDimension] Dimension025
  Arbitrary = false
  FormatSpec = %.2f
  LockPosition = false
  MeasureType = 1
  OverTolerance = 0
  References2D = -> [View]
  Rotation = 0
  ScaleType = 0
  Type = 2
  UnderTolerance = 0
  X = -42.6885
  Y = -16.6706
FEATURE [TechDraw::DrawViewDimension] Dimension026
  Arbitrary = false
  FormatSpec = %.2f
  LockPosition = false
  MeasureType = 1
  OverTolerance = 0
  References2D = -> [View]
  Rotation = 0
  ScaleType = 0
  Type = 2
  UnderTolerance = 0
  X = -52.7058
  Y = -16.5794
FEATURE [TechDraw::DrawViewDimension] Dimension027
  Arbitrary = false
  FormatSpec = %.2f
  LockPosition = false
  MeasureType = 1
  OverTolerance = 0
  References2D = -> [View]
  Rotation = 0
  ScaleType = 0
  Type = 2
  UnderTolerance = 0
  X = -59.9362
  Y = -6.33555
FEATURE [TechDraw::DrawViewDimension] Dimension028
  Arbitrary = false
  FormatSpec = %.2f
  LockPosition = false
  MeasureType = 1
  OverTolerance = 0
  References2D = -> [View]
  Rotation = 0
  ScaleType = 0
  Type = 2
  UnderTolerance = 0
  X = -32.8524
  Y = -18.0587
FEATURE [TechDraw::DrawViewDimension] Dimension029
  Arbitrary = false
  FormatSpec = %.2f
  LockPosition = false
  MeasureType = 1
  OverTolerance = 0
  References2D = -> [View]
  Rotation = 0
  ScaleType = 0
  Type = 2
  UnderTolerance = 0
  X = -24.212
  Y = -17.3177
FEATURE [TechDraw::DrawViewDimension] Dimension030
  Arbitrary = false
  FormatSpec = %.2f
  LockPosition = false
  MeasureType = 1
  OverTolerance = 0
  References2D = -> [View]
  Rotation = 0
  ScaleType = 0
  Type = 1
  UnderTolerance = 0
  X = 33.6001
  Y = 42.8831
FEATURE [TechDraw::DrawViewDimension] Dimension031
  Arbitrary = false
  FormatSpec = %.2f
  LockPosition = false
  MeasureType = 1
  OverTolerance = 0
  References2D = -> [View]
  Rotation = 0
  ScaleType = 0
  Type = 1
  UnderTolerance = 0
  X = 69.2058
  Y = -59.93
FEATURE [TechDraw::DrawViewDimension] Dimension032
  Arbitrary = false
  FormatSpec = %.2f
  LockPosition = false
  MeasureType = 1
  OverTolerance = 0
  References2D = -> [View]
  Rotation = 0
  ScaleType = 0
  Type = 1
  UnderTolerance = 0
  X = 94.3501
  Y = 2.55873
FEATURE [TechDraw::DrawViewDimension] Dimension033
  Arbitrary = false
  FormatSpec = %.2f
  LockPosition = false
  MeasureType = 1
  OverTolerance = 0
  References2D = -> [View]
  Rotation = 0
  ScaleType = 0
  Type = 1
  UnderTolerance = 0
  X = 37.8026
  Y = 2.55873
FEATURE [TechDraw::DrawViewDimension] Dimension034
  Arbitrary = false
  FormatSpec = %.2f
  LockPosition = false
  MeasureType = 1
  OverTolerance = 0
  References2D = -> [View]
  Rotation = 0
  ScaleType = 0
  Type = 2
  UnderTolerance = 0
  X = 76.0061
  Y = -19.9323
FEATURE [TechDraw::DrawViewDimension] Dimension035
  Arbitrary = false
  FormatSpec = %.2f
  LockPosition = false
  MeasureType = 1
  OverTolerance = 0
  References2D = -> [View]
  Rotation = 0
  ScaleType = 0
  Type = 2
  UnderTolerance = 0
  X = 36.5884
  Y = -37.6706
FEATURE [TechDraw::DrawViewDimension] Dimension036
  Arbitrary = false
  FormatSpec = %.2f
  LockPosition = false
  MeasureType = 1
  OverTolerance = 0
  References2D = -> [View]
  Rotation = 0
  ScaleType = 0
  Type = 2
  UnderTolerance = 0
  X = 21.1057
  Y = -16.2411
FEATURE [TechDraw::DrawViewDimension] Dimension037
  Arbitrary = false
  FormatSpec = %.2f
  LockPosition = false
  MeasureType = 1
  OverTolerance = 0
  References2D = -> [View]
  Rotation = 0
  ScaleType = 0
  Type = 2
  UnderTolerance = 0
  X = -160.649
  Y = -2.96476
FEATURE [Sketcher::SketchObject] Sketch021
  MapMode = 5
  Support = -> [XY_Plane009]
  expr: Constraints[39] = data.seg7_length + 1
  expr: Constraints[24] = data.seg7_length_all
  expr: Constraints[11] = data.max8x8_width + 1
  expr: Constraints[60] = data.max8x8_length
  sketch-geometry (41):
    g0: LineSegment StartX=-90 StartY=-38.5 StartZ=0 EndX=-90 EndY=17.5 EndZ=0
    g1: LineSegment StartX=90 StartY=17.5 StartZ=0 EndX=90 EndY=-38.5 EndZ=0
    g2: LineSegment StartX=90 StartY=-38.5 StartZ=0 EndX=-90 EndY=-38.5 EndZ=0
    g3: LineSegment StartX=-16.5 StartY=16.5 StartZ=0 EndX=16.5 EndY=16.5 EndZ=0
    g4: LineSegment StartX=16.5 StartY=16.5 StartZ=0 EndX=16.5 EndY=-16.5 EndZ=0
    g5: LineSegment StartX=16.5 StartY=-16.5 StartZ=0 EndX=-16.5 EndY=-16.5 EndZ=0
    g6: LineSegment StartX=-16.5 StartY=-16.5 StartZ=0 EndX=-16.5 EndY=16.5 EndZ=0
    g7: LineSegment [constr] StartX=-89 StartY=-20.5 StartZ=0 EndX=-6.7 EndY=-20.5 EndZ=0
    g8: LineSegment [constr] StartX=-6.7 StartY=-20.5 StartZ=0 EndX=-6.7 EndY=-36 EndZ=0
    g9: LineSegment [constr] StartX=-6.7 StartY=-36 StartZ=0 EndX=-89 EndY=-36 EndZ=0
    g10: LineSegment [constr] StartX=-89 StartY=-36 StartZ=0 EndX=-89 EndY=-20.5 EndZ=0
    g11: LineSegment StartX=-76 StartY=-20.5 StartZ=0 EndX=-14 EndY=-20.5 EndZ=0
    g12: LineSegment StartX=-14 StartY=-20.5 StartZ=0 EndX=-14 EndY=-35 EndZ=0
    g13: LineSegment StartX=-14 StartY=-35 StartZ=0 EndX=-76 EndY=-35 EndZ=0
    g14: LineSegment StartX=-76 StartY=-35 StartZ=0 EndX=-76 EndY=-20.5 EndZ=0
    g15: LineSegment StartX=14 StartY=-20.5 StartZ=0 EndX=76 EndY=-20.5 EndZ=0
    g16: LineSegment StartX=76 StartY=-20.5 StartZ=0 EndX=76 EndY=-35 EndZ=0
    g17: LineSegment StartX=76 StartY=-35 StartZ=0 EndX=14 EndY=-35 EndZ=0
    g18: LineSegment StartX=14 StartY=-35 StartZ=0 EndX=14 EndY=-20.5 EndZ=0
    g19: LineSegment [constr] StartX=16.5 StartY=16.5 StartZ=0 EndX=-33.5 EndY=16.5 EndZ=0
    g20: LineSegment [constr] StartX=-33.5 StartY=16.5 StartZ=0 EndX=-33.5 EndY=-16.5 EndZ=0
    g21: LineSegment [constr] StartX=-33.5 StartY=-16.5 StartZ=0 EndX=16.5 EndY=-16.5 EndZ=0
    g22: LineSegment [constr] StartX=16.5 StartY=-16.5 StartZ=0 EndX=16.5 EndY=16.5 EndZ=0
    g23: Circle CenterX=-45 CenterY=2.5 CenterZ=0 NormalX=0 NormalY=0 NormalZ=1 AngleXU=0 Radius=2.55
    g24: Circle CenterX=-45 CenterY=-5 CenterZ=0 NormalX=0 NormalY=0 NormalZ=1 AngleXU=0 Radius=2.55
    g25: Circle CenterX=-45 CenterY=-12.5 CenterZ=0 NormalX=0 NormalY=0 NormalZ=1 AngleXU=0 Radius=2.55
    g26: Circle CenterX=-45 CenterY=20.135 CenterZ=0 NormalX=0 NormalY=0 NormalZ=1 AngleXU=0 Radius=2.55
    g27: Circle CenterX=-35 CenterY=21.9216 CenterZ=0 NormalX=0 NormalY=0 NormalZ=1 AngleXU=0 Radius=2.55
    g28: Circle CenterX=-25 CenterY=23.2522 CenterZ=0 NormalX=0 NormalY=0 NormalZ=1 AngleXU=0 Radius=2.55
    g29: Circle CenterX=-15 CenterY=24.135 CenterZ=0 NormalX=0 NormalY=0 NormalZ=1 AngleXU=0 Radius=2.55
    g30: Circle CenterX=-5 CenterY=24.575 CenterZ=0 NormalX=0 NormalY=0 NormalZ=1 AngleXU=0 Radius=2.55
    g31: Circle CenterX=5 CenterY=24.575 CenterZ=0 NormalX=0 NormalY=0 NormalZ=1 AngleXU=0 Radius=2.55
    g32: Circle CenterX=15 CenterY=24.135 CenterZ=0 NormalX=0 NormalY=0 NormalZ=1 AngleXU=0 Radius=2.55
    g33: Circle CenterX=25 CenterY=23.2522 CenterZ=0 NormalX=0 NormalY=0 NormalZ=1 AngleXU=0 Radius=2.55
    g34: Circle CenterX=35 CenterY=21.9216 CenterZ=0 NormalX=0 NormalY=0 NormalZ=1 AngleXU=0 Radius=2.55
    g35: Circle CenterX=45 CenterY=20.135 CenterZ=0 NormalX=0 NormalY=0 NormalZ=1 AngleXU=0 Radius=2.55
    g36: ArcOfCircle [constr] CenterX=1.18e-14 CenterY=-202.87 CenterZ=0 NormalX=0 NormalY=0 NormalZ=1 AngleXU=0 Radius=227.5 StartAngle=1.37168 EndAngle=1.76991
    g37: Circle CenterX=45 CenterY=2.5 CenterZ=0 NormalX=0 NormalY=0 NormalZ=1 AngleXU=0 Radius=2.55
    g38: Circle CenterX=45 CenterY=-12.5 CenterZ=0 NormalX=0 NormalY=0 NormalZ=1 AngleXU=0 Radius=2.55
    g39: Circle CenterX=45 CenterY=-5 CenterZ=0 NormalX=0 NormalY=0 NormalZ=1 AngleXU=0 Radius=2.55
    g40: ArcOfCircle CenterX=9.2e-15 CenterY=-285.23 CenterZ=0 NormalX=0 NormalY=0 NormalZ=1 AngleXU=0 Radius=315.825 StartAngle=1.28182 EndAngle=1.85977
  constraints (110):
    c: Coincident(g1,g2)
    c: Coincident(g2,g0)
    c: Coincident(g3,g4)
    c: Coincident(g4,g5)
    c: Coincident(g5,g6)
    c: Coincident(g6,g3)
    c: Symmetric(g3,g3,g-2)
    c: Symmetric(g5,g3,g-1)
    c: Equal(g3,g6)
    c: Equal(g6,g5)
    c: Equal(g5,g4)
    c: DistanceY(g4,g4) = 33
    c: DistanceX(g2,g2) = 180
    c: Symmetric(g0,g1,g-2)
    c: Symmetric(g0,g1,g-2)
    c: DistanceY(g0,g5) = 22
    c: Coincident(g7,g8)
    c: Coincident(g8,g9)
    c: Coincident(g9,g10)
    c: Coincident(g10,g7)
    c: Horizontal(g7)
    c: Horizontal(g9)
    c: Vertical(g8)
    c: Vertical(g10)
    c: DistanceX(g7,g7) = 82.3
    c: DistanceY(g10,g10) = 15.5
    c: Vertical(g0)
    c: DistanceY(g1,g1) = 56
    c: Coincident(g11,g12)
    c: Coincident(g12,g13)
    c: Coincident(g13,g14)
    c: Coincident(g14,g11)
    c: Horizontal(g11)
    c: Horizontal(g13)
    c: Vertical(g12)
    c: Vertical(g14)
    c: DistanceY(g14,g14) = 14.5
    c: PointOnObject(g11,g7)
    c: DistanceX(g9,g13) = 13
    c: DistanceX(g13,g13) = 62
    c: Coincident(g15,g16)
    c: Coincident(g16,g17)
    c: Coincident(g17,g18)
    c: Coincident(g18,g15)
    c: Horizontal(g15)
    c: Horizontal(g17)
    c: Vertical(g16)
    c: Vertical(g18)
    c: Equal(g12,g18)
    c: Equal(g11,g15)
    c: Symmetric(g26,g35,g-2)
    c: Coincident(g19,g20)
    c: Coincident(g20,g21)
    c: Coincident(g21,g22)
    c: Coincident(g22,g19)
    c: Horizontal(g19)
    c: Horizontal(g21)
    c: Vertical(g20)
    c: Coincident(g19,g3)
    c: Coincident(g21,g4)
    c: DistanceX(g21,g21) = 50
    c: Equal(g25,g24)
    c: Equal(g24,g23)
    c: Diameter(g24) = 5.1
    c: DistanceX(g0,g23) = 45
    c: Diameter(g26) = 5.1
    c: Coincident(g36,g26)
    c: Coincident(g36,g35)
    c: PointOnObject(g28,g36)
    c: PointOnObject(g29,g36)
    c: PointOnObject(g30,g36)
    c: PointOnObject(g34,g36)
    c: Symmetric(g31,g30,g-2)
    c: Symmetric(g29,g32,g-2)
    c: Symmetric(g28,g33,g-2)
    c: Symmetric(g27,g34,g-2)
    c: Equal(g26,g27)
    c: Equal(g27,g28)
    c: Equal(g28,g29)
    c: Equal(g29,g30)
    c: Equal(g30,g31)
    c: Equal(g31,g32)
    c: Equal(g32,g33)
    c: Equal(g33,g34)
    c: Equal(g34,g35)
    c: DistanceX(g30,g31) = 10
    c: DistanceX(g29,g32) = 30
    c: DistanceX(g28,g33) = 50
    c: DistanceX(g27,g34) = 70
    c: Diameter(g36) = 455
    c: DistanceX(g26,g35) = 90
    c: Equal(g24,g37)
    c: Equal(g37,g39)
    c: Equal(g39,g38)
    c: Symmetric(g23,g37,g-2)
    c: Symmetric(g24,g39,g-2)
    c: Symmetric(g38,g25,g-2)
    c: DistanceY(g23,g0) = 15
    c: Vertical(g24,g25)
    c: Vertical(g25,g23)
    c: DistanceY(g24,g23) = 7.5
    c: DistanceY(g25,g24) = 7.5
    c: Coincident(g40,g0)
    c: Coincident(g40,g1)
    c: DistanceY(g36) = -202.87
    c: DistanceY(g40) = -285.23
    c: DistanceX(g12) = -14
    c: DistanceX(g17) = 14
    c: Horizontal(g11,g15)
    c: DistanceY(g15,g4) = 4
FEATURE [PartDesign::Pad] Pad013
  Length = 17
  Length2 = 100
  Profile = -> Sketch021
  Type = 0
  expr: Length = data.smalldash_thickness
FEATURE [PartDesign::Fillet] Fillet010
  Base = -> Pad013 [Edge1,Edge8]
  BaseFeature = -> Pad013
  Radius = 30
FEATURE [PartDesign::Fillet] Fillet011
  Base = -> Fillet010 [Edge40,Edge3]
  BaseFeature = -> Fillet010
  Radius = 3
FEATURE [Sketcher::SketchObject] Sketch023  label="7seg_depth"
  ExternalGeometry = -> [Pad013]
  MapMode = 5
  Placement = pos=(0,0,0) rot=(1,0,0;3.14159rad)
  Support = -> [Pad013]
  expr: Constraints[10] = data.seg7_width_all + 4
  sketch-geometry (4):
    g0: LineSegment StartX=-89 StartY=36.5 StartZ=0 EndX=89 EndY=36.5 EndZ=0
    g1: LineSegment StartX=89 StartY=36.5 StartZ=0 EndX=89 EndY=17 EndZ=0
    g2: LineSegment StartX=89 StartY=17 StartZ=0 EndX=-89 EndY=17 EndZ=0
    g3: LineSegment StartX=-89 StartY=17 StartZ=0 EndX=-89 EndY=36.5 EndZ=0
  constraints (11):
    c: Coincident(g0,g1)
    c: Coincident(g1,g2)
    c: Coincident(g2,g3)
    c: Coincident(g3,g0)
    c: Horizontal(g2)
    c: Vertical(g1)
    c: Vertical(g3)
    c: Symmetric(g0,g0,g-2)
    c: DistanceY(g0,g-3) = 2
    c: DistanceX(g0,g-4) = 1
    c: DistanceY(g1,g1) = 19.5
FEATURE [PartDesign::Pocket] Pocket006  label="7segdepth"
  BaseFeature = -> Fillet011
  Length = 7.4
  Length2 = 100
  Profile = -> Sketch023
  Type = 0
  expr: Length = data.smalldash_thickness - data.seg7_height - data.smalldash_frontthickness
FEATURE [Sketcher::SketchObject] Sketch024
  ExternalGeometry = -> [Pocket006]
  MapMode = 5
  Placement = pos=(0,0,7.4) rot=(1,0,0;3.14159rad)
  Support = -> [Pocket006]
  sketch-geometry (4):
    g0: Circle CenterX=-82.5 CenterY=32.95 CenterZ=0 NormalX=0 NormalY=0 NormalZ=1 AngleXU=0 Radius=0.9
    g1: Circle CenterX=-6 CenterY=23.95 CenterZ=0 NormalX=0 NormalY=0 NormalZ=1 AngleXU=0 Radius=0.9
    g2: Circle CenterX=9.7 CenterY=23.95 CenterZ=0 NormalX=0 NormalY=0 NormalZ=1 AngleXU=0 Radius=0.9
    g3: Circle CenterX=86.2 CenterY=32.95 CenterZ=0 NormalX=0 NormalY=0 NormalZ=1 AngleXU=0 Radius=0.9
  constraints (12):
    c: Equal(g0,g1)
    c: Equal(g1,g2)
    c: Equal(g2,g3)
    c: DistanceY(g2,g3) = 9
    c: DistanceY(g-4,g2) = 3.45
    c: Radius(g0) = 0.9
    c: DistanceX(g2,g3) = 76.5
    c: DistanceX(g2) = 9.7
    c: DistanceX(g1) = -6
    c: DistanceX(g0,g1) = 76.5
    c: Horizontal(g1,g2)
    c: Horizontal(g3,g0)
FEATURE [PartDesign::Pocket] Pocket007  label="7segholes"
  BaseFeature = -> Pocket006
  Length = 6
  Length2 = 100
  Profile = -> Sketch024
  Type = 0
FEATURE [Sketcher::SketchObject] Sketch025
  ExternalGeometry = -> [Pocket007]
  MapMode = 5
  Placement = pos=(0,0,0) rot=(1,0,0;3.14159rad)
  Support = -> [Pocket007]
  sketch-geometry (4):
    g0: LineSegment StartX=-36 StartY=17 StartZ=0 EndX=36 EndY=17 EndZ=0
    g1: LineSegment StartX=36 StartY=17 StartZ=0 EndX=36 EndY=-17 EndZ=0
    g2: LineSegment StartX=36 StartY=-17 StartZ=0 EndX=-36 EndY=-17 EndZ=0
    g3: LineSegment StartX=-36 StartY=-17 StartZ=0 EndX=-36 EndY=17 EndZ=0
  constraints (11):
    c: Coincident(g0,g1)
    c: Coincident(g1,g2)
    c: Coincident(g2,g3)
    c: Coincident(g3,g0)
    c: Horizontal(g2)
    c: Vertical(g3)
    c: Symmetric(g0,g0,g-2)
    c: Vertical(g1)
    c: DistanceX(g0,g0) = 72
    c: DistanceY(g1,g1) = 34
    c: PointOnObject(g0,g-3)
FEATURE [PartDesign::Pocket] Pocket008  label="8x8basicdepth"
  BaseFeature = -> Pocket007
  Length = 3
  Length2 = 100
  Profile = -> Sketch025
  Type = 0
  expr: Length = data.smalldash_thickness - data.max8x8_height - data.smalldash_frontthickness
FEATURE [Sketcher::SketchObject] Sketch029
  MapMode = 5
  Placement = pos=(0,0,3) rot=(1,0,0;3.14159rad)
  Support = -> [Pocket008]
  sketch-geometry (12):
    g0: LineSegment StartX=-27 StartY=17 StartZ=0 EndX=-27 EndY=10 EndZ=0
    g1: LineSegment StartX=-27 StartY=10 StartZ=0 EndX=-34 EndY=10 EndZ=0
    g2: LineSegment StartX=-34 StartY=10 StartZ=0 EndX=-34 EndY=-10 EndZ=0
    g3: LineSegment StartX=-34 StartY=-10 StartZ=0 EndX=-27 EndY=-10 EndZ=0
    g4: LineSegment StartX=-27 StartY=-10 StartZ=0 EndX=-27 EndY=-17 EndZ=0
    g5: LineSegment StartX=-27 StartY=-17 StartZ=0 EndX=27 EndY=-17 EndZ=0
    g6: LineSegment StartX=27 StartY=-17 StartZ=0 EndX=27 EndY=-10 EndZ=0
    g7: LineSegment StartX=27 StartY=-10 StartZ=0 EndX=34 EndY=-10 EndZ=0
    g8: LineSegment StartX=34 StartY=-10 StartZ=0 EndX=34 EndY=10 EndZ=0
    g9: LineSegment StartX=34 StartY=10 StartZ=0 EndX=27 EndY=10 EndZ=0
    g10: LineSegment StartX=27 StartY=10 StartZ=0 EndX=27 EndY=17 EndZ=0
    g11: LineSegment StartX=27 StartY=17 StartZ=0 EndX=-27 EndY=17 EndZ=0
  constraints (34):
    c: Vertical(g0)
    c: Coincident(g0,g1)
    c: Coincident(g1,g2)
    c: Coincident(g2,g3)
    c: Horizontal(g3)
    c: Coincident(g3,g4)
    c: Vertical(g4)
    c: Coincident(g4,g5)
    c: Horizontal(g5)
    c: Coincident(g5,g6)
    c: Vertical(g6)
    c: Coincident(g6,g7)
    c: Horizontal(g7)
    c: Coincident(g7,g8)
    c: Vertical(g8)
    c: Coincident(g8,g9)
    c: Horizontal(g9)
    c: Coincident(g9,g10)
    c: Vertical(g10)
    c: Coincident(g10,g11)
    c: Coincident(g11,g0)
    c: Symmetric(g0,g10,g-2)
    c: Horizontal(g1)
    c: Equal(g9,g10)
    c: Equal(g10,g7)
    c: Equal(g7,g6)
    c: Equal(g6,g4)
    c: Equal(g4,g3)
    c: Equal(g3,g1)
    c: Equal(g1,g0)
    c: DistanceX(g0) = -27
    c: DistanceY(g0,g0) = 7
    c: Symmetric(g0,g3,g-1)
    c: DistanceY(g10) = 17
FEATURE [PartDesign::Pocket] Pocket012
  BaseFeature = -> Pocket008
  Length = 10
  Length2 = 100
  Profile = -> Sketch029
  Type = 0
  expr: Length = data.max8x8_height - data.smalldash_frontthickness
FEATURE [Sketcher::SketchObject] Sketch028
  MapMode = 5
  Placement = pos=(0,0,0) rot=(1,0,0;3.14159rad)
  Support = -> [Pocket012]
  sketch-geometry (20):
    g0: LineSegment StartX=-84.2754 StartY=19.4749 StartZ=0 EndX=-84.2754 EndY=4.97301 EndZ=0
    g1: LineSegment StartX=-84.2754 StartY=4.97301 StartZ=0 EndX=-52.122 EndY=-24.8182 EndZ=0
    g2: LineSegment StartX=-52.122 StartY=-24.8182 StartZ=0 EndX=-29.7666 EndY=-27.9955 EndZ=0
    g3: LineSegment StartX=-29.7666 StartY=-27.9955 StartZ=0 EndX=-10.0595 EndY=-29.2176 EndZ=0
    g4: LineSegment StartX=-10.0595 StartY=-29.2176 StartZ=0 EndX=0 EndY=-29.2176 EndZ=0
    g5: LineSegment StartX=0 StartY=-16.9741 StartZ=0 EndX=-31.1415 EndY=-16.9741 EndZ=0
    g6: LineSegment StartX=-31.1415 StartY=-16.9741 StartZ=0 EndX=-35.699 EndY=-14.7602 EndZ=0
    g7: LineSegment StartX=-35.699 StartY=-14.7602 StartZ=0 EndX=-35.699 EndY=19.4749 EndZ=0
    g8: LineSegment StartX=-35.699 StartY=19.4749 StartZ=0 EndX=-84.2754 EndY=19.4749 EndZ=0
    g9: Circle CenterX=-72 CenterY=-14 CenterZ=0 NormalX=0 NormalY=0 NormalZ=1 AngleXU=0 Radius=1.25
    g10: LineSegment StartX=84.1226 StartY=19.3553 StartZ=0 EndX=84.1226 EndY=4.97301 EndZ=0
    g11: LineSegment StartX=84.1226 StartY=4.97301 StartZ=0 EndX=52.122 EndY=-24.8182 EndZ=0
    g12: LineSegment StartX=52.122 StartY=-24.8182 StartZ=0 EndX=29.7666 EndY=-27.9955 EndZ=0
    g13: LineSegment StartX=29.7666 StartY=-27.9955 StartZ=0 EndX=11.1289 EndY=-29.2176 EndZ=0
    g14: LineSegment StartX=11.1289 StartY=-29.2176 StartZ=0 EndX=0 EndY=-29.2176 EndZ=0
    g15: LineSegment StartX=0 StartY=-16.9741 StartZ=0 EndX=31.1415 EndY=-16.9741 EndZ=0
    g16: LineSegment StartX=31.1415 StartY=-16.9741 StartZ=0 EndX=35.699 EndY=-14.7602 EndZ=0
    g17: LineSegment StartX=35.699 StartY=-14.7602 StartZ=0 EndX=35.699 EndY=19.3553 EndZ=0
    g18: LineSegment StartX=35.699 StartY=19.3553 StartZ=0 EndX=84.1226 EndY=19.3553 EndZ=0
    g19: Circle CenterX=72 CenterY=-14 CenterZ=0 NormalX=0 NormalY=0 NormalZ=1 AngleXU=0 Radius=1.25
  constraints (37):
    c: Vertical(g0)
    c: Coincident(g0,g1)
    c: Coincident(g1,g2)
    c: Coincident(g2,g3)
    c: Coincident(g3,g4)
    c: PointOnObject(g4,g-2)
    c: Horizontal(g4)
    c: PointOnObject(g5,g-2)
    c: Horizontal(g5)
    c: Coincident(g5,g6)
    c: Coincident(g6,g7)
    c: Vertical(g7)
    c: Coincident(g7,g8)
    c: Coincident(g8,g0)
    c: Horizontal(g8)
    c: Vertical(g10)
    c: Coincident(g10,g11)
    c: Coincident(g11,g12)
    c: Coincident(g12,g13)
    c: Coincident(g13,g14)
    c: Horizontal(g14)
    c: Coincident(g15,g16)
    c: Coincident(g16,g17)
    c: Vertical(g17)
    c: Coincident(g17,g18)
    c: Coincident(g18,g10)
    c: Horizontal(g18)
    c: Equal(g9,g19)
    c: Symmetric(g9,g19,g-2)
    c: Radius(g9) = 1.25
    c: DistanceX(g19) = 72
    c: DistanceY(g19) = -14
    c: Coincident(g15,g5)
    c: Coincident(g14,g4)
    c: Symmetric(g15,g5,g-2)
    c: Symmetric(g11,g1,g-2)
    c: Symmetric(g6,g16,g-2)
FEATURE [PartDesign::Pocket] Pocket013
  BaseFeature = -> Pocket012
  Length = 7
  Length2 = 100
  Profile = -> Sketch028
  Type = 0
  expr: Length = data.smalldash_thickness - data.smalldash_frontthickness - data.rgbled_length
FEATURE [Sketcher::SketchObject] Sketch030
  MapMode = 5
  Placement = pos=(0,0,3) rot=(1,0,0;3.14159rad)
  Support = -> [Pocket013]
  sketch-geometry (4):
    g0: Circle CenterX=-32 CenterY=13.4 CenterZ=0 NormalX=0 NormalY=0 NormalZ=1 AngleXU=0 Radius=0.9
    g1: Circle CenterX=-32 CenterY=-13.4 CenterZ=0 NormalX=0 NormalY=0 NormalZ=1 AngleXU=0 Radius=0.9
    g2: Circle CenterX=32 CenterY=-13.4 CenterZ=0 NormalX=0 NormalY=0 NormalZ=1 AngleXU=0 Radius=0.9
    g3: Circle CenterX=32 CenterY=13.4 CenterZ=0 NormalX=0 NormalY=0 NormalZ=1 AngleXU=0 Radius=0.9
  constraints (9):
    c: Symmetric(g0,g3,g-2)
    c: Symmetric(g1,g0,g-1)
    c: Symmetric(g1,g2,g-2)
    c: Equal(g0,g1)
    c: Equal(g1,g2)
    c: Equal(g2,g3)
    c: Radius(g3) = 0.9
    c: DistanceX(g0) = -32
    c: DistanceY(g0) = 13.4
FEATURE [PartDesign::Pocket] Pocket014
  BaseFeature = -> Pocket013
  Length = 8
  Length2 = 100
  Profile = -> Sketch030
  Type = 0
FEATURE [PartDesign::Body] Body009  label="dashDisplaySmall"
  Group = -> [Sketch021,Pad013,Fillet010,Fillet011,Sketch023,Pocket006,Sketch024,Pocket007,Sketch025,Pocket008,Sketch028,Sketch029,Pocket012,Pocket013,Sketch030,Pocket014]
  Origin = -> Origin009
  Tip = -> Pocket014
FEATURE [Sketcher::SketchObject] Sketch031
  MapMode = 5
  Support = -> [XY_Plane010]
  sketch-geometry (27):
    g0: LineSegment [constr] StartX=-42.5 StartY=60 StartZ=0 EndX=42.5 EndY=60 EndZ=0
    g1: LineSegment [constr] StartX=42.5 StartY=60 StartZ=0 EndX=42.5 EndY=-60 EndZ=0
    g2: LineSegment [constr] StartX=42.5 StartY=-60 StartZ=0 EndX=-42.5 EndY=-60 EndZ=0
    g3: LineSegment [constr] StartX=-42.5 StartY=-60 StartZ=0 EndX=-42.5 EndY=60 EndZ=0
    g4: LineSegment StartX=-45 StartY=70 StartZ=0 EndX=45 EndY=70 EndZ=0
    g5: LineSegment StartX=45 StartY=70 StartZ=0 EndX=45 EndY=-70 EndZ=0
    g6: LineSegment StartX=45 StartY=-70 StartZ=0 EndX=-45 EndY=-70 EndZ=0
    g7: LineSegment StartX=-45 StartY=-70 StartZ=0 EndX=-45 EndY=70 EndZ=0
    g8: Circle [constr] CenterX=-22.5 CenterY=-40 CenterZ=0 NormalX=0 NormalY=0 NormalZ=1 AngleXU=0 Radius=15.5
    g9: Circle CenterX=-22.5 CenterY=-40 CenterZ=0 NormalX=0 NormalY=0 NormalZ=1 AngleXU=0 Radius=11.05
    g10: Circle CenterX=-39 CenterY=65 CenterZ=0 NormalX=0 NormalY=0 NormalZ=1 AngleXU=0 Radius=2.75
    g11: Circle CenterX=39 CenterY=65 CenterZ=0 NormalX=0 NormalY=0 NormalZ=1 AngleXU=0 Radius=2.75
    g12: Circle CenterX=39 CenterY=-65 CenterZ=0 NormalX=0 NormalY=0 NormalZ=1 AngleXU=0 Radius=2.75
    g13: Circle CenterX=-39 CenterY=-65 CenterZ=0 NormalX=0 NormalY=0 NormalZ=1 AngleXU=0 Radius=2.75
    g14: Circle CenterX=-22.5 CenterY=-5 CenterZ=0 NormalX=0 NormalY=0 NormalZ=1 AngleXU=0 Radius=6.1
    g15: Circle [constr] CenterX=-22.5 CenterY=-5 CenterZ=0 NormalX=0 NormalY=0 NormalZ=1 AngleXU=0 Radius=12
    g16: Circle CenterX=-27.5 CenterY=48 CenterZ=0 NormalX=0 NormalY=0 NormalZ=1 AngleXU=0 Radius=6.05
    g17: Circle CenterX=0 CenterY=48 CenterZ=0 NormalX=0 NormalY=0 NormalZ=1 AngleXU=0 Radius=6.05
    g18: Circle CenterX=27.5 CenterY=48 CenterZ=0 NormalX=0 NormalY=0 NormalZ=1 AngleXU=0 Radius=6.05
    g19: Circle CenterX=27.5 CenterY=-48 CenterZ=0 NormalX=0 NormalY=0 NormalZ=1 AngleXU=0 Radius=3.55
    g20: Circle CenterX=27.5 CenterY=-23 CenterZ=0 NormalX=0 NormalY=0 NormalZ=1 AngleXU=0 Radius=3.55
    g21: LineSegment [constr] StartX=27.5 StartY=-48 StartZ=0 EndX=27.5 EndY=-23 EndZ=0
    g22: Circle CenterX=27.5 CenterY=2 CenterZ=0 NormalX=0 NormalY=0 NormalZ=1 AngleXU=0 Radius=3.55
    g23: LineSegment [constr] StartX=27.5 StartY=-23 StartZ=0 EndX=27.5 EndY=2 EndZ=0
    g24: Circle CenterX=27.5 CenterY=27 CenterZ=0 NormalX=0 NormalY=0 NormalZ=1 AngleXU=0 Radius=3.55
    g25: LineSegment [constr] StartX=27.5 StartY=2 StartZ=0 EndX=27.5 EndY=27 EndZ=0
    g26: Circle CenterX=-22.5 CenterY=25 CenterZ=0 NormalX=0 NormalY=0 NormalZ=1 AngleXU=0 Radius=6.05
  constraints (68):
    c: Coincident(g0,g1)
    c: Coincident(g1,g2)
    c: Coincident(g2,g3)
    c: Coincident(g3,g0)
    c: Horizontal(g2)
    c: Vertical(g1)
    c: Symmetric(g0,g0,g-2)
    c: Symmetric(g0,g2,g-1)
    c: DistanceX(g0,g0) = 85
    c: DistanceY(g1,g1) = 120
    c: Coincident(g4,g5)
    c: Coincident(g5,g6)
    c: Coincident(g6,g7)
    c: Coincident(g7,g4)
    c: Horizontal(g6)
    c: Vertical(g5)
    c: Symmetric(g4,g4,g-2)
    c: Symmetric(g6,g4,g-1)
    c: DistanceX(g4,g4) = 90
    c: DistanceY(g5,g5) = 140
    c: Coincident(g9,g8)
    c: Diameter(g8) = 31
    c: DistanceY(g2,g9) = 20
    c: DistanceX(g2,g9) = 20
    c: Symmetric(g13,g12,g-2)
    c: Symmetric(g10,g13,g-1)
    c: Symmetric(g11,g10,g-2)
    c: DistanceY(g11,g4) = 5
    c: DistanceX(g11,g4) = 6
    c: Equal(g11,g10)
    c: Equal(g10,g13)
    c: Equal(g13,g12)
    c: Coincident(g15,g14)
    c: Diameter(g15) = 24
    c: Diameter(g14) = 12.2
    c: DistanceY(g9,g14) = 35
    c: PointOnObject(g17,g-2)
    c: Horizontal(g16,g17)
    c: Equal(g16,g17)
    c: Equal(g17,g18)
    c: Symmetric(g16,g18,g-2)
    c: Diameter(g16) = 12.1
    c: DistanceY(g16,g0) = 12
    c: DistanceX(g0,g16) = 15
    c: Diameter(g19) = 7.1
    c: Equal(g19,g20) = 20
    c: Coincident(g19,g21)
    c: Coincident(g20,g21)
    c: Distance(g21) = 25
    c: Angle(g21) = 1.5708
    c: Equal(g19,g22) = 20
    c: Coincident(g20,g23)
    c: Coincident(g22,g23)
    c: Equal(g21,g23)
    c: Parallel(g23,g21)
    c: Equal(g19,g24) = 20
    c: Coincident(g22,g25)
    c: Coincident(g24,g25)
    c: Equal(g21,g25)
    c: Parallel(g25,g21)
    c: DistanceY(g1,g19) = 12
    c: Vertical(g24,g18)
    c: Vertical(g14,g9)
    c: Diameter(g12) = 5.5
    c: Vertical(g26,g14)
    c: DistanceY(g14,g26) = 30
    c: Diameter(g26) = 12.1
    c: Diameter(g9) = 22.1
FEATURE [PartDesign::Pad] Pad014
  Length = 3
  Length2 = 100
  Profile = -> Sketch031
  Type = 0
FEATURE [Sketcher::SketchObject] Sketch032
  MapMode = 5
  Placement = pos=(0,0,0) rot=(1,0,0;3.14159rad)
  Support = -> [Pad014]
  sketch-geometry (8):
    g0: LineSegment StartX=-42.5 StartY=60 StartZ=0 EndX=42.5 EndY=60 EndZ=0
    g1: LineSegment StartX=42.5 StartY=60 StartZ=0 EndX=42.5 EndY=-60 EndZ=0
    g2: LineSegment StartX=42.5 StartY=-60 StartZ=0 EndX=-42.5 EndY=-60 EndZ=0
    g3: LineSegment StartX=-42.5 StartY=-60 StartZ=0 EndX=-42.5 EndY=60 EndZ=0
    g4: LineSegment StartX=-41 StartY=58.5 StartZ=0 EndX=41 EndY=58.5 EndZ=0
    g5: LineSegment StartX=41 StartY=58.5 StartZ=0 EndX=41 EndY=-58.5 EndZ=0
    g6: LineSegment StartX=41 StartY=-58.5 StartZ=0 EndX=-41 EndY=-58.5 EndZ=0
    g7: LineSegment StartX=-41 StartY=-58.5 StartZ=0 EndX=-41 EndY=58.5 EndZ=0
  constraints (20):
    c: Coincident(g0,g1)
    c: Coincident(g1,g2)
    c: Coincident(g2,g3)
    c: Coincident(g3,g0)
    c: Horizontal(g2)
    c: Vertical(g1)
    c: Symmetric(g0,g0,g-2)
    c: Symmetric(g0,g2,g-1)
    c: DistanceY(g3,g3) = 120
    c: Coincident(g4,g5)
    c: Coincident(g5,g6)
    c: Coincident(g6,g7)
    c: Coincident(g7,g4)
    c: Horizontal(g6)
    c: Vertical(g7)
    c: Symmetric(g4,g4,g-2)
    c: DistanceX(g4,g4) = 82
    c: DistanceX(g0,g0) = 85
    c: DistanceY(g5,g5) = 117
    c: Symmetric(g4,g5,g-1)
FEATURE [PartDesign::Pad] Pad015
  BaseFeature = -> Pad014
  Length = 30
  Length2 = 100
  Profile = -> Sketch032
  Type = 0
FEATURE [Sketcher::SketchObject] Sketch034
  MapMode = 5
  Support = -> [XY_Plane011]
  expr: Constraints[51] = (data.seg7_width_all - data.seg7_width) / 2
  expr: Constraints[49] = data.seg7_length + 0.5
  expr: Constraints[37] = data.seg7_width_all + 0.05
  expr: Constraints[50] = data.seg7_width
  expr: Constraints[36] = data.seg7_length_all
  sketch-geometry (38):
    g0: LineSegment [constr] StartX=-42.5 StartY=60 StartZ=0 EndX=42.5 EndY=60 EndZ=0
    g1: LineSegment [constr] StartX=42.5 StartY=60 StartZ=0 EndX=42.5 EndY=-60 EndZ=0
    g2: LineSegment [constr] StartX=42.5 StartY=-60 StartZ=0 EndX=-42.5 EndY=-60 EndZ=0
    g3: LineSegment [constr] StartX=-42.5 StartY=-60 StartZ=0 EndX=-42.5 EndY=60 EndZ=0
    g4: LineSegment StartX=-45 StartY=70 StartZ=0 EndX=45 EndY=70 EndZ=0
    g5: LineSegment StartX=45 StartY=70 StartZ=0 EndX=45 EndY=-70 EndZ=0
    g6: LineSegment StartX=45 StartY=-70 StartZ=0 EndX=-45 EndY=-70 EndZ=0
    g7: LineSegment StartX=-45 StartY=-70 StartZ=0 EndX=-45 EndY=70 EndZ=0
    g8: Circle CenterX=-39 CenterY=65 CenterZ=0 NormalX=0 NormalY=0 NormalZ=1 AngleXU=0 Radius=2.75
    g9: Circle CenterX=39 CenterY=65 CenterZ=0 NormalX=0 NormalY=0 NormalZ=1 AngleXU=0 Radius=2.75
    g10: Circle CenterX=39 CenterY=-65 CenterZ=0 NormalX=0 NormalY=0 NormalZ=1 AngleXU=0 Radius=2.75
    g11: Circle CenterX=-39 CenterY=-65 CenterZ=0 NormalX=0 NormalY=0 NormalZ=1 AngleXU=0 Radius=2.75
    g12: LineSegment [constr] StartX=-41.15 StartY=57 StartZ=0 EndX=41.15 EndY=57 EndZ=0
    g13: LineSegment [constr] StartX=41.15 StartY=57 StartZ=0 EndX=41.15 EndY=41.45 EndZ=0
    g14: LineSegment [constr] StartX=41.15 StartY=41.45 StartZ=0 EndX=-41.15 EndY=41.45 EndZ=0
    g15: LineSegment [constr] StartX=-41.15 StartY=41.45 StartZ=0 EndX=-41.15 EndY=57 EndZ=0
    g16: LineSegment StartX=-28.9 StartY=56.35 StartZ=0 EndX=32.6 EndY=56.35 EndZ=0
    g17: LineSegment StartX=32.6 StartY=56.35 StartZ=0 EndX=32.6 EndY=42.15 EndZ=0
    g18: LineSegment StartX=32.6 StartY=42.15 StartZ=0 EndX=-28.9 EndY=42.15 EndZ=0
    g19: LineSegment StartX=-28.9 StartY=42.15 StartZ=0 EndX=-28.9 EndY=56.35 EndZ=0
    g20: LineSegment StartX=-28.9 StartY=34.35 StartZ=0 EndX=32.6 EndY=34.35 EndZ=0
    g21: LineSegment StartX=32.6 StartY=34.35 StartZ=0 EndX=32.6 EndY=20.15 EndZ=0
    g22: LineSegment StartX=32.6 StartY=20.15 StartZ=0 EndX=-28.9 EndY=20.15 EndZ=0
    g23: LineSegment StartX=-28.9 StartY=20.15 StartZ=0 EndX=-28.9 EndY=34.35 EndZ=0
    g24: LineSegment [constr] StartX=-28.9 StartY=56.35 StartZ=0 EndX=-28.9 EndY=34.35 EndZ=0
    g25: LineSegment StartX=-28.9 StartY=12.35 StartZ=0 EndX=32.6 EndY=12.35 EndZ=0
    g26: LineSegment StartX=32.6 StartY=12.35 StartZ=0 EndX=32.6 EndY=-1.85 EndZ=0
    g27: LineSegment StartX=32.6 StartY=-1.85 StartZ=0 EndX=-28.9 EndY=-1.85 EndZ=0
    g28: LineSegment StartX=-28.9 StartY=-1.85 StartZ=0 EndX=-28.9 EndY=12.35 EndZ=0
    g29: LineSegment [constr] StartX=-28.9 StartY=34.35 StartZ=0 EndX=-28.9 EndY=12.35 EndZ=0
    g30: LineSegment StartX=-28.9 StartY=-9.65 StartZ=0 EndX=32.6 EndY=-9.65 EndZ=0
    g31: LineSegment StartX=32.6 StartY=-9.65 StartZ=0 EndX=32.6 EndY=-23.85 EndZ=0
    g32: LineSegment StartX=32.6 StartY=-23.85 StartZ=0 EndX=-28.9 EndY=-23.85 EndZ=0
    g33: LineSegment StartX=-28.9 StartY=-23.85 StartZ=0 EndX=-28.9 EndY=-9.65 EndZ=0
    g34: LineSegment [constr] StartX=-28.9 StartY=12.35 StartZ=0 EndX=-28.9 EndY=-9.65 EndZ=0
    g35: Circle CenterX=-29.5 CenterY=-46 CenterZ=0 NormalX=0 NormalY=0 NormalZ=1 AngleXU=0 Radius=3.5
    g36: Circle CenterX=0 CenterY=-46 CenterZ=0 NormalX=0 NormalY=0 NormalZ=1 AngleXU=0 Radius=3.5
    g37: Circle CenterX=29.5 CenterY=-46 CenterZ=0 NormalX=0 NormalY=0 NormalZ=1 AngleXU=0 Radius=3.5
  constraints (102):
    c: Coincident(g0,g1)
    c: Coincident(g1,g2)
    c: Coincident(g2,g3)
    c: Coincident(g3,g0)
    c: Horizontal(g2)
    c: Vertical(g1)
    c: Symmetric(g0,g0,g-2)
    c: Symmetric(g0,g2,g-1)
    c: DistanceX(g0,g0) = 85
    c: DistanceY(g1,g1) = 120
    c: Coincident(g4,g5)
    c: Coincident(g5,g6)
    c: Coincident(g6,g7)
    c: Coincident(g7,g4)
    c: Horizontal(g6)
    c: Vertical(g5)
    c: Symmetric(g4,g4,g-2)
    c: Symmetric(g6,g4,g-1)
    c: DistanceX(g4,g4) = 90
    c: DistanceY(g5,g5) = 140
    c: Symmetric(g11,g10,g-2)
    c: Symmetric(g8,g11,g-1)
    c: Symmetric(g9,g8,g-2)
    c: DistanceY(g9,g4) = 5
    c: DistanceX(g9,g4) = 6
    c: Equal(g9,g8)
    c: Equal(g8,g11)
    c: Equal(g11,g10)
    c: Diameter(g10) = 5.5
    c: Coincident(g12,g13)
    c: Coincident(g13,g14)
    c: Coincident(g14,g15)
    c: Coincident(g15,g12)
    c: Horizontal(g14)
    c: Vertical(g13)
    c: Vertical(g15)
    c: DistanceX(g12,g12) = 82.3
    c: DistanceY(g13,g13) = 15.55
    c: DistanceY(g12,g0) = 3
    c: Symmetric(g12,g12,g-2)
    c: Coincident(g16,g17)
    c: Coincident(g17,g18)
    c: Coincident(g18,g19)
    c: Coincident(g19,g16)
    c: Horizontal(g16)
    c: Horizontal(g18)
    c: Vertical(g17)
    c: Vertical(g19)
    c: DistanceX(g14,g18) = 12.25
    c: DistanceX(g16,g16) = 61.5
    c: DistanceY(g17,g17) = 14.2
    c: DistanceY(g16,g12) = 0.65
    c: Coincident(g20,g21)
    c: Coincident(g21,g22)
    c: Coincident(g22,g23)
    c: Coincident(g23,g20)
    c: Horizontal(g20)
    c: Horizontal(g22)
    c: Vertical(g21)
    c: Vertical(g23)
    c: Equal(g16,g20) = 61
    c: Equal(g17,g21) = 14.2
    c: Coincident(g16,g24)
    c: Coincident(g20,g24)
    c: Distance(g24) = 22
    c: Angle(g24) = -1.5708
    c: Coincident(g25,g26)
    c: Coincident(g26,g27)
    c: Coincident(g27,g28)
    c: Coincident(g28,g25)
    c: Horizontal(g25)
    c: Horizontal(g27)
    c: Vertical(g26)
    c: Vertical(g28)
    c: Equal(g16,g25) = 61
    c: Equal(g17,g26) = 14.2
    c: Coincident(g20,g29)
    c: Coincident(g25,g29)
    c: Equal(g24,g29)
    c: Parallel(g29,g24)
    c: Coincident(g30,g31)
    c: Coincident(g31,g32)
    c: Coincident(g32,g33)
    c: Coincident(g33,g30)
    c: Horizontal(g30)
    c: Horizontal(g32)
    c: Vertical(g31)
    c: Vertical(g33)
    c: Equal(g16,g30) = 61
    c: Equal(g17,g31) = 14.2
    c: Coincident(g25,g34)
    c: Coincident(g30,g34)
    c: Equal(g24,g34)
    c: Parallel(g34,g24)
    c: PointOnObject(g36,g-2)
    c: Horizontal(g35,g36)
    c: Symmetric(g35,g37,g-2)
    c: Equal(g35,g36)
    c: Equal(g36,g37)
    c: Diameter(g35) = 7
    c: DistanceX(g2,g35) = 13
    c: DistanceY(g2,g35) = 14
FEATURE [PartDesign::Pad] Pad016
  Length = 3
  Length2 = 100
  Profile = -> Sketch034
  Type = 0
FEATURE [Sketcher::SketchObject] Sketch033
  MapMode = 5
  Placement = pos=(0,0,0) rot=(1,0,0;3.14159rad)
  Support = -> [Pad016]
  sketch-geometry (8):
    g0: LineSegment StartX=-42.5 StartY=60 StartZ=0 EndX=42.5 EndY=60 EndZ=0
    g1: LineSegment StartX=42.5 StartY=60 StartZ=0 EndX=42.5 EndY=-60 EndZ=0
    g2: LineSegment StartX=42.5 StartY=-60 StartZ=0 EndX=-42.5 EndY=-60 EndZ=0
    g3: LineSegment StartX=-42.5 StartY=-60 StartZ=0 EndX=-42.5 EndY=60 EndZ=0
    g4: LineSegment StartX=-41 StartY=58.5 StartZ=0 EndX=41 EndY=58.5 EndZ=0
    g5: LineSegment StartX=41 StartY=58.5 StartZ=0 EndX=41 EndY=-58.5 EndZ=0
    g6: LineSegment StartX=41 StartY=-58.5 StartZ=0 EndX=-41 EndY=-58.5 EndZ=0
    g7: LineSegment StartX=-41 StartY=-58.5 StartZ=0 EndX=-41 EndY=58.5 EndZ=0
  constraints (20):
    c: Coincident(g0,g1)
    c: Coincident(g1,g2)
    c: Coincident(g2,g3)
    c: Coincident(g3,g0)
    c: Horizontal(g2)
    c: Vertical(g1)
    c: Symmetric(g0,g0,g-2)
    c: Symmetric(g0,g2,g-1)
    c: DistanceY(g3,g3) = 120
    c: Coincident(g4,g5)
    c: Coincident(g5,g6)
    c: Coincident(g6,g7)
    c: Coincident(g7,g4)
    c: Horizontal(g6)
    c: Vertical(g7)
    c: Symmetric(g4,g4,g-2)
    c: DistanceX(g4,g4) = 82
    c: DistanceX(g0,g0) = 85
    c: DistanceY(g5,g5) = 117
    c: Symmetric(g4,g5,g-1)
FEATURE [PartDesign::Pad] Pad017
  BaseFeature = -> Pad016
  Length = 5
  Length2 = 100
  Profile = -> Sketch033
  Type = 0
FEATURE [Sketcher::SketchObject] Sketch035
  ExternalGeometry = -> [Pad017]
  MapMode = 5
  Placement = pos=(0,0,0) rot=(1,0,0;3.14159rad)
  Support = -> [Pad017]
  sketch-geometry (20):
    g0: LineSegment StartX=-35 StartY=26.5 StartZ=0 EndX=39 EndY=26.5 EndZ=0
    g1: LineSegment StartX=39 StartY=26.5 StartZ=0 EndX=39 EndY=-58.5 EndZ=0
    g2: LineSegment StartX=39 StartY=-58.5 StartZ=0 EndX=-35 EndY=-58.5 EndZ=0
    g3: LineSegment StartX=-35 StartY=-58.5 StartZ=0 EndX=-35 EndY=26.5 EndZ=0
    g4: LineSegment StartX=-28.9 StartY=-42.15 StartZ=0 EndX=32.6 EndY=-42.15 EndZ=0
    g5: LineSegment StartX=32.6 StartY=-42.15 StartZ=0 EndX=32.6 EndY=-56.35 EndZ=0
    g6: LineSegment StartX=32.6 StartY=-56.35 StartZ=0 EndX=-28.9 EndY=-56.35 EndZ=0
    g7: LineSegment StartX=-28.9 StartY=-56.35 StartZ=0 EndX=-28.9 EndY=-42.15 EndZ=0
    g8: LineSegment StartX=-28.9 StartY=23.85 StartZ=0 EndX=32.6 EndY=23.85 EndZ=0
    g9: LineSegment StartX=32.6 StartY=23.85 StartZ=0 EndX=32.6 EndY=9.65 EndZ=0
    g10: LineSegment StartX=32.6 StartY=9.65 StartZ=0 EndX=-28.9 EndY=9.65 EndZ=0
    g11: LineSegment StartX=-28.9 StartY=9.65 StartZ=0 EndX=-28.9 EndY=23.85 EndZ=0
    g12: LineSegment StartX=32.6 StartY=-34.35 StartZ=0 EndX=-28.9 EndY=-34.35 EndZ=0
    g13: LineSegment StartX=-28.9 StartY=-34.35 StartZ=0 EndX=-28.9 EndY=-20.15 EndZ=0
    g14: LineSegment StartX=-28.9 StartY=-20.15 StartZ=0 EndX=32.6 EndY=-20.15 EndZ=0
    g15: LineSegment StartX=32.6 StartY=-20.15 StartZ=0 EndX=32.6 EndY=-34.35 EndZ=0
    g16: LineSegment StartX=-28.9 StartY=1.85 StartZ=0 EndX=32.6 EndY=1.85 EndZ=0
    g17: LineSegment StartX=32.6 StartY=1.85 StartZ=0 EndX=32.6 EndY=-12.35 EndZ=0
    g18: LineSegment StartX=32.6 StartY=-12.35 StartZ=0 EndX=-28.9 EndY=-12.35 EndZ=0
    g19: LineSegment StartX=-28.9 StartY=-12.35 StartZ=0 EndX=-28.9 EndY=1.85 EndZ=0
  constraints (52):
    c: Coincident(g0,g1)
    c: Coincident(g1,g2)
    c: Coincident(g2,g3)
    c: Coincident(g3,g0)
    c: Horizontal(g0)
    c: Horizontal(g2)
    c: Vertical(g1)
    c: Vertical(g3)
    c: PointOnObject(g2,g-10)
    c: DistanceX(g0,g0) = 74
    c: DistanceY(g3,g3) = 85
    c: DistanceX(g-10,g2) = 6
    c: Coincident(g4,g5)
    c: Coincident(g5,g6)
    c: Coincident(g6,g7)
    c: Coincident(g7,g4)
    c: Horizontal(g4)
    c: Horizontal(g6)
    c: Vertical(g5)
    c: Vertical(g7)
    c: Coincident(g4,g-8)
    c: Coincident(g5,g-9)
    c: Coincident(g8,g9)
    c: Coincident(g9,g10)
    c: Coincident(g10,g11)
    c: Coincident(g11,g8)
    c: Horizontal(g8)
    c: Horizontal(g10)
    c: Vertical(g9)
    c: Vertical(g11)
    c: Coincident(g8,g-7)
    c: Coincident(g9,g-11)
    c: Coincident(g12,g13)
    c: Coincident(g13,g14)
    c: Coincident(g14,g15)
    c: Coincident(g15,g12)
    c: Horizontal(g12)
    c: Horizontal(g14)
    c: Vertical(g13)
    c: Vertical(g15)
    c: Coincident(g12,g-5)
    c: Coincident(g13,g-6)
    c: Coincident(g16,g17)
    c: Coincident(g17,g18)
    c: Coincident(g18,g19)
    c: Coincident(g19,g16)
    c: Horizontal(g16)
    c: Horizontal(g18)
    c: Vertical(g17)
    c: Vertical(g19)
    c: Coincident(g16,g-3)
    c: Coincident(g17,g-4)
FEATURE [PartDesign::Pad] Pad018
  BaseFeature = -> Pad017
  Length = 5
  Length2 = 100
  Profile = -> Sketch035
  Type = 0
FEATURE [PartDesign::Fillet] Fillet013
  Base = -> Pad018 [Edge8,Edge5,Edge1,Edge2]
  BaseFeature = -> Pad018
  Radius = 5
FEATURE [PartDesign::Fillet] Fillet014
  Base = -> Pad015 [Edge2,Edge1,Edge8,Edge5]
  BaseFeature = -> Pad015
  Radius = 5
FEATURE [PartDesign::Body] Body010  label="starterPanel"
  Group = -> [Sketch031,Pad014,Sketch032,Pad015,Fillet014]
  Origin = -> Origin010
  Tip = -> Fillet014
FEATURE [Sketcher::SketchObject] Sketch036
  MapMode = 5
  Support = -> [XY_Plane012]
  sketch-geometry (7):
    g0: LineSegment StartX=6.75 StartY=0 StartZ=0 EndX=11 EndY=0 EndZ=0
    g1: LineSegment StartX=11 StartY=0 StartZ=0 EndX=11 EndY=0.4 EndZ=0
    g2: LineSegment StartX=11 StartY=0.4 StartZ=0 EndX=10.4481 EndY=8.45468 EndZ=0
    g3: ArcOfCircle CenterX=9.65 CenterY=8.4 CenterZ=0 NormalX=0 NormalY=0 NormalZ=1 AngleXU=0 Radius=0.8 StartAngle=0.0684086 EndAngle=3.14159
    g4: LineSegment StartX=8.85 StartY=8.4 StartZ=0 EndX=8.85 EndY=0.4 EndZ=0
    g5: LineSegment StartX=8.85 StartY=0.4 StartZ=0 EndX=6.75 EndY=0.4 EndZ=0
    g6: LineSegment StartX=6.75 StartY=0.4 StartZ=0 EndX=6.75 EndY=0 EndZ=0
  constraints (21):
    c: PointOnObject(g0,g-1)
    c: PointOnObject(g0,g-1)
    c: Coincident(g0,g1)
    c: Coincident(g1,g2)
    c: Tangent(g2,g3) = -1.5708
    c: Coincident(g3,g4)
    c: Vertical(g4)
    c: Coincident(g4,g5)
    c: Horizontal(g5)
    c: Coincident(g5,g6)
    c: Vertical(g6)
    c: Horizontal(g3,g3)
    c: Coincident(g6,g0)
    c: DistanceX(g0) = 6.75
    c: Equal(g6,g1)
    c: Vertical(g1)
    c: DistanceY(g1,g1) = 0.4
    c: DistanceY(g4,g3) = 8
    c: DistanceX(g4) = 8.85
    c: DistanceX(g0) = 11
    c: Radius(g3) = 0.8
FEATURE [PartDesign::Revolution] Revolution
  Angle = 360
  Axis = (0,1,0)
  Base = (0,0,0)
  Profile = -> Sketch036
  ReferenceAxis = -> Sketch036 [V_Axis]
  Reversed = true
FEATURE [PartDesign::Body] Body012  label="safetyCapSmall12mm"
  Group = -> [Sketch036,Revolution]
  Origin = -> Origin012
  Tip = -> Revolution
FEATURE [Sketcher::SketchObject] Sketch037
  MapMode = 5
  Support = -> [XY_Plane013]
  sketch-geometry (7):
    g0: LineSegment StartX=6 StartY=0 StartZ=0 EndX=11 EndY=0 EndZ=0
    g1: LineSegment StartX=11 StartY=0 StartZ=0 EndX=11 EndY=0.4 EndZ=0
    g2: LineSegment StartX=11 StartY=0.4 StartZ=0 EndX=10.449 EndY=11.4399 EndZ=0
    g3: ArcOfCircle CenterX=9.65 CenterY=11.4 CenterZ=0 NormalX=0 NormalY=0 NormalZ=1 AngleXU=0 Radius=0.8 StartAngle=0.0498681 EndAngle=3.14159
    g4: LineSegment StartX=8.85 StartY=11.4 StartZ=0 EndX=8.85 EndY=0.4 EndZ=0
    g5: LineSegment StartX=8.85 StartY=0.4 StartZ=0 EndX=6 EndY=0.4 EndZ=0
    g6: LineSegment StartX=6 StartY=0.4 StartZ=0 EndX=6 EndY=0 EndZ=0
  constraints (21):
    c: PointOnObject(g0,g-1)
    c: PointOnObject(g0,g-1)
    c: Coincident(g0,g1)
    c: Coincident(g1,g2)
    c: Tangent(g2,g3) = -1.5708
    c: Coincident(g3,g4)
    c: Vertical(g4)
    c: Coincident(g4,g5)
    c: Horizontal(g5)
    c: Coincident(g5,g6)
    c: Vertical(g6)
    c: Horizontal(g3,g3)
    c: Coincident(g6,g0)
    c: DistanceX(g0) = 6
    c: Equal(g6,g1)
    c: Vertical(g1)
    c: DistanceY(g1,g1) = 0.4
    c: DistanceX(g4) = 8.85
    c: DistanceX(g0) = 11
    c: Radius(g3) = 0.8
    c: DistanceY(g4,g4) = 11
FEATURE [PartDesign::Revolution] Revolution001
  Angle = 360
  Axis = (0,1,0)
  Base = (0,0,0)
  Profile = -> Sketch037
  ReferenceAxis = -> Sketch037 [V_Axis]
  Reversed = true
FEATURE [PartDesign::Body] Body013  label="safetyCapHigh12mm"
  Group = -> [Sketch037,Revolution001]
  Origin = -> Origin013
  Tip = -> Revolution001
FEATURE [PartDesign::Fillet] Fillet015
  Base = -> Fillet013 [Edge143,Edge142,Edge138,Edge140,Edge135,Edge134,Edge132,Edge130,Edge119,Edge118,Edge116,Edge114,Edge127,Edge122,Edge124,Edge126]
  BaseFeature = -> Fillet013
  Radius = 0.5
FEATURE [PartDesign::Body] Body011  label="simHubController"
  Group = -> [Sketch034,Pad016,Sketch033,Pad017,Sketch035,Pad018,Fillet013,Fillet015]
  Origin = -> Origin011
  Tip = -> Fillet015
FEATURE [Sketcher::SketchObject] Sketch038
  MapMode = 5
  Support = -> [XY_Plane014]
  sketch-geometry (20):
    g0: LineSegment StartX=-90 StartY=-38.4948 StartZ=0 EndX=-90 EndY=17.5052 EndZ=0
    g1: LineSegment StartX=90 StartY=17.5052 StartZ=0 EndX=90 EndY=-38.4948 EndZ=0
    g2: LineSegment StartX=90 StartY=-38.4948 StartZ=0 EndX=38.25 EndY=-38.4948 EndZ=0
    g3: ArcOfCircle CenterX=1.99e-14 CenterY=-285.23 CenterZ=0 NormalX=0 NormalY=0 NormalZ=1 AngleXU=0 Radius=315.83 StartAngle=1.28183 EndAngle=1.85976
    g4: LineSegment StartX=-38.25 StartY=-38.4948 StartZ=0 EndX=-38.25 EndY=-73.4948 EndZ=0
    g5: LineSegment StartX=-38.25 StartY=-73.4948 StartZ=0 EndX=-31.25 EndY=-73.4948 EndZ=0
    g6: LineSegment StartX=-31.25 StartY=-73.4948 StartZ=0 EndX=-31.25 EndY=-38.4948 EndZ=0
    g7: LineSegment StartX=-31.25 StartY=-38.4948 StartZ=0 EndX=-24.75 EndY=-38.4948 EndZ=0
    g8: LineSegment StartX=-24.75 StartY=-38.4948 StartZ=0 EndX=-24.75 EndY=-73.4948 EndZ=0
    g9: LineSegment StartX=-24.75 StartY=-73.4948 StartZ=0 EndX=-17.75 EndY=-73.4948 EndZ=0
    g10: LineSegment StartX=-17.75 StartY=-73.4948 StartZ=0 EndX=-17.75 EndY=-38.4948 EndZ=0
    g11: LineSegment StartX=-17.75 StartY=-38.4948 StartZ=0 EndX=17.75 EndY=-38.4948 EndZ=0
    g12: LineSegment StartX=17.75 StartY=-38.4948 StartZ=0 EndX=17.75 EndY=-73.4948 EndZ=0
    g13: LineSegment StartX=17.75 StartY=-73.4948 StartZ=0 EndX=24.75 EndY=-73.4948 EndZ=0
    g14: LineSegment StartX=24.75 StartY=-73.4948 StartZ=0 EndX=24.75 EndY=-38.4948 EndZ=0
    g15: LineSegment StartX=24.75 StartY=-38.4948 StartZ=0 EndX=31.25 EndY=-38.4948 EndZ=0
    g16: LineSegment StartX=31.25 StartY=-38.4948 StartZ=0 EndX=31.25 EndY=-73.4948 EndZ=0
    g17: LineSegment StartX=31.25 StartY=-73.4948 StartZ=0 EndX=38.25 EndY=-73.4948 EndZ=0
    g18: LineSegment StartX=38.25 StartY=-73.4948 StartZ=0 EndX=38.25 EndY=-38.4948 EndZ=0
    g19: LineSegment StartX=-38.25 StartY=-38.4948 StartZ=0 EndX=-90 EndY=-38.4948 EndZ=0
  constraints (57):
    c: Coincident(g1,g2)
    c: Coincident(g19,g0)
    c: DistanceX(g19,g2) = 180
    c: Symmetric(g0,g1,g-2)
    c: Symmetric(g0,g1,g-2)
    c: Vertical(g0)
    c: DistanceY(g1,g1) = 56
    c: Coincident(g3,g0)
    c: Coincident(g3,g1)
    c: DistanceY(g3) = -285.23
    c: Radius(g3) = 315.83
    c: Vertical(g4)
    c: Coincident(g4,g5)
    c: Coincident(g5,g6)
    c: Vertical(g6)
    c: Coincident(g6,g7)
    c: Horizontal(g7)
    c: Coincident(g7,g8)
    c: Vertical(g8)
    c: Coincident(g8,g9)
    c: Horizontal(g9)
    c: Coincident(g9,g10)
    c: Vertical(g10)
    c: Coincident(g10,g11)
    c: Horizontal(g11)
    c: Coincident(g11,g12)
    c: Vertical(g12)
    c: Coincident(g12,g13)
    c: Coincident(g13,g14)
    c: Vertical(g14)
    c: Coincident(g14,g15)
    c: Horizontal(g15)
    c: Coincident(g15,g16)
    c: Vertical(g16)
    c: Coincident(g16,g17)
    c: Coincident(g17,g18)
    c: Vertical(g18)
    c: Coincident(g2,g18)
    c: Coincident(g19,g4)
    c: Tangent(g2,g19)
    c: Equal(g8,g6)
    c: Equal(g6,g10)
    c: Equal(g10,g12)
    c: Equal(g12,g14)
    c: Equal(g14,g16)
    c: Horizontal(g17)
    c: Horizontal(g5)
    c: Equal(g5,g9)
    c: Equal(g9,g13)
    c: Equal(g13,g17)
    c: DistanceX(g7,g7) = 6.5
    c: Symmetric(g7,g14,g-2)
    c: Equal(g15,g7)
    c: DistanceX(g7,g14) = 49.5
    c: DistanceX(g5,g5) = 7
    c: Horizontal(g6,g4)
    c: DistanceY(g18,g18) = 35
FEATURE [PartDesign::Pad] Pad019
  Length = 2
  Length2 = 100
  Profile = -> Sketch038
  Type = 0
FEATURE [PartDesign::Fillet] Fillet016
  Base = -> Pad019 [Edge8,Edge5]
  BaseFeature = -> Pad019
  Radius = 30
FEATURE [Sketcher::SketchObject] Sketch039
  MapMode = 5
  Placement = pos=(0,0,0) rot=(1,0,0;3.14159rad)
  Support = -> [Fillet016]
  sketch-geometry (2):
    g0: Circle CenterX=-72 CenterY=-14 CenterZ=0 NormalX=0 NormalY=0 NormalZ=1 AngleXU=0 Radius=1.25
    g1: Circle CenterX=72 CenterY=-14 CenterZ=0 NormalX=0 NormalY=0 NormalZ=1 AngleXU=0 Radius=1.25
  constraints (5):
    c: Equal(g0,g1)
    c: Symmetric(g0,g1,g-2)
    c: Radius(g0) = 1.25
    c: DistanceX(g1) = 72
    c: DistanceY(g1) = -14
FEATURE [PartDesign::Pocket] Pocket019
  BaseFeature = -> Fillet016
  Length = 5
  Length2 = 100
  Profile = -> Sketch039
  Type = 1
FEATURE [PartDesign::Fillet] Fillet017
  Base = -> Pocket019 [Edge3,Edge57]
  BaseFeature = -> Pocket019
  Radius = 3
FEATURE [Sketcher::SketchObject] Sketch041
  MapMode = 5
  Placement = pos=(0,0,0) rot=(1,0,0;3.14159rad)
  Support = -> [Fillet017]
  sketch-geometry (4):
    g0: LineSegment StartX=-75 StartY=15 StartZ=0 EndX=-70 EndY=15 EndZ=0
    g1: LineSegment StartX=-70 StartY=15 StartZ=0 EndX=-70 EndY=0 EndZ=0
    g2: LineSegment StartX=-70 StartY=0 StartZ=0 EndX=-75 EndY=0 EndZ=0
    g3: LineSegment StartX=-75 StartY=0 StartZ=0 EndX=-75 EndY=15 EndZ=0
  constraints (12):
    c: Coincident(g0,g1)
    c: Coincident(g1,g2)
    c: Coincident(g2,g3)
    c: Coincident(g3,g0)
    c: Horizontal(g0)
    c: Horizontal(g2)
    c: Vertical(g1)
    c: Vertical(g3)
    c: DistanceX(g0,g0) = 5
    c: DistanceY(g1,g1) = 15
    c: PointOnObject(g1,g-1)
    c: DistanceX(g1) = -70
FEATURE [Part::Feature] Part__Feature  label="nano-board"
  shape: bbox 43.2 x 4.77 x 18 mm, 378 faces (baked)
FEATURE [Part::Feature] Part__Feature001  label="2pin_header__02"
  Placement = pos=(-1.143,1.6,-7.62) rot=(0,0,1;0rad)
  shape: bbox 5 x 11.75 x 2.54 mm, 46 faces (baked)
FEATURE [Part::Feature] Part__Feature002  label="2pin_header__003"
  Placement = pos=(-1.143,1.6,-5.08) rot=(0,0,1;0rad)
  shape: bbox 5 x 11.75 x 2.54 mm, 46 faces (baked)
FEATURE [Part::Feature] Part__Feature003  label="2pin_header__004"
  Placement = pos=(-1.143,1.6,-10.16) rot=(0,0,1;0rad)
  shape: bbox 5 x 11.75 x 2.54 mm, 46 faces (baked)
FEATURE [Part::Feature] Part__Feature004  label="15pin_header__"
  Placement = pos=(0,0,0) rot=(0.707107,0,0.707107;3.14159rad)
  shape: bbox 38.1 x 11.75 x 2.54 mm, 364 faces (baked)
FEATURE [Part::Feature] Part__Feature005  label="15pin_header__001"
  Placement = pos=(-3e-15,0,-15.24) rot=(0.707107,0,0.707107;3.14159rad)
  shape: bbox 38.1 x 11.75 x 2.54 mm, 364 faces (baked)
FEATURE [Part::Feature] Part__Feature006  label="atmega328"
  Placement = pos=(23.85,1.75,-7.62) rot=(0,1,0;3.92699rad)
  shape: bbox 11.25 x 1.2 x 11.25 mm, 1867 faces (baked)
FEATURE [Part::Feature] Part__Feature007  label="ftdi FT232rl"
  Placement = pos=(29.05,0,-7.67) rot=(0.707107,0,-0.707107;3.14159rad)
  shape: bbox 10.2 x 1.9 x 9.287 mm, 717 faces (baked)
FEATURE [Part::Feature] Part__Feature008  label="smt_resistor222"
  Placement = pos=(21.86,0,-5.8) rot=(0.707107,0,-0.707107;3.14159rad)
  shape: bbox 3.8 x 0.6 x 1.813 mm, 74 faces (baked)
FEATURE [Part::Feature] Part__Feature009  label="smt_resistor223"
  Placement = pos=(21.86,0,-9) rot=(0.707107,0,-0.707107;3.14159rad)
  shape: bbox 3.8 x 0.6 x 1.813 mm, 74 faces (baked)
FEATURE [Part::Feature] Part__Feature010  label="smt_resistor224"
  Placement = pos=(36.75,0,-7.6) rot=(0.707107,0,-0.707107;3.14159rad)
  shape: bbox 3.8 x 0.6 x 1.813 mm, 74 faces (baked)
FEATURE [Part::Feature] Part__Feature011  label="smt_resistor225"
  Placement = pos=(36.75,0,-12) rot=(0.707107,0,-0.707107;3.14159rad)
  shape: bbox 3.8 x 0.6 x 1.813 mm, 74 faces (baked)
FEATURE [Part::Feature] Part__Feature012  label="smt_resistor226"
  Placement = pos=(8.2,0,-2.6) rot=(0.707107,0,-0.707107;3.14159rad)
  shape: bbox 3.8 x 0.6 x 1.813 mm, 74 faces (baked)
FEATURE [Part::Feature] Part__Feature013  label="led"
  Placement = pos=(10.4,1.6,-2.8) rot=(0,0,1;0rad)
  shape: bbox 4.438 x 0.8452 x 2.138 mm, 57 faces, 2 solids (baked)
FEATURE [Part::Feature] Part__Feature014  label="led001"
  Placement = pos=(10.4,1.6,-5.55) rot=(0,0,1;0rad)
  shape: bbox 4.438 x 0.8452 x 2.138 mm, 57 faces, 2 solids (baked)
FEATURE [Part::Feature] Part__Feature015  label="led002"
  Placement = pos=(10.4,1.6,-12.5) rot=(0,0,1;0rad)
  shape: bbox 4.438 x 0.8452 x 2.138 mm, 57 faces, 2 solids (baked)
FEATURE [Part::Feature] Part__Feature016  label="led003"
  Placement = pos=(10.4,1.6,-9.05) rot=(0,0,1;0rad)
  shape: bbox 4.438 x 0.8452 x 2.138 mm, 57 faces, 2 solids (baked)
FEATURE [Part::Feature] Part__Feature017  label="16mhz crystal - measured"
  Placement = pos=(18.5113,1.6,-3.55414) rot=(0,-1,0;0.785398rad)
  shape: bbox 3.394 x 0.8 x 3.394 mm, 71 faces (baked)
FEATURE [Part::Feature] Part__Feature018  label="MINIUSBSHELL"
  shape: bbox 11.03 x 3.822 x 9.475 mm, 243 faces (baked)
FEATURE [Part::Feature] Part__Feature019  label="MINIUSBCORE"
  Placement = pos=(0,0,6.7) rot=(0,1,0;3.14159rad)
  shape: bbox 7.7 x 4.5 x 8.2 mm, 127 faces (baked)
FEATURE [Part::Feature] Part__Feature020  label="MINI USB CONTACT"
  Placement = pos=(-1.6,0,5.7) rot=(0,1,0;3.14159rad)
  shape: bbox 0.5011 x 2.551 x 9.423 mm, 31 faces (baked)
FEATURE [Part::Feature] Part__Feature021  label="MINI USB CONTACT001"
  Placement = pos=(-0.8,0,5.7) rot=(0,1,0;3.14159rad)
  shape: bbox 0.5011 x 2.551 x 9.423 mm, 31 faces (baked)
FEATURE [Part::Feature] Part__Feature022  label="MINI USB CONTACT002"
  Placement = pos=(0,0,5.7) rot=(0,1,0;3.14159rad)
  shape: bbox 0.5011 x 2.551 x 9.423 mm, 31 faces (baked)
FEATURE [Part::Feature] Part__Feature023  label="MINI USB CONTACT003"
  Placement = pos=(0.8,0,5.7) rot=(0,1,0;3.14159rad)
  shape: bbox 0.5011 x 2.551 x 9.423 mm, 31 faces (baked)
FEATURE [Part::Feature] Part__Feature024  label="MINI USB CONTACT004"
  Placement = pos=(1.6,0,5.7) rot=(0,1,0;3.14159rad)
  shape: bbox 0.5011 x 2.551 x 9.423 mm, 31 faces (baked)
FEATURE [App::Part] MINIUSB___MEASURED  label="MINIUSB - MEASURED"
  Group = -> [Part__Feature018,Part__Feature019,Part__Feature020,Part__Feature021,Part__Feature022,Part__Feature023,Part__Feature024]
  Origin = -> Origin015
  Placement = pos=(38.98,1.65,-7.62) rot=(0,-1,0;1.5708rad)
FEATURE [Part::Feature] Part__Feature025  label="cap106C"
  Placement = pos=(37.2,0,-3.3) rot=(0.707107,0,0.707107;3.14159rad)
  shape: bbox 4.001 x 1.811 x 1.701 mm, 124 faces (baked)
FEATURE [Part::Feature] Part__Feature026  label="cap106C001"
  Placement = pos=(7.9,-1e-15,-5.6) rot=(0.707107,0,-0.707107;3.14159rad)
  shape: bbox 4.001 x 1.811 x 1.701 mm, 124 faces (baked)
FEATURE [Part::Feature] Part__Feature027  label="reset core"
  shape: bbox 5.2 x 2.15 x 2.8 mm, 77 faces (baked)
FEATURE [Part::Feature] Part__Feature028  label="reset shell"
  Placement = pos=(0,1.65,0) rot=(0,-1,0;1.5708rad)
  shape: bbox 4 x 1.65 x 3 mm, 100 faces (baked)
FEATURE [App::Part] reset_button  label="reset button"
  Group = -> [Part__Feature027,Part__Feature028]
  Origin = -> Origin016
  Placement = pos=(15.25,1.6,-8.05) rot=(0,1,0;1.5708rad)
FEATURE [Part::Feature] Part__Feature029  label="nano - reg"
  Placement = pos=(6.1,0,-10.16) rot=(0.707107,0,-0.707107;3.14159rad)
  shape: bbox 8.3 x 1.689 x 6.5 mm, 198 faces (baked)
FEATURE [Part::Feature] Part__Feature030  label="NANO DIODE"
  Placement = pos=(11.43,0,-4.2) rot=(0.707107,0,0.707107;3.14159rad)
  shape: bbox 1.7 x 1.384 x 4.916 mm, 85 faces (baked)
FEATURE [Part::Feature] Part__Feature031  label="189 RESISTOR PACK"
  Placement = pos=(15.75,0,-10.85) rot=(0.707107,0,0.707107;3.14159rad)
  shape: bbox 3 x 0.5573 x 3.2 mm, 288 faces, 10 solids (baked)
FEATURE [Part::Feature] Part__Feature032  label="102 RESISTOR PACK"
  Placement = pos=(15.75,0,-5.2) rot=(0.707107,0,0.707107;3.14159rad)
  shape: bbox 3 x 0.5573 x 3.2 mm, 277 faces, 10 solids (baked)
FEATURE [App::Part] arduino_nano  label="arduino nano"
  Group = -> [Part__Feature,Part__Feature001,Part__Feature002,Part__Feature003,Part__Feature004,Part__Feature005,Part__Feature006,Part__Feature007,Part__Feature008,Part__Feature009,Part__Feature010,Part__Feature011,Part__Feature012,Part__Feature013,Part__Feature014,Part__Feature015,Part__Feature016,Part__Feature017,MINIUSB___MEASURED,Part__Feature025,Part__Feature026,reset_button,Part__Feature029,+3 more]
  Origin = -> Origin017
  Placement = pos=(-8,22,-17) rot=(-0.57735,0.57735,0.57735;4.18879rad)
FEATURE [PartDesign::Pocket] Pocket020
  BaseFeature = -> Fillet017
  Length = 5
  Length2 = 100
  Profile = -> Sketch041
  Type = 0
FEATURE [Sketcher::SketchObject] Sketch042
  MapMode = 5
  Placement = pos=(0,0,0) rot=(1,0,0;3.14159rad)
  Support = -> [Pocket020]
  sketch-geometry (8):
    g0: LineSegment StartX=14.5 StartY=-10 StartZ=0 EndX=21.5 EndY=-10 EndZ=0
    g1: LineSegment StartX=21.5 StartY=-10 StartZ=0 EndX=21.5 EndY=-20 EndZ=0
    g2: LineSegment StartX=21.5 StartY=-20 StartZ=0 EndX=14.5 EndY=-20 EndZ=0
    g3: LineSegment StartX=14.5 StartY=-20 StartZ=0 EndX=14.5 EndY=-10 EndZ=0
    g4: LineSegment StartX=-14.5 StartY=-10 StartZ=0 EndX=-21.5 EndY=-10 EndZ=0
    g5: LineSegment StartX=-21.5 StartY=-10 StartZ=0 EndX=-21.5 EndY=-20 EndZ=0
    g6: LineSegment StartX=-21.5 StartY=-20 StartZ=0 EndX=-14.5 EndY=-20 EndZ=0
    g7: LineSegment StartX=-14.5 StartY=-20 StartZ=0 EndX=-14.5 EndY=-10 EndZ=0
  constraints (23):
    c: Coincident(g0,g1)
    c: Coincident(g1,g2)
    c: Coincident(g2,g3)
    c: Coincident(g3,g0)
    c: Horizontal(g0)
    c: Horizontal(g2)
    c: Vertical(g1)
    c: Vertical(g3)
    c: DistanceY(g3,g3) = 10
    c: DistanceX(g0,g0) = 7
    c: DistanceX(g1) = 21.5
    c: DistanceY(g0) = -10
    c: Coincident(g4,g5)
    c: Coincident(g5,g6)
    c: Coincident(g6,g7)
    c: Coincident(g7,g4)
    c: Horizontal(g4)
    c: Horizontal(g6)
    c: Vertical(g5)
    c: Vertical(g7)
    c: Equal(g0,g4)
    c: Equal(g7,g1)
    c: Symmetric(g4,g0,g-2)
FEATURE [PartDesign::Pad] Pad020
  BaseFeature = -> Pocket020
  Length = 6
  Length2 = 100
  Profile = -> Sketch042
  Type = 0
FEATURE [Sketcher::SketchObject] Sketch044
  ExternalGeometry = -> [Pad020]
  MapMode = 5
  Placement = pos=(0,0,-6) rot=(1,0,0;3.14159rad)
  Support = -> [Pad020]
  sketch-geometry (11):
    g0: Circle CenterX=-19.2 CenterY=-12.5 CenterZ=0 NormalX=0 NormalY=0 NormalZ=1 AngleXU=0 Radius=0.5
    g1: Circle CenterX=-16.65 CenterY=-12.5 CenterZ=0 NormalX=0 NormalY=0 NormalZ=1 AngleXU=0 Radius=0.5
    g2: LineSegment [constr] StartX=-19.2 StartY=-12.5 StartZ=0 EndX=-16.65 EndY=-12.5 EndZ=0
    g3: Circle CenterX=-19.2 CenterY=-15.05 CenterZ=0 NormalX=0 NormalY=0 NormalZ=1 AngleXU=0 Radius=0.5
    g4: LineSegment [constr] StartX=-19.2 StartY=-12.5 StartZ=0 EndX=-19.2 EndY=-15.05 EndZ=0
    g5: Circle CenterX=-16.65 CenterY=-15.05 CenterZ=0 NormalX=0 NormalY=0 NormalZ=1 AngleXU=0 Radius=0.5
    g6: LineSegment [constr] StartX=-19.2 StartY=-15.05 StartZ=0 EndX=-16.65 EndY=-15.05 EndZ=0
    g7: Circle CenterX=-19.2 CenterY=-17.6 CenterZ=0 NormalX=0 NormalY=0 NormalZ=1 AngleXU=0 Radius=0.5
    g8: LineSegment [constr] StartX=-19.2 StartY=-15.05 StartZ=0 EndX=-19.2 EndY=-17.6 EndZ=0
    g9: Circle CenterX=-16.65 CenterY=-17.6 CenterZ=0 NormalX=0 NormalY=0 NormalZ=1 AngleXU=0 Radius=0.5
    g10: LineSegment [constr] StartX=-19.2 StartY=-17.6 StartZ=0 EndX=-16.65 EndY=-17.6 EndZ=0
  constraints (28):
    c: Coincident(g0,g2)
    c: Coincident(g1,g2)
    c: Angle(g2) = 0
    c: Coincident(g0,g4)
    c: Coincident(g3,g4)
    c: Equal(g4,g2)
    c: Perpendicular(g4,g2)
    c: Coincident(g3,g6)
    c: Coincident(g5,g6)
    c: Equal(g2,g6)
    c: Parallel(g6,g2)
    c: Coincident(g3,g8)
    c: Coincident(g7,g8)
    c: Equal(g4,g8)
    c: Perpendicular(g8,g2)
    c: Coincident(g7,g10)
    c: Coincident(g9,g10)
    c: Equal(g2,g10)
    c: Parallel(g10,g2)
    c: Equal(g0,g1)
    c: Equal(g1,g5)
    c: Equal(g5,g3)
    c: Equal(g3,g7)
    c: Equal(g7,g9)
    c: Diameter(g9) = 1
    c: DistanceX(g0,g1) = 2.55
    c: DistanceY(g0,g-3) = 2.5
    c: DistanceX(g-3,g0) = 2.3
FEATURE [PartDesign::Pocket] Pocket021
  BaseFeature = -> Pad020
  Length = 6
  Length2 = 100
  Profile = -> Sketch044
  Type = 0
FEATURE [Sketcher::SketchObject] Sketch045
  ExternalGeometry = -> [Pocket021]
  MapMode = 5
  Placement = pos=(0,0,0) rot=(1,0,0;3.14159rad)
  Support = -> [Pocket021]
  sketch-geometry (1):
    g0: Circle CenterX=0 CenterY=84.4948 CenterZ=0 NormalX=0 NormalY=0 NormalZ=1 AngleXU=0 Radius=30
  constraints (3):
    c: PointOnObject(g0,g-2)
    c: Diameter(g0) = 60
    c: DistanceY(g-3,g0) = 46
FEATURE [PartDesign::Pocket] Pocket022
  BaseFeature = -> Pocket021
  Length = 7
  Length2 = 100
  Profile = -> Sketch045
  Type = 0
FEATURE [PartDesign::Body] Body014  label="dashDisplaySmallLid"
  Group = -> [Sketch038,Pad019,Fillet016,Sketch039,Pocket019,Fillet017,Sketch041,Pocket020,Sketch042,Pad020,Sketch044,Pocket021,Sketch045,Pocket022]
  Origin = -> Origin014
  Placement = pos=(0,0,-2) rot=(0,0,1;0rad)
  Tip = -> Pocket022
FEATURE [TechDraw::DrawViewDimension] Dimension038
  Arbitrary = false
  FormatSpec = ⌀%.2f
  LockPosition = false
  MeasureType = 1
  OverTolerance = 0
  References2D = -> [View]
  Rotation = 0
  ScaleType = 0
  Type = 5
  UnderTolerance = 0
  X = 20.1311
  Y = 9.1505
FEATURE [TechDraw::DrawPage] Page  label="dashboard"
  KeepUpdated = true
  ProjectionType = 0
  Template = -> Template
  Views = -> [View,Dimension,Dimension001,Dimension002,Dimension004,Dimension005,Dimension006,Dimension007,Dimension008,Dimension009,Dimension010,Dimension011,Dimension012,Dimension013,Dimension015,Dimension016,Dimension017,Dimension018,Dimension019,Dimension021,Dimension022,Dimension024,Dimension025,Dimension026,Dimension027,Dimension028,Dimension029,Dimension030,Dimension031,Dimension032,Dimension033,+5 more]
FEATURE [Sketcher::SketchObject] Sketch046
  MapMode = 5
  Support = -> [XY_Plane018]
  sketch-geometry (34):
    g0: LineSegment StartX=-35 StartY=80 StartZ=0 EndX=35 EndY=80 EndZ=0
    g1: LineSegment StartX=35 StartY=80 StartZ=0 EndX=35 EndY=-80 EndZ=0
    g2: LineSegment StartX=35 StartY=-80 StartZ=0 EndX=-35 EndY=-80 EndZ=0
    g3: LineSegment StartX=-35 StartY=-80 StartZ=0 EndX=-35 EndY=80 EndZ=0
    g4: LineSegment [constr] StartX=-31 StartY=70 StartZ=0 EndX=31 EndY=70 EndZ=0
    g5: LineSegment [constr] StartX=31 StartY=70 StartZ=0 EndX=31 EndY=-70 EndZ=0
    g6: LineSegment [constr] StartX=31 StartY=-70 StartZ=0 EndX=-31 EndY=-70 EndZ=0
    g7: LineSegment [constr] StartX=-31 StartY=-70 StartZ=0 EndX=-31 EndY=70 EndZ=0
    g8: Circle CenterX=-29 CenterY=75 CenterZ=0 NormalX=0 NormalY=0 NormalZ=1 AngleXU=0 Radius=2.8
    g9: Circle CenterX=29 CenterY=75 CenterZ=0 NormalX=0 NormalY=0 NormalZ=1 AngleXU=0 Radius=2.8
    g10: Circle CenterX=-29 CenterY=-75 CenterZ=0 NormalX=0 NormalY=0 NormalZ=1 AngleXU=0 Radius=2.8
    g11: Circle CenterX=29 CenterY=-75 CenterZ=0 NormalX=0 NormalY=0 NormalZ=1 AngleXU=0 Radius=2.8
    g12: Circle CenterX=0 CenterY=-60 CenterZ=0 NormalX=0 NormalY=0 NormalZ=1 AngleXU=0 Radius=6.15
    g13: Circle CenterX=0 CenterY=-20 CenterZ=0 NormalX=0 NormalY=0 NormalZ=1 AngleXU=0 Radius=6.15
    g14: Circle CenterX=0 CenterY=-40 CenterZ=0 NormalX=0 NormalY=0 NormalZ=1 AngleXU=0 Radius=7.15
    g15: Circle CenterX=20 CenterY=-40 CenterZ=0 NormalX=0 NormalY=0 NormalZ=1 AngleXU=0 Radius=6.15
    g16: Circle CenterX=-20 CenterY=-40 CenterZ=0 NormalX=0 NormalY=0 NormalZ=1 AngleXU=0 Radius=6.15
    g17: Circle [constr] CenterX=-20 CenterY=-40 CenterZ=0 NormalX=0 NormalY=0 NormalZ=1 AngleXU=0 Radius=7.6
    g18: Circle [constr] CenterX=0 CenterY=-40 CenterZ=0 NormalX=0 NormalY=0 NormalZ=1 AngleXU=0 Radius=9
    g19: Circle [constr] CenterX=20 CenterY=-40 CenterZ=0 NormalX=0 NormalY=0 NormalZ=1 AngleXU=0 Radius=7.6
    g20: Circle [constr] CenterX=0 CenterY=-60 CenterZ=0 NormalX=0 NormalY=0 NormalZ=1 AngleXU=0 Radius=7.6
    g21: Circle [constr] CenterX=0 CenterY=-20 CenterZ=0 NormalX=0 NormalY=0 NormalZ=1 AngleXU=0 Radius=7.6
    g22: Circle CenterX=-16 CenterY=58 CenterZ=0 NormalX=0 NormalY=0 NormalZ=1 AngleXU=0 Radius=6.15
    g23: Circle CenterX=16 CenterY=58 CenterZ=0 NormalX=0 NormalY=0 NormalZ=1 AngleXU=0 Radius=6.15
    g24: Circle CenterX=-16 CenterY=31 CenterZ=0 NormalX=0 NormalY=0 NormalZ=1 AngleXU=0 Radius=6.15
    g25: Circle CenterX=16 CenterY=31 CenterZ=0 NormalX=0 NormalY=0 NormalZ=1 AngleXU=0 Radius=6.15
    g26: Circle CenterX=-16 CenterY=4 CenterZ=0 NormalX=0 NormalY=0 NormalZ=1 AngleXU=0 Radius=6.15
    g27: Circle CenterX=16 CenterY=4 CenterZ=0 NormalX=0 NormalY=0 NormalZ=1 AngleXU=0 Radius=6.15
    g28: Circle [constr] CenterX=-16 CenterY=4 CenterZ=0 NormalX=0 NormalY=0 NormalZ=1 AngleXU=0 Radius=8.5
    g29: Circle [constr] CenterX=-16 CenterY=31 CenterZ=0 NormalX=0 NormalY=0 NormalZ=1 AngleXU=0 Radius=8.5
    g30: Circle [constr] CenterX=-16 CenterY=58 CenterZ=0 NormalX=0 NormalY=0 NormalZ=1 AngleXU=0 Radius=8.5
    g31: Circle [constr] CenterX=16 CenterY=58 CenterZ=0 NormalX=0 NormalY=0 NormalZ=1 AngleXU=0 Radius=8.5
    g32: Circle [constr] CenterX=16 CenterY=31 CenterZ=0 NormalX=0 NormalY=0 NormalZ=1 AngleXU=0 Radius=8.5
    g33: Circle [constr] CenterX=16 CenterY=4 CenterZ=0 NormalX=0 NormalY=0 NormalZ=1 AngleXU=0 Radius=8.5
  constraints (81):
    c: Coincident(g0,g1)
    c: Coincident(g1,g2)
    c: Coincident(g2,g3)
    c: Coincident(g3,g0)
    c: Horizontal(g0)
    c: Horizontal(g2)
    c: Vertical(g1)
    c: Vertical(g3)
    c: Symmetric(g0,g1,g-1)
    c: DistanceX(g0,g0) = 70
    c: DistanceY(g1,g1) = 160
    c: Coincident(g4,g5)
    c: Coincident(g5,g6)
    c: Coincident(g6,g7)
    c: Coincident(g7,g4)
    c: Horizontal(g4)
    c: Horizontal(g6)
    c: Vertical(g5)
    c: Vertical(g7)
    c: Symmetric(g5,g4,g-1)
    c: DistanceX(g4,g4) = 62
    c: DistanceY(g5,g5) = 140
    c: Equal(g10,g11)
    c: Equal(g11,g8)
    c: Equal(g8,g9)
    c: Symmetric(g8,g9,g-2)
    c: Symmetric(g8,g10,g-1)
    c: Symmetric(g10,g11,g-2)
    c: DistanceX(g9,g0) = 6
    c: DistanceY(g9,g0) = 5
    c: Radius(g9) = 2.8
    c: PointOnObject(g12,g-2)
    c: PointOnObject(g13,g-2)
    c: Horizontal(g16,g14)
    c: Symmetric(g16,g15,g-2)
    c: Equal(g16,g13)
    c: Equal(g15,g12)
    c: Radius(g16) = 6.15
    c: Symmetric(g13,g12,g14)
    c: DistanceX(g16,g15) = 40
    c: DistanceY(g12,g13) = 40
    c: Coincident(g17,g16)
    c: Coincident(g18,g14)
    c: Coincident(g19,g15)
    c: Coincident(g20,g12)
    c: Coincident(g21,g13)
    c: Equal(g17,g21)
    c: Equal(g20,g19)
    c: Radius(g17) = 7.6
    c: DistanceY(g13) = -20
    c: Equal(g17,g19)
    c: Equal(g15,g16)
    c: Radius(g14) = 7.15
    c: Radius(g18) = 9
    c: Equal(g16,g26)
    c: Equal(g26,g24)
    c: Equal(g24,g22)
    c: Equal(g22,g23)
    c: Equal(g23,g25)
    c: Equal(g25,g27)
    c: Vertical(g22,g24)
    c: Vertical(g24,g26)
    c: Symmetric(g22,g23,g-2)
    c: Symmetric(g24,g25,g-2)
    c: Symmetric(g27,g26,g-2)
    c: Coincident(g28,g26)
    c: Coincident(g29,g24)
    c: Coincident(g30,g22)
    c: Coincident(g31,g23)
    c: Coincident(g32,g25)
    c: Coincident(g33,g27)
    c: Equal(g28,g29)
    c: Equal(g29,g30)
    c: Equal(g30,g31)
    c: Equal(g31,g32)
    c: Equal(g32,g33)
    c: Radius(g33) = 8.5
    c: DistanceY(g24,g22) = 27
    c: DistanceY(g26,g24) = 27
    c: DistanceY(g22,g4) = 12
    c: DistanceX(g22,g23) = 32
FEATURE [PartDesign::Pad] Pad021
  Length = 3
  Length2 = 100
  Profile = -> Sketch046
  Type = 0
FEATURE [Sketcher::SketchObject] Sketch047
  MapMode = 5
  Placement = pos=(0,0,0) rot=(1,0,0;3.14159rad)
  Support = -> [Pad021]
  sketch-geometry (8):
    g0: LineSegment StartX=-31 StartY=68.5 StartZ=0 EndX=31 EndY=68.5 EndZ=0
    g1: LineSegment StartX=31 StartY=68.5 StartZ=0 EndX=31 EndY=-68.5 EndZ=0
    g2: LineSegment StartX=31 StartY=-68.5 StartZ=0 EndX=-31 EndY=-68.5 EndZ=0
    g3: LineSegment StartX=-31 StartY=-68.5 StartZ=0 EndX=-31 EndY=68.5 EndZ=0
    g4: LineSegment StartX=-32.5 StartY=70 StartZ=0 EndX=32.5 EndY=70 EndZ=0
    g5: LineSegment StartX=32.5 StartY=70 StartZ=0 EndX=32.5 EndY=-70 EndZ=0
    g6: LineSegment StartX=32.5 StartY=-70 StartZ=0 EndX=-32.5 EndY=-70 EndZ=0
    g7: LineSegment StartX=-32.5 StartY=-70 StartZ=0 EndX=-32.5 EndY=70 EndZ=0
  constraints (22):
    c: Coincident(g0,g1)
    c: Coincident(g1,g2)
    c: Coincident(g2,g3)
    c: Coincident(g3,g0)
    c: Horizontal(g0)
    c: Horizontal(g2)
    c: Vertical(g1)
    c: Vertical(g3)
    c: Symmetric(g0,g1,g-1)
    c: Coincident(g4,g5)
    c: Coincident(g5,g6)
    c: Coincident(g6,g7)
    c: Coincident(g7,g4)
    c: Horizontal(g4)
    c: Horizontal(g6)
    c: Vertical(g5)
    c: Vertical(g7)
    c: Symmetric(g5,g4,g-1)
    c: DistanceX(g4,g4) = 65
    c: DistanceX(g2,g2) = 62
    c: DistanceY(g5,g5) = 140
    c: DistanceY(g3,g3) = 137
FEATURE [PartDesign::Pad] Pad022
  BaseFeature = -> Pad021
  Length = 7
  Length2 = 100
  Profile = -> Sketch047
  Type = 0
FEATURE [PartDesign::Fillet] Fillet018
  Base = -> Pad022 [Edge77,Edge76,Edge74,Edge75]
  BaseFeature = -> Pad022
  Radius = 1
FEATURE [PartDesign::Fillet] Fillet019
  Base = -> Fillet018 [Edge66,Edge67,Edge71,Edge69]
  BaseFeature = -> Fillet018
  Radius = 5
FEATURE [PartDesign::Fillet] Fillet020
  Base = -> Fillet019 [Edge79,Edge83,Edge78,Edge81]
  BaseFeature = -> Fillet019
  Radius = 2
FEATURE [PartDesign::Body] Body015  label="addOnPanel"
  Group = -> [Sketch046,Pad021,Sketch047,Pad022,Fillet018,Fillet019,Fillet020]
  Origin = -> Origin018
  Tip = -> Fillet020
FEATURE [Sketcher::SketchObject] Sketch048
  MapMode = 5
  Support = -> [XY_Plane019]
  sketch-geometry (4):
    g0: LineSegment StartX=0 StartY=4.5 StartZ=0 EndX=-8.5 EndY=-4 EndZ=0
    g1: LineSegment StartX=-8.5 StartY=-4 StartZ=0 EndX=8.5 EndY=-4 EndZ=0
    g2: LineSegment StartX=8.5 StartY=-4 StartZ=0 EndX=0 EndY=4.5 EndZ=0
    g3: Circle CenterX=0 CenterY=0 CenterZ=0 NormalX=0 NormalY=0 NormalZ=1 AngleXU=0 Radius=1.7
  constraints (10):
    c: PointOnObject(g0,g-2)
    c: Coincident(g0,g1)
    c: Coincident(g1,g2)
    c: Coincident(g2,g0)
    c: DistanceY(g0) = 4.5
    c: Angle(g0,g2) = 1.5708
    c: Symmetric(g0,g1,g-2)
    c: Coincident(g3,g-1)
    c: Radius(g3) = 1.7
    c: DistanceY(g1,g0) = 8.5
FEATURE [PartDesign::Pad] Pad023
  Length = 17
  Length2 = 100
  Profile = -> Sketch048
  Type = 0
FEATURE [PartDesign::SubtractiveBox] Box
  AttacherType = Attacher::AttachEngine3D
  AttachmentOffset = pos=(-3,-6,12) rot=(0,0,1;0rad)
  BaseFeature = -> Pad023
  Height = 2.55
  Length = 6
  MapMode = 5
  Placement = pos=(-3,-6,12) rot=(0,0,1;0rad)
  Support = -> [XY_Plane019]
  Width = 20
FEATURE [Sketcher::SketchObject] Sketch049
  MapMode = 5
  Support = -> [XY_Plane020]
  sketch-geometry (4):
    g0: LineSegment StartX=0 StartY=4.5 StartZ=0 EndX=-8.5 EndY=-4 EndZ=0
    g1: LineSegment StartX=-8.5 StartY=-4 StartZ=0 EndX=8.5 EndY=-4 EndZ=0
    g2: LineSegment StartX=8.5 StartY=-4 StartZ=0 EndX=0 EndY=4.5 EndZ=0
    g3: Circle CenterX=0 CenterY=0 CenterZ=0 NormalX=0 NormalY=0 NormalZ=1 AngleXU=0 Radius=1.7
  constraints (10):
    c: PointOnObject(g0,g-2)
    c: Coincident(g0,g1)
    c: Coincident(g1,g2)
    c: Coincident(g2,g0)
    c: DistanceY(g0) = 4.5
    c: Angle(g0,g2) = 1.5708
    c: Symmetric(g0,g1,g-2)
    c: Coincident(g3,g-1)
    c: Radius(g3) = 1.7
    c: DistanceY(g1,g0) = 8.5
FEATURE [PartDesign::Pad] Pad024
  Length = 4
  Length2 = 100
  Profile = -> Sketch049
  Type = 0
FEATURE [PartDesign::Body] Body017  label="cornerNutHolder001"
  Group = -> [Sketch049,Pad024]
  Origin = -> Origin020
  Tip = -> Pad024
FEATURE [PartDesign::SubtractiveBox] Box001
  AttacherType = Attacher::AttachEngine3D
  AttachmentOffset = pos=(0,-12,-20) rot=(0,0,1;0.785398rad)
  BaseFeature = -> Box
  Height = 30
  Length = 10
  MapMode = 5
  Placement = pos=(0,-12,-20) rot=(0,0,1;0.785398rad)
  Support = -> [XY_Plane019]
  Width = 10
FEATURE [PartDesign::SubtractiveCylinder] Cylinder
  Angle = 360
  AttacherType = Attacher::AttachEngine3D
  AttachmentOffset = pos=(2,5,4) rot=(0,1,0;2.35619rad)
  BaseFeature = -> Box001
  Height = 10
  MapMode = 5
  Placement = pos=(2,-4,5) rot=(0.281085,0.678598,0.678598;2.59356rad)
  Radius = 1.7
  Support = -> [XZ_Plane019]
FEATURE [PartDesign::SubtractiveCylinder] Cylinder001
  Angle = 360
  AttacherType = Attacher::AttachEngine3D
  AttachmentOffset = pos=(-10,4,-4) rot=(0,1,0;0.785398rad)
  BaseFeature = -> Cylinder
  Height = 11
  MapMode = 5
  Placement = pos=(-10,4,4) rot=(0.862856,0.357407,0.357407;1.71777rad)
  Radius = 1.7
  Support = -> [XZ_Plane019]
FEATURE [PartDesign::Body] Body016  label="cornerNutHolder"
  Group = -> [Sketch048,Pad023,Box,Box001,Cylinder,Cylinder001]
  Origin = -> Origin019
  Tip = -> Cylinder001
FEATURE [Sketcher::SketchObject] Sketch050
  MapMode = 5
  Support = -> [XY_Plane021]
  sketch-geometry (5):
    g0: Circle CenterX=0 CenterY=0 CenterZ=0 NormalX=0 NormalY=0 NormalZ=1 AngleXU=0 Radius=1.7
    g1: LineSegment StartX=-7.5 StartY=4.5 StartZ=0 EndX=7.5 EndY=4.5 EndZ=0
    g2: LineSegment StartX=7.5 StartY=4.5 StartZ=0 EndX=7.5 EndY=-4.5 EndZ=0
    g3: LineSegment StartX=7.5 StartY=-4.5 StartZ=0 EndX=-7.5 EndY=-4.5 EndZ=0
    g4: LineSegment StartX=-7.5 StartY=-4.5 StartZ=0 EndX=-7.5 EndY=4.5 EndZ=0
  constraints (13):
    c: Coincident(g0,g-1)
    c: Radius(g0) = 1.7
    c: Coincident(g1,g2)
    c: Coincident(g2,g3)
    c: Coincident(g3,g4)
    c: Coincident(g4,g1)
    c: Horizontal(g1)
    c: Horizontal(g3)
    c: Vertical(g2)
    c: Vertical(g4)
    c: Symmetric(g2,g1,g0)
    c: DistanceY(g1) = 4.5
    c: DistanceX(g3,g3) = 15
FEATURE [PartDesign::Pad] Pad025
  Length = 17
  Length2 = 100
  Profile = -> Sketch050
  Type = 0
FEATURE [PartDesign::SubtractiveBox] Box002
  AttacherType = Attacher::AttachEngine3D
  AttachmentOffset = pos=(-3,-6.5,12) rot=(0,0,1;0rad)
  BaseFeature = -> Pad025
  Height = 2.8
  Length = 6
  MapMode = 5
  Placement = pos=(-3,-6.5,12) rot=(0,0,1;0rad)
  Support = -> [XY_Plane021]
  Width = 10
FEATURE [PartDesign::SubtractiveBox] Box003
  AttacherType = Attacher::AttachEngine3D
  AttachmentOffset = pos=(-8,-8,-2) rot=(0,0,1;0rad)
  BaseFeature = -> Box002
  Height = 12
  Length = 17
  MapMode = 5
  Placement = pos=(-8,-8,-2) rot=(0,0,1;0rad)
  Support = -> [XY_Plane021]
  Width = 10
FEATURE [PartDesign::SubtractiveCylinder] Cylinder002
  Angle = 360
  AttacherType = Attacher::AttachEngine3D
  AttachmentOffset = pos=(-4,5,-7) rot=(0,0,1;0rad)
  BaseFeature = -> Box003
  Height = 10
  MapMode = 5
  Placement = pos=(-4,7,5) rot=(1,0,0;1.5708rad)
  Radius = 1.7
  Support = -> [XZ_Plane021]
FEATURE [PartDesign::SubtractiveCylinder] Cylinder003
  Angle = 360
  AttacherType = Attacher::AttachEngine3D
  AttachmentOffset = pos=(4,5,-7) rot=(0,0,1;0rad)
  BaseFeature = -> Cylinder002
  Height = 10
  MapMode = 5
  Placement = pos=(4,7,5) rot=(1,0,0;1.5708rad)
  Radius = 1.7
  Support = -> [XZ_Plane021]
FEATURE [PartDesign::Body] Body018  label="nutHolderStraight"
  Group = -> [Sketch050,Pad025,Box002,Box003,Cylinder002,Cylinder003]
  Origin = -> Origin021
  Tip = -> Cylinder003
FEATURE [Sketcher::SketchObject] Sketch051
  MapMode = 5
  Placement = pos=(0,0,0) rot=(1,0,0;1.5708rad)
  Support = -> [XZ_Plane022]
  sketch-geometry (7):
    g0: LineSegment StartX=0 StartY=0 StartZ=0 EndX=0 EndY=20 EndZ=0
    g1: LineSegment StartX=0 StartY=20 StartZ=0 EndX=20 EndY=20 EndZ=0
    g2: LineSegment StartX=20 StartY=20 StartZ=0 EndX=68.2963 EndY=7.05905 EndZ=0
    g3: LineSegment StartX=68.2963 StartY=7.05905 StartZ=0 EndX=71.7638 EndY=20 EndZ=0
    g4: LineSegment StartX=71.7638 StartY=20 StartZ=0 EndX=110 EndY=20 EndZ=0
    g5: LineSegment StartX=110 StartY=20 StartZ=0 EndX=110 EndY=0 EndZ=0
    g6: LineSegment StartX=110 StartY=0 StartZ=0 EndX=0 EndY=0 EndZ=0
  constraints (20):
    c: Coincident(g-1,g0)
    c: Vertical(g0)
    c: Coincident(g0,g1)
    c: Horizontal(g1)
    c: Coincident(g1,g2)
    c: Coincident(g2,g3)
    c: Coincident(g3,g4)
    c: Horizontal(g4)
    c: Coincident(g4,g5)
    c: PointOnObject(g5,g-1)
    c: Vertical(g5)
    c: Coincident(g5,g6)
    c: Coincident(g6,g0)
    c: Perpendicular(g2,g3)
    c: Angle(g1,g2) = 2.87979
    c: Distance(g2) = 50
    c: Horizontal(g3,g1)
    c: DistanceX(g6,g6) = 110
    c: DistanceY(g5,g5) = 20
    c: DistanceX(g1,g1) = 20
FEATURE [PartDesign::Pad] Pad026
  Length = 130
  Length2 = 100
  Placement = pos=(0,0,0) rot=(1,0,0;1.5708rad)
  Profile = -> Sketch051
  Type = 0
FEATURE [PartDesign::SubtractiveCylinder] Cylinder004
  Angle = 360
  AttacherType = Attacher::AttachEngine3D
  AttachmentOffset = pos=(9,-10,0) rot=(0,0,1;0rad)
  BaseFeature = -> Pad026
  Height = 30
  MapMode = 5
  Placement = pos=(9,-10,0) rot=(0,0,1;0rad)
  Radius = 2.7
  Support = -> [XY_Plane022]
FEATURE [PartDesign::SubtractiveCylinder] Cylinder005
  Angle = 360
  AttacherType = Attacher::AttachEngine3D
  AttachmentOffset = pos=(95,-20,0) rot=(0,0,1;0rad)
  BaseFeature = -> Cylinder004
  Height = 30
  MapMode = 5
  Placement = pos=(95,-20,0) rot=(0,0,1;0rad)
  Radius = 2.7
  Support = -> [XY_Plane022]
FEATURE [PartDesign::SubtractiveCylinder] Cylinder006
  Angle = 360
  AttacherType = Attacher::AttachEngine3D
  AttachmentOffset = pos=(95,-65,0) rot=(0,0,1;0rad)
  BaseFeature = -> Cylinder005
  Height = 30
  MapMode = 5
  Placement = pos=(95,-65,0) rot=(0,0,1;0rad)
  Radius = 2.7
  Support = -> [XY_Plane022]
FEATURE [PartDesign::SubtractiveCylinder] Cylinder007
  Angle = 360
  AttacherType = Attacher::AttachEngine3D
  AttachmentOffset = pos=(95,-110,0) rot=(0,0,1;0rad)
  BaseFeature = -> Cylinder006
  Height = 30
  MapMode = 5
  Placement = pos=(95,-110,0) rot=(0,0,1;0rad)
  Radius = 2.7
  Support = -> [XY_Plane022]
FEATURE [PartDesign::SubtractiveCylinder] Cylinder008
  Angle = 360
  AttacherType = Attacher::AttachEngine3D
  AttachmentOffset = pos=(9,-65,0) rot=(0,0,1;0rad)
  BaseFeature = -> Cylinder007
  Height = 30
  MapMode = 5
  Placement = pos=(9,-65,0) rot=(0,0,1;0rad)
  Radius = 2.7
  Support = -> [XY_Plane022]
FEATURE [PartDesign::SubtractiveCylinder] Cylinder009
  Angle = 360
  AttacherType = Attacher::AttachEngine3D
  AttachmentOffset = pos=(9,-120,0) rot=(0,0,1;0rad)
  BaseFeature = -> Cylinder008
  Height = 30
  MapMode = 5
  Placement = pos=(9,-120,0) rot=(0,0,1;0rad)
  Radius = 2.7
  Support = -> [XY_Plane022]
FEATURE [PartDesign::SubtractiveCylinder] Cylinder010
  Angle = 360
  AttacherType = Attacher::AttachEngine3D
  AttachmentOffset = pos=(38,-35,-5) rot=(0,1,0;0.261799rad)
  BaseFeature = -> Cylinder009
  Height = 50
  MapMode = 5
  Placement = pos=(38,-35,-5) rot=(0,1,0;0.261799rad)
  Radius = 3.2
  Support = -> [XY_Plane022]
FEATURE [PartDesign::SubtractiveCylinder] Cylinder011
  Angle = 360
  AttacherType = Attacher::AttachEngine3D
  AttachmentOffset = pos=(38,-65,-5) rot=(0,1,0;0.261799rad)
  BaseFeature = -> Cylinder010
  Height = 40
  MapMode = 5
  Placement = pos=(38,-65,-5) rot=(0,1,0;0.261799rad)
  Radius = 3.2
  Support = -> [XY_Plane022]
FEATURE [PartDesign::SubtractiveCylinder] Cylinder012
  Angle = 360
  AttacherType = Attacher::AttachEngine3D
  AttachmentOffset = pos=(38,-100,-5) rot=(0,1,0;0.261799rad)
  BaseFeature = -> Cylinder011
  Height = 40
  MapMode = 5
  Placement = pos=(38,-100,-5) rot=(0,1,0;0.261799rad)
  Radius = 3.2
  Support = -> [XY_Plane022]
FEATURE [PartDesign::SubtractiveCylinder] Cylinder013
  Angle = 360
  AttacherType = Attacher::AttachEngine3D
  AttachmentOffset = pos=(38,-35,-5) rot=(0,1,0;0.261799rad)
  BaseFeature = -> Cylinder012
  Height = 13
  MapMode = 5
  Placement = pos=(38,-35,-5) rot=(0,1,0;0.261799rad)
  Radius = 7.5
  Support = -> [XY_Plane022]
FEATURE [PartDesign::SubtractiveCylinder] Cylinder014
  Angle = 360
  AttacherType = Attacher::AttachEngine3D
  AttachmentOffset = pos=(38,-65,-5) rot=(0,1,0;0.261799rad)
  BaseFeature = -> Cylinder013
  Height = 13
  MapMode = 5
  Placement = pos=(38,-65,-5) rot=(0,1,0;0.261799rad)
  Radius = 7.5
  Support = -> [XY_Plane022]
FEATURE [PartDesign::SubtractiveCylinder] Cylinder015
  Angle = 360
  AttacherType = Attacher::AttachEngine3D
  AttachmentOffset = pos=(38,-100,-5) rot=(0,1,0;0.261799rad)
  BaseFeature = -> Cylinder014
  Height = 13
  MapMode = 5
  Placement = pos=(38,-100,-5) rot=(0,1,0;0.261799rad)
  Radius = 7.5
  Support = -> [XY_Plane022]
FEATURE [PartDesign::Fillet] Fillet021
  Base = -> Cylinder015 [Edge2,Edge31,Edge4,Edge30,Edge3,Edge26,Edge29,Edge25,Edge18,Edge17]
  BaseFeature = -> Cylinder015
  Placement = pos=(38,-100,-5) rot=(0,1,0;0.261799rad)
  Radius = 3
FEATURE [PartDesign::Body] Body019  label="panelBoxMount"
  Group = -> [Sketch051,Pad026,Cylinder004,Cylinder005,Cylinder006,Cylinder007,Cylinder008,Cylinder009,Cylinder010,Cylinder011,Cylinder012,Cylinder013,Cylinder014,Cylinder015,Fillet021]
  Origin = -> Origin022
  Tip = -> Fillet021
FEATURE [Sketcher::SketchObject] Sketch052
  MapMode = 5
  Support = -> [XY_Plane023]
  sketch-geometry (8):
    g0: LineSegment StartX=0 StartY=0 StartZ=0 EndX=0 EndY=60 EndZ=0
    g1: LineSegment StartX=0 StartY=60 StartZ=0 EndX=110 EndY=60 EndZ=0
    g2: LineSegment StartX=110 StartY=60 StartZ=0 EndX=110 EndY=40 EndZ=0
    g3: ArcOfCircle CenterX=110 CenterY=-81.25 CenterZ=0 NormalX=0 NormalY=0 NormalZ=1 AngleXU=0 Radius=121.25 StartAngle=1.5708 EndAngle=2.40724
    g4: LineSegment StartX=20 StartY=1.42e-14 StartZ=0 EndX=0 EndY=0 EndZ=0
    g5: Circle CenterX=25 CenterY=35 CenterZ=0 NormalX=0 NormalY=0 NormalZ=1 AngleXU=0 Radius=13
    g6: Circle CenterX=58 CenterY=43 CenterZ=0 NormalX=0 NormalY=0 NormalZ=1 AngleXU=0 Radius=6
    g7: Circle CenterX=85 CenterY=45 CenterZ=0 NormalX=0 NormalY=0 NormalZ=1 AngleXU=0 Radius=4
  constraints (23):
    c: Coincident(g-1,g0)
    c: Vertical(g0)
    c: Coincident(g0,g1)
    c: Horizontal(g1)
    c: Coincident(g1,g2)
    c: Vertical(g2)
    c: Perpendicular(g2,g3) = 4.71239
    c: Coincident(g4,g3)
    c: Coincident(g4,g0)
    c: DistanceY(g0,g0) = 60
    c: DistanceX(g1,g1) = 110
    c: PointOnObject(g3,g-1)
    c: Equal(g2,g4)
    c: DistanceX(g4,g4) = 20
    c: Radius(g5) = 13
    c: Radius(g6) = 6
    c: Radius(g7) = 4
    c: DistanceX(g5) = 25
    c: DistanceY(g5) = 35
    c: DistanceX(g6) = 58
    c: DistanceY(g6) = 43
    c: DistanceX(g7) = 85
    c: DistanceY(g7) = 45
FEATURE [PartDesign::Pad] Pad027
  Length = 8
  Length2 = 100
  Profile = -> Sketch052
  Type = 0
FEATURE [Sketcher::SketchObject] Sketch053
  ExternalGeometry = -> [Pad027]
  MapMode = 5
  Placement = pos=(0,0,8) rot=(0,0,1;0rad)
  Support = -> [Pad027]
  sketch-geometry (6):
    g0: LineSegment StartX=0 StartY=0 StartZ=0 EndX=0 EndY=60 EndZ=0
    g1: LineSegment StartX=0 StartY=60 StartZ=0 EndX=110 EndY=60 EndZ=0
    g2: LineSegment StartX=110 StartY=60 StartZ=0 EndX=110 EndY=53 EndZ=0
    g3: LineSegment StartX=110 StartY=53 StartZ=0 EndX=7 EndY=53 EndZ=0
    g4: LineSegment StartX=7 StartY=53 StartZ=0 EndX=7 EndY=0 EndZ=0
    g5: LineSegment StartX=7 StartY=0 StartZ=0 EndX=0 EndY=0 EndZ=0
  constraints (15):
    c: Coincident(g-1,g0)
    c: Coincident(g0,g-3)
    c: Coincident(g0,g1)
    c: Coincident(g1,g-3)
    c: Coincident(g1,g2)
    c: Vertical(g2)
    c: Coincident(g2,g3)
    c: Horizontal(g3)
    c: Coincident(g3,g4)
    c: PointOnObject(g4,g-1)
    c: Vertical(g4)
    c: Coincident(g4,g5)
    c: Coincident(g5,g0)
    c: Equal(g5,g2)
    c: DistanceY(g2,g2) = 7
FEATURE [PartDesign::Pad] Pad028
  BaseFeature = -> Pad027
  Length = 35
  Length2 = 100
  Profile = -> Sketch053
  Type = 0
FEATURE [PartDesign::SubtractiveCylinder] Cylinder016
  Angle = 360
  AttacherType = Attacher::AttachEngine3D
  AttachmentOffset = pos=(45,25,0) rot=(0,0,1;0rad)
  BaseFeature = -> Pad028
  Height = 40
  MapMode = 5
  Placement = pos=(4.4e-15,45,25) rot=(0.57735,0.57735,0.57735;2.0944rad)
  Radius = 3.75
  Support = -> [YZ_Plane023]
FEATURE [PartDesign::SubtractiveCylinder] Cylinder017
  Angle = 360
  AttacherType = Attacher::AttachEngine3D
  AttachmentOffset = pos=(16,25,0) rot=(0,0,1;0rad)
  BaseFeature = -> Cylinder016
  Height = 30
  MapMode = 5
  Placement = pos=(-2e-15,16,25) rot=(0.57735,0.57735,0.57735;2.0944rad)
  Radius = 3.75
  Support = -> [YZ_Plane023]
FEATURE [PartDesign::SubtractiveCylinder] Cylinder018
  Angle = 360
  AttacherType = Attacher::AttachEngine3D
  AttachmentOffset = pos=(30,25,-70) rot=(0,0,1;0rad)
  BaseFeature = -> Cylinder017
  Height = 50
  MapMode = 5
  Placement = pos=(30,70,25) rot=(1,0,0;1.5708rad)
  Radius = 2.5
  Support = -> [XZ_Plane023]
FEATURE [PartDesign::SubtractiveCylinder] Cylinder019
  Angle = 360
  AttacherType = Attacher::AttachEngine3D
  AttachmentOffset = pos=(60,25,-70) rot=(0,0,1;0rad)
  BaseFeature = -> Cylinder018
  Height = 40
  MapMode = 5
  Placement = pos=(60,70,25) rot=(1,0,0;1.5708rad)
  Radius = 2.5
  Support = -> [XZ_Plane023]
FEATURE [PartDesign::SubtractiveCylinder] Cylinder020
  Angle = 360
  AttacherType = Attacher::AttachEngine3D
  AttachmentOffset = pos=(90,25,-70) rot=(0,0,1;0rad)
  BaseFeature = -> Cylinder019
  Height = 40
  MapMode = 5
  Placement = pos=(90,70,25) rot=(1,0,0;1.5708rad)
  Radius = 2.5
  Support = -> [XZ_Plane023]
FEATURE [PartDesign::Fillet] Fillet022
  Base = -> Cylinder020 [Edge19,Edge49,Edge17,Edge26,Edge25,Edge22,Edge34]
  BaseFeature = -> Cylinder020
  Placement = pos=(90,70,25) rot=(1,0,0;1.5708rad)
  Radius = 3.5
FEATURE [PartDesign::Fillet] Fillet023
  Base = -> Fillet022 [Edge32,Edge27,Edge52,Edge51]
  BaseFeature = -> Fillet022
  Placement = pos=(90,70,25) rot=(1,0,0;1.5708rad)
  Radius = 2
FEATURE [PartDesign::Body] Body020  label="sideMountStrenthener"
  Group = -> [Sketch052,Pad027,Sketch053,Pad028,Cylinder016,Cylinder017,Cylinder018,Cylinder019,Cylinder020,Fillet022,Fillet023]
  Origin = -> Origin023
  Tip = -> Fillet023
FEATURE [Sketcher::SketchObject] Sketch054
  MapMode = 5
  Support = -> [XY_Plane024]
  expr: Constraints[40] = data.max8x8_width
  expr: Constraints[29] = data.seg7_length + 1
  sketch-geometry (16):
    g0: LineSegment StartX=-88 StartY=57 StartZ=0 EndX=-88 EndY=0 EndZ=0
    g1: LineSegment StartX=-88 StartY=0 StartZ=0 EndX=88 EndY=0 EndZ=0
    g2: LineSegment StartX=88 StartY=0 StartZ=0 EndX=88 EndY=57 EndZ=0
    g3: ArcOfCircle CenterX=7.26e-14 CenterY=-400 CenterZ=0 NormalX=0 NormalY=0 NormalZ=1 AngleXU=0 Radius=465.396 StartAngle=1.38056 EndAngle=1.76103
    g4: LineSegment StartX=-73 StartY=17.5 StartZ=0 EndX=-11 EndY=17.5 EndZ=0
    g5: LineSegment StartX=-11 StartY=17.5 StartZ=0 EndX=-11 EndY=3 EndZ=0
    g6: LineSegment StartX=-11 StartY=3 StartZ=0 EndX=-73 EndY=3 EndZ=0
    g7: LineSegment StartX=-73 StartY=3 StartZ=0 EndX=-73 EndY=17.5 EndZ=0
    g8: LineSegment StartX=11 StartY=17.5 StartZ=0 EndX=73 EndY=17.5 EndZ=0
    g9: LineSegment StartX=73 StartY=17.5 StartZ=0 EndX=73 EndY=3 EndZ=0
    g10: LineSegment StartX=73 StartY=3 StartZ=0 EndX=11 EndY=3 EndZ=0
    g11: LineSegment StartX=11 StartY=3 StartZ=0 EndX=11 EndY=17.5 EndZ=0
    g12: LineSegment StartX=-16.2 StartY=53 StartZ=0 EndX=16.2 EndY=53 EndZ=0
    g13: LineSegment StartX=16.2 StartY=53 StartZ=0 EndX=16.2 EndY=21 EndZ=0
    g14: LineSegment StartX=16.2 StartY=21 StartZ=0 EndX=-16.2 EndY=21 EndZ=0
    g15: LineSegment StartX=-16.2 StartY=21 StartZ=0 EndX=-16.2 EndY=53 EndZ=0
  constraints (46):
    c: PointOnObject(g0,g-1)
    c: Vertical(g0)
    c: Coincident(g0,g1)
    c: PointOnObject(g1,g-1)
    c: Coincident(g1,g2)
    c: Vertical(g2)
    c: Coincident(g3,g0)
    c: Coincident(g3,g2)
    c: Symmetric(g2,g0,g-2)
    c: DistanceX(g1,g1) = 176
    c: Coincident(g4,g5)
    c: Coincident(g5,g6)
    c: Coincident(g6,g7)
    c: Coincident(g7,g4)
    c: Horizontal(g4)
    c: Horizontal(g6)
    c: Vertical(g5)
    c: Vertical(g7)
    c: Coincident(g8,g9)
    c: Coincident(g9,g10)
    c: Coincident(g10,g11)
    c: Coincident(g11,g8)
    c: Horizontal(g8)
    c: Horizontal(g10)
    c: Vertical(g9)
    c: Vertical(g11)
    c: Equal(g4,g8)
    c: Equal(g5,g11)
    c: Symmetric(g4,g8,g-2)
    c: DistanceX(g4,g4) = 62
    c: DistanceX(g5) = -11
    c: DistanceY(g5) = 3  'bottomThickness'
    c: DistanceY(g7,g7) = 14.5
    c: Coincident(g12,g13)
    c: Coincident(g13,g14)
    c: Coincident(g14,g15)
    c: Coincident(g15,g12)
    c: Horizontal(g14)
    c: Vertical(g13)
    c: Vertical(g15)
    c: DistanceY(g13,g13) = 32
    c: Symmetric(g12,g12,g-2)
    c: DistanceY(g12) = 53
    c: DistanceY(g2,g2) = 57
    c: DistanceY(g3) = -400
    c: DistanceX(g12,g12) = 32.4
FEATURE [PartDesign::Pad] Pad029
  Length = 16
  Length2 = 100
  Profile = -> Sketch054
  Type = 0
FEATURE [Sketcher::SketchObject] Sketch055
  MapMode = 5
  Placement = pos=(0,0,0) rot=(1,0,0;3.14159rad)
  Support = -> [Pad029]
  sketch-geometry (8):
    g0: LineSegment StartX=-87 StartY=-2 StartZ=0 EndX=-87 EndY=-20 EndZ=0
    g1: ArcOfCircle CenterX=8.03e-14 CenterY=400 CenterZ=0 NormalX=0 NormalY=0 NormalZ=1 AngleXU=0 Radius=463.625 StartAngle=4.55646 EndAngle=4.86832
    g2: LineSegment StartX=87 StartY=-20 StartZ=0 EndX=87 EndY=-2 EndZ=0
    g3: LineSegment StartX=87 StartY=-2 StartZ=0 EndX=-87 EndY=-2 EndZ=0
    g4: LineSegment StartX=-87 StartY=-20 StartZ=0 EndX=-72 EndY=-20 EndZ=0
    g5: LineSegment StartX=-72 StartY=-20 StartZ=0 EndX=-72 EndY=-58 EndZ=0
    g6: LineSegment StartX=87 StartY=-20 StartZ=0 EndX=72 EndY=-20 EndZ=0
    g7: LineSegment StartX=72 StartY=-20 StartZ=0 EndX=72 EndY=-58 EndZ=0
  constraints (23):
    c: Vertical(g0)
    c: Vertical(g2)
    c: Coincident(g2,g3)
    c: Coincident(g3,g0)
    c: DistanceY(g0) = -2
    c: DistanceX(g3,g3) = 174
    c: DistanceY(g1) = 400
    c: Horizontal(g4)
    c: Coincident(g4,g5)
    c: Vertical(g5)
    c: Horizontal(g6)
    c: Coincident(g6,g7)
    c: Vertical(g7)
    c: Coincident(g2,g6)
    c: Coincident(g1,g7)
    c: Coincident(g1,g5)
    c: Coincident(g0,g4)
    c: Symmetric(g1,g1,g-2)
    c: Equal(g0,g2)
    c: DistanceY(g2,g2) = 18
    c: DistanceX(g1,g1) = 144
    c: Symmetric(g0,g2,g-2)
    c: DistanceY(g7,g7) = 38
FEATURE [PartDesign::Pocket] Pocket023
  BaseFeature = -> Pad029
  Length = 9
  Length2 = 100
  Profile = -> Sketch055
  Type = 0
FEATURE [Sketcher::SketchObject] Sketch056
  MapMode = 5
  Placement = pos=(0,0,9) rot=(1,0,0;3.14159rad)
  Support = -> [Pocket023]
  sketch-geometry (4):
    g0: LineSegment StartX=-30 StartY=-21 StartZ=0 EndX=-16 EndY=-21 EndZ=0
    g1: LineSegment StartX=-16 StartY=-21 StartZ=0 EndX=-16 EndY=-53 EndZ=0
    g2: LineSegment StartX=-16 StartY=-53 StartZ=0 EndX=-30 EndY=-53 EndZ=0
    g3: LineSegment StartX=-30 StartY=-53 StartZ=0 EndX=-30 EndY=-21 EndZ=0
  constraints (12):
    c: Coincident(g0,g1)
    c: Coincident(g1,g2)
    c: Coincident(g2,g3)
    c: Coincident(g3,g0)
    c: Horizontal(g0)
    c: Horizontal(g2)
    c: Vertical(g1)
    c: Vertical(g3)
    c: DistanceX(g2,g2) = 14
    c: DistanceY(g0) = -21
    c: DistanceY(g1,g1) = 32
    c: DistanceX(g1) = -16
FEATURE [PartDesign::Pocket] Pocket024
  BaseFeature = -> Pocket023
  Length = 4
  Length2 = 100
  Profile = -> Sketch056
  Type = 0
FEATURE [PartDesign::Plane] DatumPlane
  Length = 199.039
  MapMode = 2
  ResizeMode = 0
  Support = -> [XY_Plane024]
  Width = 98.4343
FEATURE [Sketcher::SketchObject] Sketch057
  MapMode = 5
  Support = -> [DatumPlane]
  sketch-geometry (34):
    g0: Circle CenterX=-49.5 CenterY=58 CenterZ=0 NormalX=0 NormalY=0 NormalZ=1 AngleXU=0 Radius=2.52
    g1: Circle CenterX=-40.5 CenterY=58 CenterZ=0 NormalX=0 NormalY=0 NormalZ=1 AngleXU=0 Radius=2.52
    g2: LineSegment [constr] StartX=-49.5 StartY=58 StartZ=0 EndX=-40.5 EndY=58 EndZ=0
    g3: Circle CenterX=-31.5 CenterY=58 CenterZ=0 NormalX=0 NormalY=0 NormalZ=1 AngleXU=0 Radius=2.52
    g4: LineSegment [constr] StartX=-40.5 StartY=58 StartZ=0 EndX=-31.5 EndY=58 EndZ=0
    g5: Circle CenterX=-22.5 CenterY=58 CenterZ=0 NormalX=0 NormalY=0 NormalZ=1 AngleXU=0 Radius=2.52
    g6: LineSegment [constr] StartX=-31.5 StartY=58 StartZ=0 EndX=-22.5 EndY=58 EndZ=0
    g7: Circle CenterX=-13.5 CenterY=58 CenterZ=0 NormalX=0 NormalY=0 NormalZ=1 AngleXU=0 Radius=2.52
    g8: LineSegment [constr] StartX=-22.5 StartY=58 StartZ=0 EndX=-13.5 EndY=58 EndZ=0
    g9: Circle CenterX=-4.5 CenterY=58 CenterZ=0 NormalX=0 NormalY=0 NormalZ=1 AngleXU=0 Radius=2.52
    g10: LineSegment [constr] StartX=-13.5 StartY=58 StartZ=0 EndX=-4.5 EndY=58 EndZ=0
    g11: Circle CenterX=4.5 CenterY=58 CenterZ=0 NormalX=0 NormalY=0 NormalZ=1 AngleXU=0 Radius=2.52
    g12: LineSegment [constr] StartX=-4.5 StartY=58 StartZ=0 EndX=4.5 EndY=58 EndZ=0
    g13: Circle CenterX=13.5 CenterY=58 CenterZ=0 NormalX=0 NormalY=0 NormalZ=1 AngleXU=0 Radius=2.52
    g14: LineSegment [constr] StartX=4.5 StartY=58 StartZ=0 EndX=13.5 EndY=58 EndZ=0
    g15: Circle CenterX=22.5 CenterY=58 CenterZ=0 NormalX=0 NormalY=0 NormalZ=1 AngleXU=0 Radius=2.52
    g16: LineSegment [constr] StartX=13.5 StartY=58 StartZ=0 EndX=22.5 EndY=58 EndZ=0
    g17: Circle CenterX=31.5 CenterY=58 CenterZ=0 NormalX=0 NormalY=0 NormalZ=1 AngleXU=0 Radius=2.52
    g18: LineSegment [constr] StartX=22.5 StartY=58 StartZ=0 EndX=31.5 EndY=58 EndZ=0
    g19: Circle CenterX=40.5 CenterY=58 CenterZ=0 NormalX=0 NormalY=0 NormalZ=1 AngleXU=0 Radius=2.52
    g20: LineSegment [constr] StartX=31.5 StartY=58 StartZ=0 EndX=40.5 EndY=58 EndZ=0
    g21: Circle CenterX=49.5 CenterY=58 CenterZ=0 NormalX=0 NormalY=0 NormalZ=1 AngleXU=0 Radius=2.52
    g22: LineSegment [constr] StartX=40.5 StartY=58 StartZ=0 EndX=49.5 EndY=58 EndZ=0
    g23: Circle CenterX=49.5 CenterY=45 CenterZ=0 NormalX=0 NormalY=0 NormalZ=1 AngleXU=0 Radius=2.52
    g24: Circle CenterX=49.5 CenterY=37.9 CenterZ=0 NormalX=0 NormalY=0 NormalZ=1 AngleXU=0 Radius=2.52
    g25: LineSegment [constr] StartX=49.5 StartY=45 StartZ=0 EndX=49.5 EndY=37.9 EndZ=0
    g26: Circle CenterX=49.5 CenterY=30.8 CenterZ=0 NormalX=0 NormalY=0 NormalZ=1 AngleXU=0 Radius=2.52
    g27: LineSegment [constr] StartX=49.5 StartY=37.9 StartZ=0 EndX=49.5 EndY=30.8 EndZ=0
    g28: Circle CenterX=49.5 CenterY=23.7 CenterZ=0 NormalX=0 NormalY=0 NormalZ=1 AngleXU=0 Radius=2.52
    g29: LineSegment [constr] StartX=49.5 StartY=30.8 StartZ=0 EndX=49.5 EndY=23.7 EndZ=0
    g30: Circle CenterX=-49.5 CenterY=23.7 CenterZ=0 NormalX=0 NormalY=0 NormalZ=1 AngleXU=0 Radius=2.52
    g31: Circle CenterX=-49.5 CenterY=30.8 CenterZ=0 NormalX=0 NormalY=0 NormalZ=1 AngleXU=0 Radius=2.52
    g32: Circle CenterX=-49.5 CenterY=37.9 CenterZ=0 NormalX=0 NormalY=0 NormalZ=1 AngleXU=0 Radius=2.52
    g33: Circle CenterX=-49.5 CenterY=45 CenterZ=0 NormalX=0 NormalY=0 NormalZ=1 AngleXU=0 Radius=2.52
  constraints (84):
    c: Radius(g0) = 2.52
    c: DistanceY(g0) = 58
    c: DistanceX(g0) = -49.5
    c: Equal(g0,g1) = 2.52
    c: Coincident(g0,g2)
    c: Coincident(g1,g2)
    c: Distance(g2) = 9
    c: Angle(g2) = 0
    c: Equal(g0,g3) = 2.52
    c: Coincident(g1,g4)
    c: Coincident(g3,g4)
    c: Equal(g2,g4)
    c: Parallel(g4,g2)
    c: Equal(g0,g5) = 2.52
    c: Coincident(g3,g6)
    c: Coincident(g5,g6)
    c: Equal(g2,g6)
    c: Parallel(g6,g2)
    c: Equal(g0,g7) = 2.52
    c: Coincident(g5,g8)
    c: Coincident(g7,g8)
    c: Equal(g2,g8)
    c: Parallel(g8,g2)
    c: Equal(g0,g9) = 2.52
    c: Coincident(g7,g10)
    c: Coincident(g9,g10)
    c: Equal(g2,g10)
    c: Parallel(g10,g2)
    c: Equal(g0,g11) = 2.52
    c: Coincident(g9,g12)
    c: Coincident(g11,g12)
    c: Equal(g2,g12)
    c: Parallel(g12,g2)
    c: Equal(g0,g13) = 2.52
    c: Coincident(g11,g14)
    c: Coincident(g13,g14)
    c: Equal(g2,g14)
    c: Parallel(g14,g2)
    c: Equal(g0,g15) = 2.52
    c: Coincident(g13,g16)
    c: Coincident(g15,g16)
    c: Equal(g2,g16)
    c: Parallel(g16,g2)
    c: Equal(g0,g17) = 2.52
    c: Coincident(g15,g18)
    c: Coincident(g17,g18)
    c: Equal(g2,g18)
    c: Parallel(g18,g2)
    c: Equal(g0,g19) = 2.52
    c: Coincident(g17,g20)
    c: Coincident(g19,g20)
    c: Equal(g2,g20)
    c: Parallel(g20,g2)
    c: Equal(g0,g21) = 2.52
    c: Coincident(g19,g22)
    c: Coincident(g21,g22)
    c: Equal(g2,g22)
    c: Parallel(g22,g2)
    c: Equal(g0,g23)
    c: DistanceX(g23) = 49.5
    c: DistanceY(g23) = 45
    c: Coincident(g23,g25)
    c: Coincident(g24,g25)
    c: Distance(g25) = 7.1
    c: Angle(g25) = -1.5708
    c: Coincident(g24,g27)
    c: Coincident(g26,g27)
    c: Equal(g25,g27)
    c: Parallel(g27,g25)
    c: Coincident(g26,g29)
    c: Coincident(g28,g29)
    c: Equal(g25,g29)
    c: Parallel(g29,g25)
    c: Equal(g0,g33)
    c: Equal(g33,g32)
    c: Equal(g32,g31)
    c: Equal(g31,g30)
    c: Symmetric(g33,g23,g-2)
    c: Symmetric(g32,g24,g-2)
    c: Symmetric(g31,g26,g-2)
    c: Symmetric(g30,g28,g-2)
    c: Equal(g0,g24)
    c: Equal(g24,g26)
    c: Equal(g26,g28)
FEATURE [PartDesign::Pocket] Pocket025
  BaseFeature = -> Pocket024
  Length = 5
  Length2 = 100
  Profile = -> Sketch057
  Reversed = true
  Type = 1
FEATURE [Sketcher::SketchObject] Sketch058
  MapMode = 5
  Support = -> [DatumPlane]
  sketch-geometry (4):
    g0: Circle CenterX=80 CenterY=25 CenterZ=0 NormalX=0 NormalY=0 NormalZ=1 AngleXU=0 Radius=1.25
    g1: Circle CenterX=80 CenterY=50 CenterZ=0 NormalX=0 NormalY=0 NormalZ=1 AngleXU=0 Radius=1.25
    g2: Circle CenterX=-80 CenterY=25 CenterZ=0 NormalX=0 NormalY=0 NormalZ=1 AngleXU=0 Radius=1.25
    g3: Circle CenterX=-80 CenterY=50 CenterZ=0 NormalX=0 NormalY=0 NormalZ=1 AngleXU=0 Radius=1.25
  constraints (10):
    c: Equal(g1,g0)
    c: Equal(g0,g2)
    c: Equal(g2,g3)
    c: Symmetric(g1,g3,g-2)
    c: Symmetric(g0,g2,g-2)
    c: DistanceX(g1) = 80
    c: Vertical(g1,g0)
    c: Radius(g3) = 1.25
    c: DistanceY(g2,g3) = 25
    c: DistanceY(g2) = 25
FEATURE [PartDesign::Pocket] Pocket026
  BaseFeature = -> Pocket025
  Length = 10
  Length2 = 100
  Profile = -> Sketch058
  Reversed = true
  Type = 0
FEATURE [PartDesign::Fillet] Fillet024
  Base = -> Pocket026 [Edge1,Edge5]
  BaseFeature = -> Pocket026
  Radius = 15
FEATURE [PartDesign::Fillet] Fillet025
  Base = -> Fillet024 [Edge3,Edge24]
  BaseFeature = -> Fillet024
  Radius = 2
FEATURE [PartDesign::Body] Body021  label="frontDisplay"
  Group = -> [Sketch054,Pad029,Sketch055,Pocket023,Sketch056,Sketch057,Pocket024,DatumPlane,Pocket025,Sketch058,Pocket026,Fillet024,Fillet025]
  Origin = -> Origin024
  Tip = -> Fillet025
FEATURE [Sketcher::SketchObject] Sketch059
  MapMode = 5
  Support = -> [XY_Plane025]
  sketch-geometry (8):
    g0: LineSegment StartX=-88 StartY=57 StartZ=0 EndX=-88 EndY=0 EndZ=0
    g1: LineSegment StartX=-88 StartY=0 StartZ=0 EndX=88 EndY=0 EndZ=0
    g2: LineSegment StartX=88 StartY=0 StartZ=0 EndX=88 EndY=57 EndZ=0
    g3: ArcOfCircle CenterX=7.26e-14 CenterY=-400 CenterZ=0 NormalX=0 NormalY=0 NormalZ=1 AngleXU=0 Radius=465.396 StartAngle=1.38056 EndAngle=1.76103
    g4: Circle CenterX=-80 CenterY=50 CenterZ=0 NormalX=0 NormalY=0 NormalZ=1 AngleXU=0 Radius=1.7
    g5: Circle CenterX=-80 CenterY=25 CenterZ=0 NormalX=0 NormalY=0 NormalZ=1 AngleXU=0 Radius=1.7
    g6: Circle CenterX=80 CenterY=25 CenterZ=0 NormalX=0 NormalY=0 NormalZ=1 AngleXU=0 Radius=1.7
    g7: Circle CenterX=80 CenterY=50 CenterZ=0 NormalX=0 NormalY=0 NormalZ=1 AngleXU=0 Radius=1.7
  constraints (22):
    c: PointOnObject(g0,g-1)
    c: Vertical(g0)
    c: Coincident(g0,g1)
    c: PointOnObject(g1,g-1)
    c: Coincident(g1,g2)
    c: Vertical(g2)
    c: Coincident(g3,g0)
    c: Coincident(g3,g2)
    c: Symmetric(g2,g0,g-2)
    c: DistanceX(g1,g1) = 176
    c: DistanceY(g2,g2) = 57
    c: DistanceY(g3) = -400
    c: Symmetric(g4,g7,g-2)
    c: Symmetric(g6,g5,g-2)
    c: Vertical(g4,g5)
    c: DistanceX(g5) = -80
    c: Equal(g5,g4)
    c: Equal(g4,g7)
    c: Equal(g7,g6)
    c: DistanceY(g5) = 25
    c: DistanceY(g4) = 50
    c: Radius(g5) = 1.7
FEATURE [PartDesign::Pad] Pad030
  Length = 2.2
  Length2 = 100
  Profile = -> Sketch059
  Type = 0
FEATURE [PartDesign::Fillet] Fillet026
  Base = -> Pad030 [Edge1,Edge8]
  BaseFeature = -> Pad030
  Radius = 15
FEATURE [PartDesign::Fillet] Fillet027
  Base = -> Fillet026 [Edge3,Edge16]
  BaseFeature = -> Fillet026
  Radius = 2
FEATURE [Sketcher::SketchObject] Sketch060
  MapMode = 5
  Placement = pos=(0,0,2.2) rot=(0,0,1;0rad)
  Support = -> [Fillet027]
  sketch-geometry (4):
    g0: LineSegment StartX=-40 StartY=27.5 StartZ=0 EndX=40 EndY=27.5 EndZ=0
    g1: LineSegment StartX=40 StartY=27.5 StartZ=0 EndX=40 EndY=7.5 EndZ=0
    g2: LineSegment StartX=40 StartY=7.5 StartZ=0 EndX=-40 EndY=7.5 EndZ=0
    g3: LineSegment StartX=-40 StartY=7.5 StartZ=0 EndX=-40 EndY=27.5 EndZ=0
  constraints (11):
    c: Coincident(g0,g1)
    c: Coincident(g1,g2)
    c: Coincident(g2,g3)
    c: Coincident(g3,g0)
    c: Horizontal(g0)
    c: Vertical(g1)
    c: Vertical(g3)
    c: Symmetric(g2,g1,g-2)
    c: DistanceX(g2,g2) = 80
    c: DistanceY(g1) = 7.5
    c: DistanceY(g1,g1) = 20
FEATURE [PartDesign::Pad] Pad031
  BaseFeature = -> Fillet027
  Length = 9.8
  Length2 = 100
  Profile = -> Sketch060
  Type = 0
FEATURE [Sketcher::SketchObject] Sketch061
  ExternalGeometry = -> [Pad031]
  MapMode = 5
  Placement = pos=(0,0,12) rot=(0,0,1;0rad)
  Support = -> [Pad031]
  sketch-geometry (4):
    g0: LineSegment StartX=-40 StartY=27.5 StartZ=0 EndX=40 EndY=27.5 EndZ=0
    g1: LineSegment StartX=40 StartY=27.5 StartZ=0 EndX=40 EndY=17.5 EndZ=0
    g2: LineSegment StartX=40 StartY=17.5 StartZ=0 EndX=-40 EndY=17.5 EndZ=0
    g3: LineSegment StartX=-40 StartY=17.5 StartZ=0 EndX=-40 EndY=27.5 EndZ=0
  constraints (11):
    c: Coincident(g0,g1)
    c: Coincident(g1,g2)
    c: Coincident(g2,g3)
    c: Coincident(g3,g0)
    c: Horizontal(g0)
    c: Horizontal(g2)
    c: Vertical(g1)
    c: Vertical(g3)
    c: Coincident(g0,g-3)
    c: DistanceX(g0,g0) = 80
    c: DistanceY(g1,g1) = 10
FEATURE [PartDesign::Pad] Pad032
  BaseFeature = -> Pad031
  Length = 15
  Length2 = 100
  Profile = -> Sketch061
  Type = 0
FEATURE [Sketcher::SketchObject] Sketch062
  MapMode = 5
  Placement = pos=(0,0,0) rot=(1,0,0;3.14159rad)
  Support = -> [Pad032]
  sketch-geometry (8):
    g0: Circle CenterX=-30 CenterY=-14 CenterZ=0 NormalX=0 NormalY=0 NormalZ=1 AngleXU=0 Radius=6
    g1: Circle CenterX=-10 CenterY=-14 CenterZ=0 NormalX=0 NormalY=0 NormalZ=1 AngleXU=0 Radius=6
    g2: Circle CenterX=10 CenterY=-14 CenterZ=0 NormalX=0 NormalY=0 NormalZ=1 AngleXU=0 Radius=6
    g3: Circle CenterX=30 CenterY=-14 CenterZ=0 NormalX=0 NormalY=0 NormalZ=1 AngleXU=0 Radius=6
    g4: ArcOfCircle CenterX=-60 CenterY=-45 CenterZ=0 NormalX=0 NormalY=0 NormalZ=1 AngleXU=0 Radius=3.5 StartAngle=1.5708 EndAngle=4.71239
    g5: ArcOfCircle CenterX=-40 CenterY=-45 CenterZ=0 NormalX=0 NormalY=0 NormalZ=1 AngleXU=0 Radius=3.5 StartAngle=4.71239 EndAngle=7.85398
    g6: LineSegment StartX=-60 StartY=-48.5 StartZ=0 EndX=-40 EndY=-48.5 EndZ=0
    g7: LineSegment StartX=-60 StartY=-41.5 StartZ=0 EndX=-40 EndY=-41.5 EndZ=0
  constraints (20):
    c: Symmetric(g0,g3,g-2)
    c: Symmetric(g1,g2,g-2)
    c: Horizontal(g0,g1)
    c: Equal(g0,g1)
    c: Equal(g1,g2)
    c: Equal(g2,g3)
    c: Radius(g3) = 6
    c: DistanceX(g0) = -30
    c: DistanceX(g2) = 10
    c: Tangent(g4,g7) = 1.5708
    c: Tangent(g4,g6) = -1.5708
    c: Tangent(g6,g5) = -1.5708
    c: Tangent(g7,g5) = 1.5708
    c: Horizontal(g6)
    c: Equal(g4,g5)
    c: DistanceY(g4) = -45
    c: Radius(g5) = 3.5
    c: DistanceX(g4,g5) = 20
    c: DistanceX(g4) = -60
    c: DistanceY(g0) = -14
FEATURE [PartDesign::Pocket] Pocket027
  BaseFeature = -> Pad032
  Length = 11
  Length2 = 100
  Profile = -> Sketch062
  Type = 0
FEATURE [Sketcher::SketchObject] Sketch063
  ExternalGeometry = -> [Pocket027]
  MapMode = 5
  Placement = pos=(0,27.5,0) rot=(0,0.707107,0.707107;3.14159rad)
  Support = -> [Pocket027]
  sketch-geometry (3):
    g0: Circle CenterX=29 CenterY=19.5 CenterZ=0 NormalX=0 NormalY=0 NormalZ=1 AngleXU=0 Radius=5.5
    g1: Circle CenterX=0 CenterY=19.5 CenterZ=0 NormalX=0 NormalY=0 NormalZ=1 AngleXU=0 Radius=5.5
    g2: Circle CenterX=-29 CenterY=19.5 CenterZ=0 NormalX=0 NormalY=0 NormalZ=1 AngleXU=0 Radius=5.5
  constraints (8):
    c: PointOnObject(g1,g-2)
    c: Equal(g0,g1)
    c: Equal(g1,g2)
    c: Radius(g2) = 5.5
    c: Symmetric(g0,g2,g-2)
    c: Horizontal(g1,g0)
    c: DistanceY(g1) = 19.5
    c: DistanceX(g0) = 29
FEATURE [PartDesign::Pocket] Pocket028
  BaseFeature = -> Pocket027
  Length = 6.6
  Length2 = 100
  Profile = -> Sketch063
  Type = 0
FEATURE [PartDesign::Fillet] Fillet028
  Base = -> Pocket028 [Edge40,Edge42,Edge41,Edge39]
  BaseFeature = -> Pocket028
  Radius = 5
FEATURE [PartDesign::Fillet] Fillet029
  Base = -> Fillet028 [Face19]
  BaseFeature = -> Fillet028
  Radius = 1
FEATURE [PartDesign::Fillet] Fillet030
  Base = -> Fillet029 [Edge84,Edge83,Edge86,Edge85,Edge99,Edge101,Edge100,Edge110]
  BaseFeature = -> Fillet029
  Radius = 2
FEATURE [PartDesign::Fillet] Fillet031
  Base = -> Fillet030 [Edge41,Edge44]
  BaseFeature = -> Fillet030
  Radius = 1.5
FEATURE [PartDesign::Body] Body022  label="frontDisplayBack"
  Group = -> [Sketch059,Pad030,Fillet026,Fillet027,Sketch060,Pad031,Sketch061,Pad032,Sketch062,Pocket027,Sketch063,Pocket028,Fillet028,Fillet029,Fillet030,Fillet031]
  Origin = -> Origin025
  Tip = -> Fillet031
